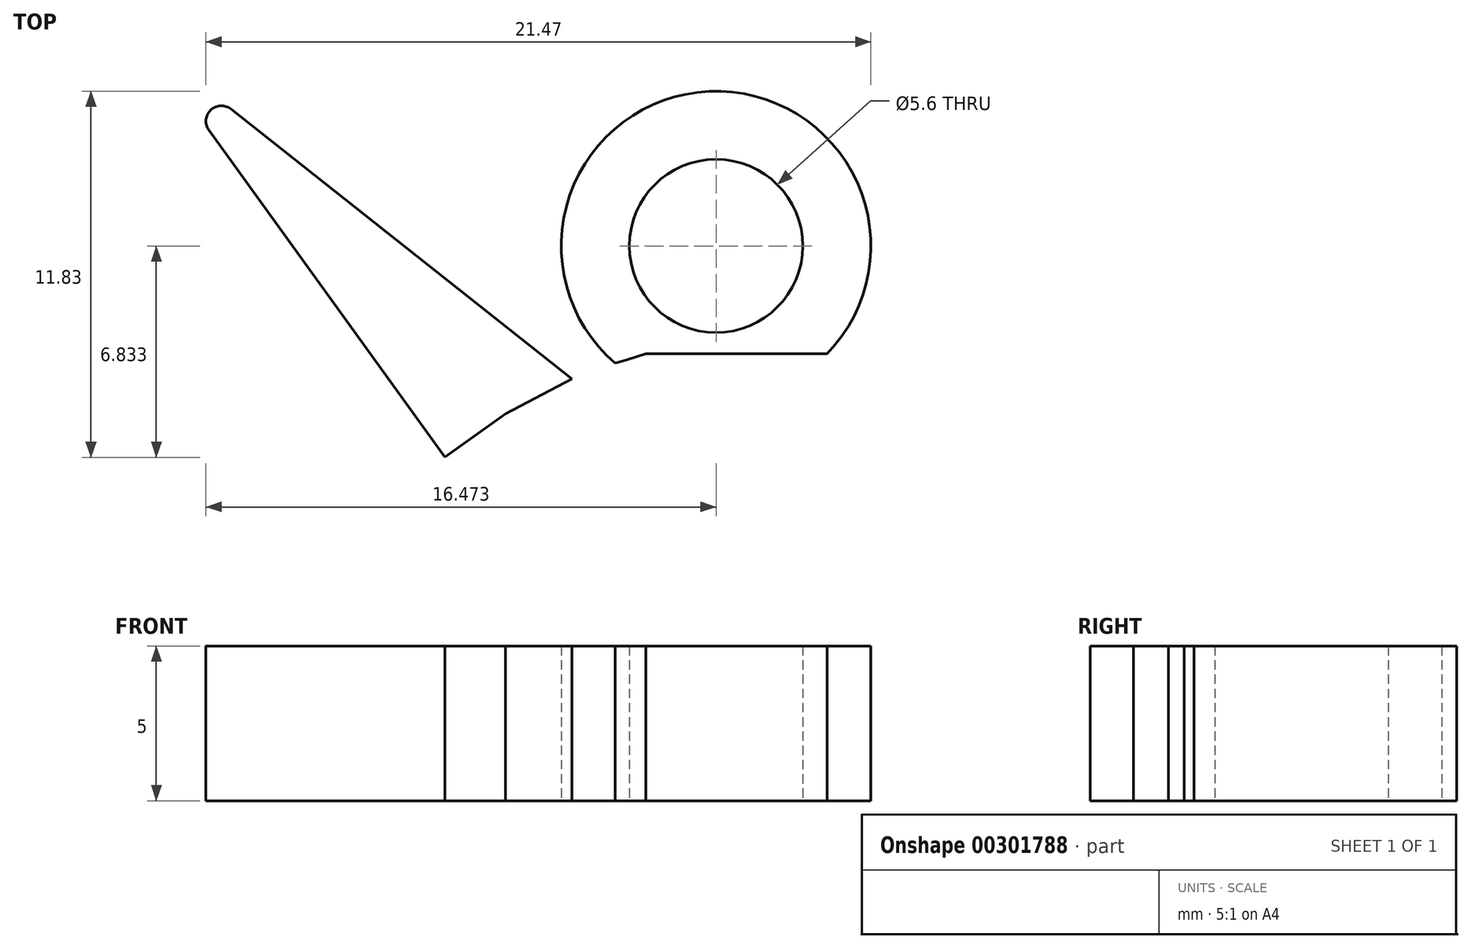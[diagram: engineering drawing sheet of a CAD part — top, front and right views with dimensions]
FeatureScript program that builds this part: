
annotation { "Feature Type Name" : "Feature", "Feature Type Description" : "" }
export const myFeature = defineFeature(function(context is Context, id is Id, definition is map)
    precondition{}
    {
        {
            var Q0;
            Q0=qCreatedBy(makeId("Top.planeOp"),FACE);
            var sketch = newSketch(context, id + "F0", { "sketchPlane" : qUnion([Q0])});
            skLineSegment(sketch, "E0", {"start": v(-9.72, 30) * mm, "end": v(0.2, 30) * mm});
            skLineSegment(sketch, "E1", {"start": v(0.2, 30) * mm, "end": v(10.14, 30) * mm});
            skLineSegment(sketch, "E2", {"start": v(10.14, 30) * mm, "end": v(20.07, 30) * mm});
            skLineSegment(sketch, "E3", {"start": v(20.07, 30) * mm, "end": v(30, 30) * mm});
            skLineSegment(sketch, "E4", {"start": v(30, 15) * mm, "end": v(30, 0) * mm});
            skLineSegment(sketch, "E5", {"start": v(30, 0) * mm, "end": v(30, -15) * mm});
            skLineSegment(sketch, "E6", {"start": v(30, -15) * mm, "end": v(30, -30) * mm});
            skLineSegment(sketch, "E7", {"start": v(30, -30) * mm, "end": v(19.17, -30) * mm});
            skLineSegment(sketch, "E8", {"start": v(19.17, -30) * mm, "end": v(8.34, -30) * mm});
            skLineSegment(sketch, "E9", {"start": v(8.34, -30) * mm, "end": v(-2.49, -30) * mm});
            skLineSegment(sketch, "E10", {"start": v(-2.49, -30) * mm, "end": v(-13.32, -30) * mm});
            skLineSegment(sketch, "E11", {"start": v(-13.32, -30) * mm, "end": v(-12.87, -29.51) * mm});
            skLineSegment(sketch, "E12", {"start": v(-12.87, -29.51) * mm, "end": v(-12.4, -29.04) * mm});
            skLineSegment(sketch, "E13", {"start": v(-12.4, -29.04) * mm, "end": v(-11.98, -28.54) * mm});
            skLineSegment(sketch, "E14", {"start": v(-11.98, -28.54) * mm, "end": v(-11.7, -28) * mm});
            skLineSegment(sketch, "E15", {"start": v(-11.7, -28) * mm, "end": v(-10.95, -26.2) * mm});
            skLineSegment(sketch, "E16", {"start": v(-10.95, -26.2) * mm, "end": v(-10.13, -24.44) * mm});
            skLineSegment(sketch, "E17", {"start": v(-10.13, -24.44) * mm, "end": v(-9.4, -22.64) * mm});
            skLineSegment(sketch, "E18", {"start": v(-9.4, -22.64) * mm, "end": v(-8.98, -20.73) * mm});
            skLineSegment(sketch, "E19", {"start": v(-8.98, -20.73) * mm, "end": v(-8.9, -20.42) * mm});
            skLineSegment(sketch, "E20", {"start": v(-8.9, -20.42) * mm, "end": v(-8.72, -20.17) * mm});
            skLineSegment(sketch, "E21", {"start": v(-8.72, -20.17) * mm, "end": v(-8.45, -20.01) * mm});
            skLineSegment(sketch, "E22", {"start": v(-8.45, -20.01) * mm, "end": v(-8.12, -19.96) * mm});
            skLineSegment(sketch, "E23", {"start": v(-8.12, -19.96) * mm, "end": v(-7.68, -19.98) * mm});
            skLineSegment(sketch, "E24", {"start": v(-7.68, -19.98) * mm, "end": v(-7.25, -20.02) * mm});
            skLineSegment(sketch, "E25", {"start": v(-7.25, -20.02) * mm, "end": v(-6.82, -20.06) * mm});
            skLineSegment(sketch, "E26", {"start": v(-6.82, -20.06) * mm, "end": v(-6.39, -20.1) * mm});
            skLineSegment(sketch, "E27", {"start": v(-6.39, -20.1) * mm, "end": v(-5.28, -20.19) * mm});
            skLineSegment(sketch, "E28", {"start": v(-5.28, -20.19) * mm, "end": v(-4.18, -20.28) * mm});
            skLineSegment(sketch, "E29", {"start": v(-4.18, -20.28) * mm, "end": v(-3.08, -20.35) * mm});
            skLineSegment(sketch, "E30", {"start": v(-3.08, -20.35) * mm, "end": v(-1.97, -20.37) * mm});
            skLineSegment(sketch, "E31", {"start": v(-1.97, -20.37) * mm, "end": v(-1.38, -20.31) * mm});
            skLineSegment(sketch, "E32", {"start": v(-1.38, -20.31) * mm, "end": v(-0.78, -20.18) * mm});
            skLineSegment(sketch, "E33", {"start": v(-0.78, -20.18) * mm, "end": v(-0.18, -20.02) * mm});
            skLineSegment(sketch, "E34", {"start": v(-0.18, -20.02) * mm, "end": v(0.42, -19.86) * mm});
            skLineSegment(sketch, "E35", {"start": v(0.42, -19.86) * mm, "end": v(0.94, -19.84) * mm});
            skLineSegment(sketch, "E36", {"start": v(0.94, -19.84) * mm, "end": v(1.34, -20) * mm});
            skLineSegment(sketch, "E37", {"start": v(1.34, -20) * mm, "end": v(1.6, -20.34) * mm});
            skLineSegment(sketch, "E38", {"start": v(1.6, -20.34) * mm, "end": v(1.7, -20.85) * mm});
            skLineSegment(sketch, "E39", {"start": v(1.7, -20.85) * mm, "end": v(1.69, -21.03) * mm});
            skLineSegment(sketch, "E40", {"start": v(1.69, -21.03) * mm, "end": v(1.67, -21.2) * mm});
            skLineSegment(sketch, "E41", {"start": v(1.67, -21.2) * mm, "end": v(1.65, -21.38) * mm});
            skLineSegment(sketch, "E42", {"start": v(1.65, -21.38) * mm, "end": v(1.61, -21.56) * mm});
            skLineSegment(sketch, "E43", {"start": v(1.61, -21.56) * mm, "end": v(1.44, -22.04) * mm});
            skLineSegment(sketch, "E44", {"start": v(1.44, -22.04) * mm, "end": v(1.19, -22.29) * mm});
            skLineSegment(sketch, "E45", {"start": v(1.19, -22.29) * mm, "end": v(0.84, -22.3) * mm});
            skLineSegment(sketch, "E46", {"start": v(0.84, -22.3) * mm, "end": v(0.37, -22.1) * mm});
            skLineSegment(sketch, "E47", {"start": v(0.37, -22.1) * mm, "end": v(-0.3, -21.8) * mm});
            skLineSegment(sketch, "E48", {"start": v(-0.3, -21.8) * mm, "end": v(-1, -21.59) * mm});
            skLineSegment(sketch, "E49", {"start": v(-1, -21.59) * mm, "end": v(-1.72, -21.49) * mm});
            skLineSegment(sketch, "E50", {"start": v(-1.72, -21.49) * mm, "end": v(-2.45, -21.48) * mm});
            skLineSegment(sketch, "E51", {"start": v(-2.45, -21.48) * mm, "end": v(-3.08, -21.63) * mm});
            skLineSegment(sketch, "E52", {"start": v(-3.08, -21.63) * mm, "end": v(-3.5, -22) * mm});
            skLineSegment(sketch, "E53", {"start": v(-3.5, -22) * mm, "end": v(-3.7, -22.5) * mm});
            skLineSegment(sketch, "E54", {"start": v(-3.7, -22.5) * mm, "end": v(-3.58, -23.06) * mm});
            skLineSegment(sketch, "E55", {"start": v(-3.58, -23.06) * mm, "end": v(-2.94, -24.22) * mm});
            skLineSegment(sketch, "E56", {"start": v(-2.94, -24.22) * mm, "end": v(-2.19, -25.3) * mm});
            skLineSegment(sketch, "E57", {"start": v(-2.19, -25.3) * mm, "end": v(-1.3, -26.25) * mm});
            skLineSegment(sketch, "E58", {"start": v(-1.3, -26.25) * mm, "end": v(-0.23, -27.05) * mm});
            skLineSegment(sketch, "E59", {"start": v(-0.23, -27.05) * mm, "end": v(0.72, -27.6) * mm});
            skLineSegment(sketch, "E60", {"start": v(0.72, -27.6) * mm, "end": v(1.68, -28.11) * mm});
            skLineSegment(sketch, "E61", {"start": v(1.68, -28.11) * mm, "end": v(2.65, -28.62) * mm});
            skLineSegment(sketch, "E62", {"start": v(2.65, -28.62) * mm, "end": v(3.6, -29.15) * mm});
            skLineSegment(sketch, "E63", {"start": v(3.6, -29.15) * mm, "end": v(4.42, -29.38) * mm});
            skLineSegment(sketch, "E64", {"start": v(4.42, -29.38) * mm, "end": v(5.22, -29.2) * mm});
            skLineSegment(sketch, "E65", {"start": v(5.22, -29.2) * mm, "end": v(5.84, -28.62) * mm});
            skLineSegment(sketch, "E66", {"start": v(5.84, -28.62) * mm, "end": v(6.1, -27.63) * mm});
            skLineSegment(sketch, "E67", {"start": v(6.1, -27.63) * mm, "end": v(6.16, -25.8) * mm});
            skLineSegment(sketch, "E68", {"start": v(6.16, -25.8) * mm, "end": v(6.27, -23.95) * mm});
            skLineSegment(sketch, "E69", {"start": v(6.27, -23.95) * mm, "end": v(6.39, -22.12) * mm});
            skLineSegment(sketch, "E70", {"start": v(6.39, -22.12) * mm, "end": v(6.52, -20.28) * mm});
            skLineSegment(sketch, "E71", {"start": v(6.52, -20.28) * mm, "end": v(6.59, -19.83) * mm});
            skLineSegment(sketch, "E72", {"start": v(6.59, -19.83) * mm, "end": v(6.75, -19.55) * mm});
            skLineSegment(sketch, "E73", {"start": v(6.75, -19.55) * mm, "end": v(7.02, -19.43) * mm});
            skLineSegment(sketch, "E74", {"start": v(7.02, -19.43) * mm, "end": v(7.45, -19.42) * mm});
            skLineSegment(sketch, "E75", {"start": v(7.45, -19.42) * mm, "end": v(8.86, -19.4) * mm});
            skLineSegment(sketch, "E76", {"start": v(8.86, -19.4) * mm, "end": v(10.22, -19.2) * mm});
            skLineSegment(sketch, "E77", {"start": v(10.22, -19.2) * mm, "end": v(11.54, -18.8) * mm});
            skLineSegment(sketch, "E78", {"start": v(11.54, -18.8) * mm, "end": v(12.83, -18.26) * mm});
            skLineSegment(sketch, "E79", {"start": v(12.83, -18.26) * mm, "end": v(14.91, -16.97) * mm});
            skLineSegment(sketch, "E80", {"start": v(14.91, -16.97) * mm, "end": v(16.69, -15.38) * mm});
            skLineSegment(sketch, "E81", {"start": v(16.69, -15.38) * mm, "end": v(18.24, -13.56) * mm});
            skLineSegment(sketch, "E82", {"start": v(18.24, -13.56) * mm, "end": v(19.64, -11.58) * mm});
            skLineSegment(sketch, "E83", {"start": v(19.64, -11.58) * mm, "end": v(19.78, -11.28) * mm});
            skLineSegment(sketch, "E84", {"start": v(19.78, -11.28) * mm, "end": v(19.85, -10.93) * mm});
            skLineSegment(sketch, "E85", {"start": v(19.85, -10.93) * mm, "end": v(19.89, -10.57) * mm});
            skLineSegment(sketch, "E86", {"start": v(19.89, -10.57) * mm, "end": v(19.94, -10.21) * mm});
            skLineSegment(sketch, "E87", {"start": v(19.94, -10.21) * mm, "end": v(19.98, -10.02) * mm});
            skLineSegment(sketch, "E88", {"start": v(19.98, -10.02) * mm, "end": v(20.01, -9.84) * mm});
            skLineSegment(sketch, "E89", {"start": v(20.01, -9.84) * mm, "end": v(20.06, -9.66) * mm});
            skLineSegment(sketch, "E90", {"start": v(20.06, -9.66) * mm, "end": v(20.14, -9.5) * mm});
            skLineSegment(sketch, "E91", {"start": v(20.14, -9.5) * mm, "end": v(20.58, -9.2) * mm});
            skLineSegment(sketch, "E92", {"start": v(20.58, -9.2) * mm, "end": v(21.19, -9.15) * mm});
            skLineSegment(sketch, "E93", {"start": v(21.19, -9.15) * mm, "end": v(21.8, -9.3) * mm});
            skLineSegment(sketch, "E94", {"start": v(21.8, -9.3) * mm, "end": v(22.28, -9.67) * mm});
            skLineSegment(sketch, "E95", {"start": v(22.28, -9.67) * mm, "end": v(22.59, -9.96) * mm});
            skLineSegment(sketch, "E96", {"start": v(22.59, -9.96) * mm, "end": v(22.88, -10.07) * mm});
            skLineSegment(sketch, "E97", {"start": v(22.88, -10.07) * mm, "end": v(23.14, -10) * mm});
            skLineSegment(sketch, "E98", {"start": v(23.14, -10) * mm, "end": v(23.34, -9.7) * mm});
            skLineSegment(sketch, "E99", {"start": v(23.34, -9.7) * mm, "end": v(23.59, -9.28) * mm});
            skLineSegment(sketch, "E100", {"start": v(23.59, -9.28) * mm, "end": v(23.91, -9.02) * mm});
            skLineSegment(sketch, "E101", {"start": v(23.91, -9.02) * mm, "end": v(24.3, -8.88) * mm});
            skLineSegment(sketch, "E102", {"start": v(24.3, -8.88) * mm, "end": v(24.74, -8.82) * mm});
            skLineSegment(sketch, "E103", {"start": v(24.74, -8.82) * mm, "end": v(25.11, -8.75) * mm});
            skLineSegment(sketch, "E104", {"start": v(25.11, -8.75) * mm, "end": v(25.4, -8.6) * mm});
            skLineSegment(sketch, "E105", {"start": v(25.4, -8.6) * mm, "end": v(25.57, -8.35) * mm});
            skLineSegment(sketch, "E106", {"start": v(25.57, -8.35) * mm, "end": v(25.6, -7.94) * mm});
            skLineSegment(sketch, "E107", {"start": v(25.6, -7.94) * mm, "end": v(25.62, -7.8) * mm});
            skLineSegment(sketch, "E108", {"start": v(25.62, -7.8) * mm, "end": v(25.67, -7.66) * mm});
            skLineSegment(sketch, "E109", {"start": v(25.67, -7.66) * mm, "end": v(25.75, -7.52) * mm});
            skLineSegment(sketch, "E110", {"start": v(25.75, -7.52) * mm, "end": v(25.82, -7.4) * mm});
            skLineSegment(sketch, "E111", {"start": v(25.82, -7.4) * mm, "end": v(26.1, -6.66) * mm});
            skLineSegment(sketch, "E112", {"start": v(26.1, -6.66) * mm, "end": v(26.15, -5.95) * mm});
            skLineSegment(sketch, "E113", {"start": v(26.15, -5.95) * mm, "end": v(25.97, -5.26) * mm});
            skLineSegment(sketch, "E114", {"start": v(25.97, -5.26) * mm, "end": v(25.57, -4.6) * mm});
            skLineSegment(sketch, "E115", {"start": v(25.57, -4.6) * mm, "end": v(25.38, -4.34) * mm});
            skLineSegment(sketch, "E116", {"start": v(25.38, -4.34) * mm, "end": v(25.19, -4.07) * mm});
            skLineSegment(sketch, "E117", {"start": v(25.19, -4.07) * mm, "end": v(24.98, -3.79) * mm});
            skLineSegment(sketch, "E118", {"start": v(24.98, -3.79) * mm, "end": v(24.77, -3.49) * mm});
            skLineSegment(sketch, "E119", {"start": v(24.77, -3.49) * mm, "end": v(25.33, -3.5) * mm});
            skLineSegment(sketch, "E120", {"start": v(25.33, -3.5) * mm, "end": v(25.85, -3.52) * mm});
            skLineSegment(sketch, "E121", {"start": v(25.85, -3.52) * mm, "end": v(26.33, -3.44) * mm});
            skLineSegment(sketch, "E122", {"start": v(26.33, -3.44) * mm, "end": v(26.74, -3.1) * mm});
            skLineSegment(sketch, "E123", {"start": v(26.74, -3.1) * mm, "end": v(26.49, -2.7) * mm});
            skLineSegment(sketch, "E124", {"start": v(26.49, -2.7) * mm, "end": v(26.14, -2.47) * mm});
            skLineSegment(sketch, "E125", {"start": v(26.14, -2.47) * mm, "end": v(25.72, -2.36) * mm});
            skLineSegment(sketch, "E126", {"start": v(25.72, -2.36) * mm, "end": v(25.28, -2.3) * mm});
            skLineSegment(sketch, "E127", {"start": v(25.28, -2.3) * mm, "end": v(24.84, -2.2) * mm});
            skLineSegment(sketch, "E128", {"start": v(24.84, -2.2) * mm, "end": v(24.64, -2.05) * mm});
            skLineSegment(sketch, "E129", {"start": v(24.64, -2.05) * mm, "end": v(24.62, -1.79) * mm});
            skLineSegment(sketch, "E130", {"start": v(24.62, -1.79) * mm, "end": v(24.77, -1.37) * mm});
            skLineSegment(sketch, "E131", {"start": v(24.77, -1.37) * mm, "end": v(24.8, -1.2) * mm});
            skLineSegment(sketch, "E132", {"start": v(24.8, -1.2) * mm, "end": v(24.8, -1) * mm});
            skLineSegment(sketch, "E133", {"start": v(24.8, -1) * mm, "end": v(24.77, -0.83) * mm});
            skLineSegment(sketch, "E134", {"start": v(24.77, -0.83) * mm, "end": v(24.7, -0.72) * mm});
            skLineSegment(sketch, "E135", {"start": v(24.7, -0.72) * mm, "end": v(24.29, -0.43) * mm});
            skLineSegment(sketch, "E136", {"start": v(24.29, -0.43) * mm, "end": v(23.88, -0.15) * mm});
            skLineSegment(sketch, "E137", {"start": v(23.88, -0.15) * mm, "end": v(23.45, 0.1) * mm});
            skLineSegment(sketch, "E138", {"start": v(23.45, 0.1) * mm, "end": v(23, 0.3) * mm});
            skLineSegment(sketch, "E139", {"start": v(23, 0.3) * mm, "end": v(22.68, 0.36) * mm});
            skLineSegment(sketch, "E140", {"start": v(22.68, 0.36) * mm, "end": v(22.33, 0.36) * mm});
            skLineSegment(sketch, "E141", {"start": v(22.33, 0.36) * mm, "end": v(21.98, 0.32) * mm});
            skLineSegment(sketch, "E142", {"start": v(21.98, 0.32) * mm, "end": v(21.63, 0.26) * mm});
            skLineSegment(sketch, "E143", {"start": v(21.63, 0.26) * mm, "end": v(21.38, 0.19) * mm});
            skLineSegment(sketch, "E144", {"start": v(21.38, 0.19) * mm, "end": v(21.13, 0.08) * mm});
            skLineSegment(sketch, "E145", {"start": v(21.13, 0.08) * mm, "end": v(20.88, -0.04) * mm});
            skLineSegment(sketch, "E146", {"start": v(20.88, -0.04) * mm, "end": v(20.63, -0.14) * mm});
            skLineSegment(sketch, "E147", {"start": v(20.63, -0.14) * mm, "end": v(20.5, -0.15) * mm});
            skLineSegment(sketch, "E148", {"start": v(20.5, -0.15) * mm, "end": v(20.37, -0.14) * mm});
            skLineSegment(sketch, "E149", {"start": v(20.37, -0.14) * mm, "end": v(20.23, -0.11) * mm});
            skLineSegment(sketch, "E150", {"start": v(20.23, -0.11) * mm, "end": v(20.1, -0.1) * mm});
            skLineSegment(sketch, "E151", {"start": v(20.1, -0.1) * mm, "end": v(20.13, 0.05) * mm});
            skLineSegment(sketch, "E152", {"start": v(20.13, 0.05) * mm, "end": v(20.16, 0.19) * mm});
            skLineSegment(sketch, "E153", {"start": v(20.16, 0.19) * mm, "end": v(20.2, 0.32) * mm});
            skLineSegment(sketch, "E154", {"start": v(20.2, 0.32) * mm, "end": v(20.26, 0.42) * mm});
            skLineSegment(sketch, "E155", {"start": v(20.26, 0.42) * mm, "end": v(20.7, 0.96) * mm});
            skLineSegment(sketch, "E156", {"start": v(20.7, 0.96) * mm, "end": v(21.07, 1.53) * mm});
            skLineSegment(sketch, "E157", {"start": v(21.07, 1.53) * mm, "end": v(21.36, 2.15) * mm});
            skLineSegment(sketch, "E158", {"start": v(21.36, 2.15) * mm, "end": v(21.58, 2.8) * mm});
            skLineSegment(sketch, "E159", {"start": v(21.58, 2.8) * mm, "end": v(21.8, 3.55) * mm});
            skLineSegment(sketch, "E160", {"start": v(21.8, 3.55) * mm, "end": v(22.03, 4.3) * mm});
            skLineSegment(sketch, "E161", {"start": v(22.03, 4.3) * mm, "end": v(22.26, 5.04) * mm});
            skLineSegment(sketch, "E162", {"start": v(22.26, 5.04) * mm, "end": v(22.5, 5.78) * mm});
            skLineSegment(sketch, "E163", {"start": v(22.5, 5.78) * mm, "end": v(22.83, 7.49) * mm});
            skLineSegment(sketch, "E164", {"start": v(22.83, 7.49) * mm, "end": v(22.65, 9.09) * mm});
            skLineSegment(sketch, "E165", {"start": v(22.65, 9.09) * mm, "end": v(21.97, 10.54) * mm});
            skLineSegment(sketch, "E166", {"start": v(21.97, 10.54) * mm, "end": v(20.8, 11.82) * mm});
            skLineSegment(sketch, "E167", {"start": v(20.8, 11.82) * mm, "end": v(19.35, 12.58) * mm});
            skLineSegment(sketch, "E168", {"start": v(19.35, 12.58) * mm, "end": v(17.91, 12.58) * mm});
            skLineSegment(sketch, "E169", {"start": v(17.91, 12.58) * mm, "end": v(16.66, 11.87) * mm});
            skLineSegment(sketch, "E170", {"start": v(16.66, 11.87) * mm, "end": v(15.78, 10.5) * mm});
            skLineSegment(sketch, "E171", {"start": v(15.78, 10.5) * mm, "end": v(15.44, 9.6) * mm});
            skLineSegment(sketch, "E172", {"start": v(15.44, 9.6) * mm, "end": v(15.08, 8.71) * mm});
            skLineSegment(sketch, "E173", {"start": v(15.08, 8.71) * mm, "end": v(14.72, 7.83) * mm});
            skLineSegment(sketch, "E174", {"start": v(14.72, 7.83) * mm, "end": v(14.36, 6.94) * mm});
            skLineSegment(sketch, "E175", {"start": v(14.36, 6.94) * mm, "end": v(14.2, 6.53) * mm});
            skLineSegment(sketch, "E176", {"start": v(14.2, 6.53) * mm, "end": v(14.03, 6.1) * mm});
            skLineSegment(sketch, "E177", {"start": v(14.03, 6.1) * mm, "end": v(13.86, 5.7) * mm});
            skLineSegment(sketch, "E178", {"start": v(13.86, 5.7) * mm, "end": v(13.67, 5.3) * mm});
            skLineSegment(sketch, "E179", {"start": v(13.67, 5.3) * mm, "end": v(13.36, 4.67) * mm});
            skLineSegment(sketch, "E180", {"start": v(13.36, 4.67) * mm, "end": v(13.04, 4.04) * mm});
            skLineSegment(sketch, "E181", {"start": v(13.04, 4.04) * mm, "end": v(12.7, 3.43) * mm});
            skLineSegment(sketch, "E182", {"start": v(12.7, 3.43) * mm, "end": v(12.36, 2.82) * mm});
            skLineSegment(sketch, "E183", {"start": v(12.36, 2.82) * mm, "end": v(12.07, 2.48) * mm});
            skLineSegment(sketch, "E184", {"start": v(12.07, 2.48) * mm, "end": v(11.72, 2.3) * mm});
            skLineSegment(sketch, "E185", {"start": v(11.72, 2.3) * mm, "end": v(11.3, 2.28) * mm});
            skLineSegment(sketch, "E186", {"start": v(11.3, 2.28) * mm, "end": v(10.85, 2.35) * mm});
            skLineSegment(sketch, "E187", {"start": v(10.85, 2.35) * mm, "end": v(10.25, 2.5) * mm});
            skLineSegment(sketch, "E188", {"start": v(10.25, 2.5) * mm, "end": v(9.64, 2.62) * mm});
            skLineSegment(sketch, "E189", {"start": v(9.64, 2.62) * mm, "end": v(9.03, 2.7) * mm});
            skLineSegment(sketch, "E190", {"start": v(9.03, 2.7) * mm, "end": v(8.43, 2.71) * mm});
            skLineSegment(sketch, "E191", {"start": v(8.43, 2.71) * mm, "end": v(6.82, 2.59) * mm});
            skLineSegment(sketch, "E192", {"start": v(6.82, 2.59) * mm, "end": v(5.23, 2.37) * mm});
            skLineSegment(sketch, "E193", {"start": v(5.23, 2.37) * mm, "end": v(3.68, 1.96) * mm});
            skLineSegment(sketch, "E194", {"start": v(3.68, 1.96) * mm, "end": v(2.2, 1.27) * mm});
            skLineSegment(sketch, "E195", {"start": v(2.2, 1.27) * mm, "end": v(1.62, 1.01) * mm});
            skLineSegment(sketch, "E196", {"start": v(1.62, 1.01) * mm, "end": v(1.22, 1.02) * mm});
            skLineSegment(sketch, "E197", {"start": v(1.22, 1.02) * mm, "end": v(0.93, 1.3) * mm});
            skLineSegment(sketch, "E198", {"start": v(0.93, 1.3) * mm, "end": v(0.73, 1.89) * mm});
            skLineSegment(sketch, "E199", {"start": v(0.73, 1.89) * mm, "end": v(0.37, 3.4) * mm});
            skLineSegment(sketch, "E200", {"start": v(0.37, 3.4) * mm, "end": v(0.01, 4.9) * mm});
            skLineSegment(sketch, "E201", {"start": v(0.01, 4.9) * mm, "end": v(-0.27, 6.42) * mm});
            skLineSegment(sketch, "E202", {"start": v(-0.27, 6.42) * mm, "end": v(-0.42, 7.93) * mm});
            skLineSegment(sketch, "E203", {"start": v(-0.42, 7.93) * mm, "end": v(-0.46, 10.67) * mm});
            skLineSegment(sketch, "E204", {"start": v(-0.46, 10.67) * mm, "end": v(-0.4, 13.4) * mm});
            skLineSegment(sketch, "E205", {"start": v(-0.4, 13.4) * mm, "end": v(-0.33, 16.15) * mm});
            skLineSegment(sketch, "E206", {"start": v(-0.33, 16.15) * mm, "end": v(-0.25, 18.89) * mm});
            skLineSegment(sketch, "E207", {"start": v(-0.25, 18.89) * mm, "end": v(-0.24, 19.43) * mm});
            skLineSegment(sketch, "E208", {"start": v(-0.24, 19.43) * mm, "end": v(-0.24, 19.97) * mm});
            skLineSegment(sketch, "E209", {"start": v(-0.24, 19.97) * mm, "end": v(-0.26, 20.5) * mm});
            skLineSegment(sketch, "E210", {"start": v(-0.26, 20.5) * mm, "end": v(-0.33, 21.04) * mm});
            skLineSegment(sketch, "E211", {"start": v(-0.33, 21.04) * mm, "end": v(-0.72, 22.63) * mm});
            skLineSegment(sketch, "E212", {"start": v(-0.72, 22.63) * mm, "end": v(-1.3, 24.14) * mm});
            skLineSegment(sketch, "E213", {"start": v(-1.3, 24.14) * mm, "end": v(-2.07, 25.57) * mm});
            skLineSegment(sketch, "E214", {"start": v(-2.07, 25.57) * mm, "end": v(-2.98, 26.94) * mm});
            skLineSegment(sketch, "E215", {"start": v(-2.98, 26.94) * mm, "end": v(-3.79, 27.87) * mm});
            skLineSegment(sketch, "E216", {"start": v(-3.79, 27.87) * mm, "end": v(-4.72, 28.62) * mm});
            skLineSegment(sketch, "E217", {"start": v(-4.72, 28.62) * mm, "end": v(-5.77, 29.18) * mm});
            skLineSegment(sketch, "E218", {"start": v(-5.77, 29.18) * mm, "end": v(-6.95, 29.53) * mm});
            skLineSegment(sketch, "E219", {"start": v(-6.95, 29.53) * mm, "end": v(-7.64, 29.66) * mm});
            skLineSegment(sketch, "E220", {"start": v(-7.64, 29.66) * mm, "end": v(-8.34, 29.77) * mm});
            skLineSegment(sketch, "E221", {"start": v(-8.34, 29.77) * mm, "end": v(-9.03, 29.89) * mm});
            skLineSegment(sketch, "E222", {"start": v(-9.03, 29.89) * mm, "end": v(-9.72, 30) * mm});
            skLineSegment(sketch, "E223", {"start": v(-9.72, 30) * mm, "end": v(-9.03, 29.89) * mm});
            skLineSegment(sketch, "E224", {"start": v(-9.03, 29.89) * mm, "end": v(-8.34, 29.77) * mm});
            skLineSegment(sketch, "E225", {"start": v(-8.34, 29.77) * mm, "end": v(-7.64, 29.66) * mm});
            skLineSegment(sketch, "E226", {"start": v(-7.64, 29.66) * mm, "end": v(-6.95, 29.53) * mm});
            skLineSegment(sketch, "E227", {"start": v(-6.95, 29.53) * mm, "end": v(-5.77, 29.18) * mm});
            skLineSegment(sketch, "E228", {"start": v(-5.77, 29.18) * mm, "end": v(-4.72, 28.62) * mm});
            skLineSegment(sketch, "E229", {"start": v(-4.72, 28.62) * mm, "end": v(-3.79, 27.87) * mm});
            skLineSegment(sketch, "E230", {"start": v(-3.79, 27.87) * mm, "end": v(-2.98, 26.94) * mm});
            skLineSegment(sketch, "E231", {"start": v(-2.98, 26.94) * mm, "end": v(-2.07, 25.57) * mm});
            skLineSegment(sketch, "E232", {"start": v(-2.07, 25.57) * mm, "end": v(-1.3, 24.14) * mm});
            skLineSegment(sketch, "E233", {"start": v(-1.3, 24.14) * mm, "end": v(-0.72, 22.63) * mm});
            skLineSegment(sketch, "E234", {"start": v(-0.72, 22.63) * mm, "end": v(-0.33, 21.04) * mm});
            skLineSegment(sketch, "E235", {"start": v(-0.33, 21.04) * mm, "end": v(-0.26, 20.5) * mm});
            skLineSegment(sketch, "E236", {"start": v(-0.26, 20.5) * mm, "end": v(-0.24, 19.97) * mm});
            skLineSegment(sketch, "E237", {"start": v(-0.24, 19.97) * mm, "end": v(-0.24, 19.43) * mm});
            skLineSegment(sketch, "E238", {"start": v(-0.24, 19.43) * mm, "end": v(-0.25, 18.89) * mm});
            skLineSegment(sketch, "E239", {"start": v(-0.25, 18.89) * mm, "end": v(-0.33, 16.15) * mm});
            skLineSegment(sketch, "E240", {"start": v(-0.33, 16.15) * mm, "end": v(-0.4, 13.4) * mm});
            skLineSegment(sketch, "E241", {"start": v(-0.4, 13.4) * mm, "end": v(-0.46, 10.67) * mm});
            skLineSegment(sketch, "E242", {"start": v(-0.46, 10.67) * mm, "end": v(-0.42, 7.93) * mm});
            skLineSegment(sketch, "E243", {"start": v(-0.42, 7.93) * mm, "end": v(-0.27, 6.42) * mm});
            skLineSegment(sketch, "E244", {"start": v(-0.27, 6.42) * mm, "end": v(0.01, 4.9) * mm});
            skLineSegment(sketch, "E245", {"start": v(0.01, 4.9) * mm, "end": v(0.37, 3.4) * mm});
            skLineSegment(sketch, "E246", {"start": v(0.37, 3.4) * mm, "end": v(0.73, 1.89) * mm});
            skLineSegment(sketch, "E247", {"start": v(0.73, 1.89) * mm, "end": v(0.93, 1.3) * mm});
            skLineSegment(sketch, "E248", {"start": v(0.93, 1.3) * mm, "end": v(1.22, 1.02) * mm});
            skLineSegment(sketch, "E249", {"start": v(1.22, 1.02) * mm, "end": v(1.62, 1.01) * mm});
            skLineSegment(sketch, "E250", {"start": v(1.62, 1.01) * mm, "end": v(2.2, 1.27) * mm});
            skLineSegment(sketch, "E251", {"start": v(2.2, 1.27) * mm, "end": v(3.68, 1.96) * mm});
            skLineSegment(sketch, "E252", {"start": v(3.68, 1.96) * mm, "end": v(5.23, 2.37) * mm});
            skLineSegment(sketch, "E253", {"start": v(5.23, 2.37) * mm, "end": v(6.82, 2.59) * mm});
            skLineSegment(sketch, "E254", {"start": v(6.82, 2.59) * mm, "end": v(8.43, 2.71) * mm});
            skLineSegment(sketch, "E255", {"start": v(8.43, 2.71) * mm, "end": v(9.03, 2.7) * mm});
            skLineSegment(sketch, "E256", {"start": v(9.03, 2.7) * mm, "end": v(9.64, 2.62) * mm});
            skLineSegment(sketch, "E257", {"start": v(9.64, 2.62) * mm, "end": v(10.25, 2.5) * mm});
            skLineSegment(sketch, "E258", {"start": v(10.25, 2.5) * mm, "end": v(10.85, 2.35) * mm});
            skLineSegment(sketch, "E259", {"start": v(10.85, 2.35) * mm, "end": v(11.3, 2.28) * mm});
            skLineSegment(sketch, "E260", {"start": v(11.3, 2.28) * mm, "end": v(11.72, 2.3) * mm});
            skLineSegment(sketch, "E261", {"start": v(11.72, 2.3) * mm, "end": v(12.07, 2.48) * mm});
            skLineSegment(sketch, "E262", {"start": v(12.07, 2.48) * mm, "end": v(12.36, 2.82) * mm});
            skLineSegment(sketch, "E263", {"start": v(12.36, 2.82) * mm, "end": v(12.7, 3.43) * mm});
            skLineSegment(sketch, "E264", {"start": v(12.7, 3.43) * mm, "end": v(13.04, 4.04) * mm});
            skLineSegment(sketch, "E265", {"start": v(13.04, 4.04) * mm, "end": v(13.36, 4.67) * mm});
            skLineSegment(sketch, "E266", {"start": v(13.36, 4.67) * mm, "end": v(13.67, 5.3) * mm});
            skLineSegment(sketch, "E267", {"start": v(13.67, 5.3) * mm, "end": v(13.86, 5.7) * mm});
            skLineSegment(sketch, "E268", {"start": v(13.86, 5.7) * mm, "end": v(14.03, 6.1) * mm});
            skLineSegment(sketch, "E269", {"start": v(14.03, 6.1) * mm, "end": v(14.2, 6.53) * mm});
            skLineSegment(sketch, "E270", {"start": v(14.2, 6.53) * mm, "end": v(14.36, 6.94) * mm});
            skLineSegment(sketch, "E271", {"start": v(14.36, 6.94) * mm, "end": v(14.72, 7.83) * mm});
            skLineSegment(sketch, "E272", {"start": v(14.72, 7.83) * mm, "end": v(15.08, 8.71) * mm});
            skLineSegment(sketch, "E273", {"start": v(15.08, 8.71) * mm, "end": v(15.44, 9.6) * mm});
            skLineSegment(sketch, "E274", {"start": v(15.44, 9.6) * mm, "end": v(15.78, 10.5) * mm});
            skLineSegment(sketch, "E275", {"start": v(15.78, 10.5) * mm, "end": v(16.66, 11.87) * mm});
            skLineSegment(sketch, "E276", {"start": v(16.66, 11.87) * mm, "end": v(17.91, 12.58) * mm});
            skLineSegment(sketch, "E277", {"start": v(17.91, 12.58) * mm, "end": v(19.35, 12.58) * mm});
            skLineSegment(sketch, "E278", {"start": v(19.35, 12.58) * mm, "end": v(20.8, 11.82) * mm});
            skLineSegment(sketch, "E279", {"start": v(20.8, 11.82) * mm, "end": v(21.97, 10.54) * mm});
            skLineSegment(sketch, "E280", {"start": v(21.97, 10.54) * mm, "end": v(22.65, 9.09) * mm});
            skLineSegment(sketch, "E281", {"start": v(22.65, 9.09) * mm, "end": v(22.83, 7.49) * mm});
            skLineSegment(sketch, "E282", {"start": v(22.83, 7.49) * mm, "end": v(22.5, 5.78) * mm});
            skLineSegment(sketch, "E283", {"start": v(22.5, 5.78) * mm, "end": v(22.26, 5.04) * mm});
            skLineSegment(sketch, "E284", {"start": v(22.26, 5.04) * mm, "end": v(22.03, 4.3) * mm});
            skLineSegment(sketch, "E285", {"start": v(22.03, 4.3) * mm, "end": v(21.8, 3.55) * mm});
            skLineSegment(sketch, "E286", {"start": v(21.8, 3.55) * mm, "end": v(21.58, 2.8) * mm});
            skLineSegment(sketch, "E287", {"start": v(21.58, 2.8) * mm, "end": v(21.36, 2.15) * mm});
            skLineSegment(sketch, "E288", {"start": v(21.36, 2.15) * mm, "end": v(21.07, 1.53) * mm});
            skLineSegment(sketch, "E289", {"start": v(21.07, 1.53) * mm, "end": v(20.7, 0.96) * mm});
            skLineSegment(sketch, "E290", {"start": v(20.7, 0.96) * mm, "end": v(20.26, 0.42) * mm});
            skLineSegment(sketch, "E291", {"start": v(20.26, 0.42) * mm, "end": v(20.2, 0.32) * mm});
            skLineSegment(sketch, "E292", {"start": v(20.2, 0.32) * mm, "end": v(20.16, 0.19) * mm});
            skLineSegment(sketch, "E293", {"start": v(20.16, 0.19) * mm, "end": v(20.13, 0.05) * mm});
            skLineSegment(sketch, "E294", {"start": v(20.13, 0.05) * mm, "end": v(20.1, -0.1) * mm});
            skLineSegment(sketch, "E295", {"start": v(20.1, -0.1) * mm, "end": v(20.23, -0.11) * mm});
            skLineSegment(sketch, "E296", {"start": v(20.23, -0.11) * mm, "end": v(20.37, -0.14) * mm});
            skLineSegment(sketch, "E297", {"start": v(20.37, -0.14) * mm, "end": v(20.5, -0.15) * mm});
            skLineSegment(sketch, "E298", {"start": v(20.5, -0.15) * mm, "end": v(20.63, -0.14) * mm});
            skLineSegment(sketch, "E299", {"start": v(20.63, -0.14) * mm, "end": v(20.88, -0.04) * mm});
            skLineSegment(sketch, "E300", {"start": v(20.88, -0.04) * mm, "end": v(21.13, 0.08) * mm});
            skLineSegment(sketch, "E301", {"start": v(21.13, 0.08) * mm, "end": v(21.38, 0.19) * mm});
            skLineSegment(sketch, "E302", {"start": v(21.38, 0.19) * mm, "end": v(21.63, 0.26) * mm});
            skLineSegment(sketch, "E303", {"start": v(21.63, 0.26) * mm, "end": v(21.98, 0.32) * mm});
            skLineSegment(sketch, "E304", {"start": v(21.98, 0.32) * mm, "end": v(22.33, 0.36) * mm});
            skLineSegment(sketch, "E305", {"start": v(22.33, 0.36) * mm, "end": v(22.68, 0.36) * mm});
            skLineSegment(sketch, "E306", {"start": v(22.68, 0.36) * mm, "end": v(23, 0.3) * mm});
            skLineSegment(sketch, "E307", {"start": v(23, 0.3) * mm, "end": v(23.45, 0.1) * mm});
            skLineSegment(sketch, "E308", {"start": v(23.45, 0.1) * mm, "end": v(23.88, -0.15) * mm});
            skLineSegment(sketch, "E309", {"start": v(23.88, -0.15) * mm, "end": v(24.29, -0.43) * mm});
            skLineSegment(sketch, "E310", {"start": v(24.29, -0.43) * mm, "end": v(24.7, -0.72) * mm});
            skLineSegment(sketch, "E311", {"start": v(24.7, -0.72) * mm, "end": v(24.77, -0.83) * mm});
            skLineSegment(sketch, "E312", {"start": v(24.77, -0.83) * mm, "end": v(24.8, -1) * mm});
            skLineSegment(sketch, "E313", {"start": v(24.8, -1) * mm, "end": v(24.8, -1.2) * mm});
            skLineSegment(sketch, "E314", {"start": v(24.8, -1.2) * mm, "end": v(24.77, -1.37) * mm});
            skLineSegment(sketch, "E315", {"start": v(24.77, -1.37) * mm, "end": v(24.62, -1.79) * mm});
            skLineSegment(sketch, "E316", {"start": v(24.62, -1.79) * mm, "end": v(24.64, -2.05) * mm});
            skLineSegment(sketch, "E317", {"start": v(24.64, -2.05) * mm, "end": v(24.84, -2.2) * mm});
            skLineSegment(sketch, "E318", {"start": v(24.84, -2.2) * mm, "end": v(25.28, -2.3) * mm});
            skLineSegment(sketch, "E319", {"start": v(25.28, -2.3) * mm, "end": v(25.72, -2.36) * mm});
            skLineSegment(sketch, "E320", {"start": v(25.72, -2.36) * mm, "end": v(26.14, -2.47) * mm});
            skLineSegment(sketch, "E321", {"start": v(26.14, -2.47) * mm, "end": v(26.49, -2.7) * mm});
            skLineSegment(sketch, "E322", {"start": v(26.49, -2.7) * mm, "end": v(26.74, -3.1) * mm});
            skLineSegment(sketch, "E323", {"start": v(26.74, -3.1) * mm, "end": v(26.33, -3.44) * mm});
            skLineSegment(sketch, "E324", {"start": v(26.33, -3.44) * mm, "end": v(25.85, -3.52) * mm});
            skLineSegment(sketch, "E325", {"start": v(25.85, -3.52) * mm, "end": v(25.33, -3.5) * mm});
            skLineSegment(sketch, "E326", {"start": v(25.33, -3.5) * mm, "end": v(24.77, -3.49) * mm});
            skLineSegment(sketch, "E327", {"start": v(24.77, -3.49) * mm, "end": v(24.98, -3.79) * mm});
            skLineSegment(sketch, "E328", {"start": v(24.98, -3.79) * mm, "end": v(25.19, -4.07) * mm});
            skLineSegment(sketch, "E329", {"start": v(25.19, -4.07) * mm, "end": v(25.38, -4.34) * mm});
            skLineSegment(sketch, "E330", {"start": v(25.38, -4.34) * mm, "end": v(25.57, -4.6) * mm});
            skLineSegment(sketch, "E331", {"start": v(25.57, -4.6) * mm, "end": v(25.97, -5.26) * mm});
            skLineSegment(sketch, "E332", {"start": v(25.97, -5.26) * mm, "end": v(26.15, -5.95) * mm});
            skLineSegment(sketch, "E333", {"start": v(26.15, -5.95) * mm, "end": v(26.1, -6.66) * mm});
            skLineSegment(sketch, "E334", {"start": v(26.1, -6.66) * mm, "end": v(25.82, -7.4) * mm});
            skLineSegment(sketch, "E335", {"start": v(25.82, -7.4) * mm, "end": v(25.75, -7.52) * mm});
            skLineSegment(sketch, "E336", {"start": v(25.75, -7.52) * mm, "end": v(25.67, -7.66) * mm});
            skLineSegment(sketch, "E337", {"start": v(25.67, -7.66) * mm, "end": v(25.62, -7.8) * mm});
            skLineSegment(sketch, "E338", {"start": v(25.62, -7.8) * mm, "end": v(25.6, -7.94) * mm});
            skLineSegment(sketch, "E339", {"start": v(25.6, -7.94) * mm, "end": v(25.57, -8.35) * mm});
            skLineSegment(sketch, "E340", {"start": v(25.57, -8.35) * mm, "end": v(25.4, -8.6) * mm});
            skLineSegment(sketch, "E341", {"start": v(25.4, -8.6) * mm, "end": v(25.11, -8.75) * mm});
            skLineSegment(sketch, "E342", {"start": v(25.11, -8.75) * mm, "end": v(24.74, -8.82) * mm});
            skLineSegment(sketch, "E343", {"start": v(24.74, -8.82) * mm, "end": v(24.3, -8.88) * mm});
            skLineSegment(sketch, "E344", {"start": v(24.3, -8.88) * mm, "end": v(23.91, -9.02) * mm});
            skLineSegment(sketch, "E345", {"start": v(23.91, -9.02) * mm, "end": v(23.59, -9.28) * mm});
            skLineSegment(sketch, "E346", {"start": v(23.59, -9.28) * mm, "end": v(23.34, -9.7) * mm});
            skLineSegment(sketch, "E347", {"start": v(23.34, -9.7) * mm, "end": v(23.14, -10) * mm});
            skLineSegment(sketch, "E348", {"start": v(23.14, -10) * mm, "end": v(22.88, -10.07) * mm});
            skLineSegment(sketch, "E349", {"start": v(22.88, -10.07) * mm, "end": v(22.59, -9.96) * mm});
            skLineSegment(sketch, "E350", {"start": v(22.59, -9.96) * mm, "end": v(22.28, -9.67) * mm});
            skLineSegment(sketch, "E351", {"start": v(22.28, -9.67) * mm, "end": v(21.8, -9.3) * mm});
            skLineSegment(sketch, "E352", {"start": v(21.8, -9.3) * mm, "end": v(21.19, -9.15) * mm});
            skLineSegment(sketch, "E353", {"start": v(21.19, -9.15) * mm, "end": v(20.58, -9.2) * mm});
            skLineSegment(sketch, "E354", {"start": v(20.58, -9.2) * mm, "end": v(20.14, -9.5) * mm});
            skLineSegment(sketch, "E355", {"start": v(20.14, -9.5) * mm, "end": v(20.06, -9.66) * mm});
            skLineSegment(sketch, "E356", {"start": v(20.06, -9.66) * mm, "end": v(20.01, -9.84) * mm});
            skLineSegment(sketch, "E357", {"start": v(20.01, -9.84) * mm, "end": v(19.98, -10.02) * mm});
            skLineSegment(sketch, "E358", {"start": v(19.98, -10.02) * mm, "end": v(19.94, -10.21) * mm});
            skLineSegment(sketch, "E359", {"start": v(19.94, -10.21) * mm, "end": v(19.89, -10.57) * mm});
            skLineSegment(sketch, "E360", {"start": v(19.89, -10.57) * mm, "end": v(19.85, -10.93) * mm});
            skLineSegment(sketch, "E361", {"start": v(19.85, -10.93) * mm, "end": v(19.78, -11.28) * mm});
            skLineSegment(sketch, "E362", {"start": v(19.78, -11.28) * mm, "end": v(19.64, -11.58) * mm});
            skLineSegment(sketch, "E363", {"start": v(19.64, -11.58) * mm, "end": v(18.24, -13.56) * mm});
            skLineSegment(sketch, "E364", {"start": v(18.24, -13.56) * mm, "end": v(16.69, -15.38) * mm});
            skLineSegment(sketch, "E365", {"start": v(16.69, -15.38) * mm, "end": v(14.91, -16.97) * mm});
            skLineSegment(sketch, "E366", {"start": v(14.91, -16.97) * mm, "end": v(12.83, -18.26) * mm});
            skLineSegment(sketch, "E367", {"start": v(12.83, -18.26) * mm, "end": v(11.54, -18.8) * mm});
            skLineSegment(sketch, "E368", {"start": v(11.54, -18.8) * mm, "end": v(10.22, -19.2) * mm});
            skLineSegment(sketch, "E369", {"start": v(10.22, -19.2) * mm, "end": v(8.86, -19.4) * mm});
            skLineSegment(sketch, "E370", {"start": v(8.86, -19.4) * mm, "end": v(7.45, -19.42) * mm});
            skLineSegment(sketch, "E371", {"start": v(7.45, -19.42) * mm, "end": v(7.02, -19.43) * mm});
            skLineSegment(sketch, "E372", {"start": v(7.02, -19.43) * mm, "end": v(6.75, -19.55) * mm});
            skLineSegment(sketch, "E373", {"start": v(6.75, -19.55) * mm, "end": v(6.59, -19.83) * mm});
            skLineSegment(sketch, "E374", {"start": v(6.59, -19.83) * mm, "end": v(6.52, -20.28) * mm});
            skLineSegment(sketch, "E375", {"start": v(6.52, -20.28) * mm, "end": v(6.39, -22.12) * mm});
            skLineSegment(sketch, "E376", {"start": v(6.39, -22.12) * mm, "end": v(6.27, -23.95) * mm});
            skLineSegment(sketch, "E377", {"start": v(6.27, -23.95) * mm, "end": v(6.16, -25.8) * mm});
            skLineSegment(sketch, "E378", {"start": v(6.16, -25.8) * mm, "end": v(6.1, -27.63) * mm});
            skLineSegment(sketch, "E379", {"start": v(6.1, -27.63) * mm, "end": v(5.84, -28.62) * mm});
            skLineSegment(sketch, "E380", {"start": v(5.84, -28.62) * mm, "end": v(5.22, -29.2) * mm});
            skLineSegment(sketch, "E381", {"start": v(5.22, -29.2) * mm, "end": v(4.42, -29.38) * mm});
            skLineSegment(sketch, "E382", {"start": v(4.42, -29.38) * mm, "end": v(3.6, -29.15) * mm});
            skLineSegment(sketch, "E383", {"start": v(3.6, -29.15) * mm, "end": v(2.65, -28.62) * mm});
            skLineSegment(sketch, "E384", {"start": v(2.65, -28.62) * mm, "end": v(1.68, -28.11) * mm});
            skLineSegment(sketch, "E385", {"start": v(1.68, -28.11) * mm, "end": v(0.72, -27.6) * mm});
            skLineSegment(sketch, "E386", {"start": v(0.72, -27.6) * mm, "end": v(-0.23, -27.05) * mm});
            skLineSegment(sketch, "E387", {"start": v(-0.23, -27.05) * mm, "end": v(-1.3, -26.25) * mm});
            skLineSegment(sketch, "E388", {"start": v(-1.3, -26.25) * mm, "end": v(-2.19, -25.3) * mm});
            skLineSegment(sketch, "E389", {"start": v(-2.19, -25.3) * mm, "end": v(-2.94, -24.22) * mm});
            skLineSegment(sketch, "E390", {"start": v(-2.94, -24.22) * mm, "end": v(-3.58, -23.06) * mm});
            skLineSegment(sketch, "E391", {"start": v(-3.58, -23.06) * mm, "end": v(-3.7, -22.5) * mm});
            skLineSegment(sketch, "E392", {"start": v(-3.7, -22.5) * mm, "end": v(-3.5, -22) * mm});
            skLineSegment(sketch, "E393", {"start": v(-3.5, -22) * mm, "end": v(-3.08, -21.63) * mm});
            skLineSegment(sketch, "E394", {"start": v(-3.08, -21.63) * mm, "end": v(-2.45, -21.48) * mm});
            skLineSegment(sketch, "E395", {"start": v(-2.45, -21.48) * mm, "end": v(-1.72, -21.49) * mm});
            skLineSegment(sketch, "E396", {"start": v(-1.72, -21.49) * mm, "end": v(-1, -21.59) * mm});
            skLineSegment(sketch, "E397", {"start": v(-1, -21.59) * mm, "end": v(-0.3, -21.8) * mm});
            skLineSegment(sketch, "E398", {"start": v(-0.3, -21.8) * mm, "end": v(0.37, -22.1) * mm});
            skLineSegment(sketch, "E399", {"start": v(0.37, -22.1) * mm, "end": v(0.84, -22.3) * mm});
            skLineSegment(sketch, "E400", {"start": v(0.84, -22.3) * mm, "end": v(1.19, -22.29) * mm});
            skLineSegment(sketch, "E401", {"start": v(1.19, -22.29) * mm, "end": v(1.44, -22.04) * mm});
            skLineSegment(sketch, "E402", {"start": v(1.44, -22.04) * mm, "end": v(1.61, -21.56) * mm});
            skLineSegment(sketch, "E403", {"start": v(1.61, -21.56) * mm, "end": v(1.65, -21.38) * mm});
            skLineSegment(sketch, "E404", {"start": v(1.65, -21.38) * mm, "end": v(1.67, -21.2) * mm});
            skLineSegment(sketch, "E405", {"start": v(1.67, -21.2) * mm, "end": v(1.69, -21.03) * mm});
            skLineSegment(sketch, "E406", {"start": v(1.69, -21.03) * mm, "end": v(1.7, -20.85) * mm});
            skLineSegment(sketch, "E407", {"start": v(1.7, -20.85) * mm, "end": v(1.6, -20.34) * mm});
            skLineSegment(sketch, "E408", {"start": v(1.6, -20.34) * mm, "end": v(1.34, -20) * mm});
            skLineSegment(sketch, "E409", {"start": v(1.34, -20) * mm, "end": v(0.94, -19.84) * mm});
            skLineSegment(sketch, "E410", {"start": v(0.94, -19.84) * mm, "end": v(0.42, -19.86) * mm});
            skLineSegment(sketch, "E411", {"start": v(0.42, -19.86) * mm, "end": v(-0.18, -20.02) * mm});
            skLineSegment(sketch, "E412", {"start": v(-0.18, -20.02) * mm, "end": v(-0.78, -20.18) * mm});
            skLineSegment(sketch, "E413", {"start": v(-0.78, -20.18) * mm, "end": v(-1.38, -20.31) * mm});
            skLineSegment(sketch, "E414", {"start": v(-1.38, -20.31) * mm, "end": v(-1.97, -20.37) * mm});
            skLineSegment(sketch, "E415", {"start": v(-1.97, -20.37) * mm, "end": v(-3.08, -20.35) * mm});
            skLineSegment(sketch, "E416", {"start": v(-3.08, -20.35) * mm, "end": v(-4.18, -20.28) * mm});
            skLineSegment(sketch, "E417", {"start": v(-4.18, -20.28) * mm, "end": v(-5.28, -20.19) * mm});
            skLineSegment(sketch, "E418", {"start": v(-5.28, -20.19) * mm, "end": v(-6.39, -20.1) * mm});
            skLineSegment(sketch, "E419", {"start": v(-6.39, -20.1) * mm, "end": v(-6.82, -20.06) * mm});
            skLineSegment(sketch, "E420", {"start": v(-6.82, -20.06) * mm, "end": v(-7.25, -20.02) * mm});
            skLineSegment(sketch, "E421", {"start": v(-7.25, -20.02) * mm, "end": v(-7.68, -19.98) * mm});
            skLineSegment(sketch, "E422", {"start": v(-7.68, -19.98) * mm, "end": v(-8.12, -19.96) * mm});
            skLineSegment(sketch, "E423", {"start": v(-8.12, -19.96) * mm, "end": v(-8.45, -20.01) * mm});
            skLineSegment(sketch, "E424", {"start": v(-8.45, -20.01) * mm, "end": v(-8.72, -20.17) * mm});
            skLineSegment(sketch, "E425", {"start": v(-8.72, -20.17) * mm, "end": v(-8.9, -20.42) * mm});
            skLineSegment(sketch, "E426", {"start": v(-8.9, -20.42) * mm, "end": v(-8.98, -20.73) * mm});
            skLineSegment(sketch, "E427", {"start": v(-8.98, -20.73) * mm, "end": v(-9.4, -22.64) * mm});
            skLineSegment(sketch, "E428", {"start": v(-9.4, -22.64) * mm, "end": v(-10.13, -24.44) * mm});
            skLineSegment(sketch, "E429", {"start": v(-10.13, -24.44) * mm, "end": v(-10.95, -26.2) * mm});
            skLineSegment(sketch, "E430", {"start": v(-10.95, -26.2) * mm, "end": v(-11.7, -28) * mm});
            skLineSegment(sketch, "E431", {"start": v(-11.7, -28) * mm, "end": v(-11.98, -28.54) * mm});
            skLineSegment(sketch, "E432", {"start": v(-11.98, -28.54) * mm, "end": v(-12.4, -29.04) * mm});
            skLineSegment(sketch, "E433", {"start": v(-12.4, -29.04) * mm, "end": v(-12.87, -29.51) * mm});
            skLineSegment(sketch, "E434", {"start": v(-12.87, -29.51) * mm, "end": v(-13.32, -30) * mm});
            skLineSegment(sketch, "E435", {"start": v(-13.32, -30) * mm, "end": v(-13.53, -30) * mm});
            skLineSegment(sketch, "E436", {"start": v(-13.53, -30) * mm, "end": v(-13.74, -30) * mm});
            skLineSegment(sketch, "E437", {"start": v(-13.74, -30) * mm, "end": v(-13.95, -30) * mm});
            skLineSegment(sketch, "E438", {"start": v(-13.95, -30) * mm, "end": v(-14.16, -30) * mm});
            skLineSegment(sketch, "E439", {"start": v(-14.16, -30) * mm, "end": v(-14.2, -29.98) * mm});
            skLineSegment(sketch, "E440", {"start": v(-14.2, -29.98) * mm, "end": v(-14.23, -29.95) * mm});
            skLineSegment(sketch, "E441", {"start": v(-14.23, -29.95) * mm, "end": v(-14.27, -29.93) * mm});
            skLineSegment(sketch, "E442", {"start": v(-14.27, -29.93) * mm, "end": v(-14.3, -29.9) * mm});
            skLineSegment(sketch, "E443", {"start": v(-14.3, -29.9) * mm, "end": v(-16.22, -28.9) * mm});
            skLineSegment(sketch, "E444", {"start": v(-16.22, -28.9) * mm, "end": v(-17.84, -27.6) * mm});
            skLineSegment(sketch, "E445", {"start": v(-17.84, -27.6) * mm, "end": v(-19.17, -26) * mm});
            skLineSegment(sketch, "E446", {"start": v(-19.17, -26) * mm, "end": v(-20.2, -24.08) * mm});
            skLineSegment(sketch, "E447", {"start": v(-20.2, -24.08) * mm, "end": v(-20.34, -23.32) * mm});
            skLineSegment(sketch, "E448", {"start": v(-20.34, -23.32) * mm, "end": v(-20.15, -22.74) * mm});
            skLineSegment(sketch, "E449", {"start": v(-20.15, -22.74) * mm, "end": v(-19.65, -22.37) * mm});
            skLineSegment(sketch, "E450", {"start": v(-19.65, -22.37) * mm, "end": v(-18.87, -22.28) * mm});
            skLineSegment(sketch, "E451", {"start": v(-18.87, -22.28) * mm, "end": v(-18.15, -22.38) * mm});
            skLineSegment(sketch, "E452", {"start": v(-18.15, -22.38) * mm, "end": v(-17.47, -22.6) * mm});
            skLineSegment(sketch, "E453", {"start": v(-17.47, -22.6) * mm, "end": v(-16.83, -22.9) * mm});
            skLineSegment(sketch, "E454", {"start": v(-16.83, -22.9) * mm, "end": v(-16.22, -23.29) * mm});
            skLineSegment(sketch, "E455", {"start": v(-16.22, -23.29) * mm, "end": v(-15.99, -23.47) * mm});
            skLineSegment(sketch, "E456", {"start": v(-15.99, -23.47) * mm, "end": v(-15.75, -23.66) * mm});
            skLineSegment(sketch, "E457", {"start": v(-15.75, -23.66) * mm, "end": v(-15.52, -23.85) * mm});
            skLineSegment(sketch, "E458", {"start": v(-15.52, -23.85) * mm, "end": v(-15.28, -24.03) * mm});
            skLineSegment(sketch, "E459", {"start": v(-15.28, -24.03) * mm, "end": v(-14.93, -24.19) * mm});
            skLineSegment(sketch, "E460", {"start": v(-14.93, -24.19) * mm, "end": v(-14.62, -24.16) * mm});
            skLineSegment(sketch, "E461", {"start": v(-14.62, -24.16) * mm, "end": v(-14.36, -23.97) * mm});
            skLineSegment(sketch, "E462", {"start": v(-14.36, -23.97) * mm, "end": v(-14.18, -23.62) * mm});
            skLineSegment(sketch, "E463", {"start": v(-14.18, -23.62) * mm, "end": v(-13.87, -22.7) * mm});
            skLineSegment(sketch, "E464", {"start": v(-13.87, -22.7) * mm, "end": v(-13.56, -21.78) * mm});
            skLineSegment(sketch, "E465", {"start": v(-13.56, -21.78) * mm, "end": v(-13.24, -20.87) * mm});
            skLineSegment(sketch, "E466", {"start": v(-13.24, -20.87) * mm, "end": v(-12.9, -19.96) * mm});
            skLineSegment(sketch, "E467", {"start": v(-12.9, -19.96) * mm, "end": v(-12.69, -19.33) * mm});
            skLineSegment(sketch, "E468", {"start": v(-12.69, -19.33) * mm, "end": v(-12.66, -18.96) * mm});
            skLineSegment(sketch, "E469", {"start": v(-12.66, -18.96) * mm, "end": v(-12.9, -18.68) * mm});
            skLineSegment(sketch, "E470", {"start": v(-12.9, -18.68) * mm, "end": v(-13.48, -18.35) * mm});
            skLineSegment(sketch, "E471", {"start": v(-13.48, -18.35) * mm, "end": v(-13.92, -18.12) * mm});
            skLineSegment(sketch, "E472", {"start": v(-13.92, -18.12) * mm, "end": v(-14.36, -17.9) * mm});
            skLineSegment(sketch, "E473", {"start": v(-14.36, -17.9) * mm, "end": v(-14.8, -17.66) * mm});
            skLineSegment(sketch, "E474", {"start": v(-14.8, -17.66) * mm, "end": v(-15.22, -17.42) * mm});
            skLineSegment(sketch, "E475", {"start": v(-15.22, -17.42) * mm, "end": v(-15.94, -16.99) * mm});
            skLineSegment(sketch, "E476", {"start": v(-15.94, -16.99) * mm, "end": v(-16.66, -16.56) * mm});
            skLineSegment(sketch, "E477", {"start": v(-16.66, -16.56) * mm, "end": v(-17.36, -16.1) * mm});
            skLineSegment(sketch, "E478", {"start": v(-17.36, -16.1) * mm, "end": v(-18.02, -15.6) * mm});
            skLineSegment(sketch, "E479", {"start": v(-18.02, -15.6) * mm, "end": v(-20.82, -12.7) * mm});
            skLineSegment(sketch, "E480", {"start": v(-20.82, -12.7) * mm, "end": v(-22.94, -9.4) * mm});
            skLineSegment(sketch, "E481", {"start": v(-22.94, -9.4) * mm, "end": v(-24.53, -5.81) * mm});
            skLineSegment(sketch, "E482", {"start": v(-24.53, -5.81) * mm, "end": v(-25.75, -2.02) * mm});
            skLineSegment(sketch, "E483", {"start": v(-25.75, -2.02) * mm, "end": v(-26.07, -1) * mm});
            skLineSegment(sketch, "E484", {"start": v(-26.07, -1) * mm, "end": v(-26.38, 0.02) * mm});
            skLineSegment(sketch, "E485", {"start": v(-26.38, 0.02) * mm, "end": v(-26.6, 1.07) * mm});
            skLineSegment(sketch, "E486", {"start": v(-26.6, 1.07) * mm, "end": v(-26.67, 2.16) * mm});
            skLineSegment(sketch, "E487", {"start": v(-26.67, 2.16) * mm, "end": v(-26.65, 3.26) * mm});
            skLineSegment(sketch, "E488", {"start": v(-26.65, 3.26) * mm, "end": v(-26.67, 4.37) * mm});
            skLineSegment(sketch, "E489", {"start": v(-26.67, 4.37) * mm, "end": v(-26.7, 5.47) * mm});
            skLineSegment(sketch, "E490", {"start": v(-26.7, 5.47) * mm, "end": v(-26.74, 6.57) * mm});
            skLineSegment(sketch, "E491", {"start": v(-26.74, 6.57) * mm, "end": v(-26.77, 7.27) * mm});
            skLineSegment(sketch, "E492", {"start": v(-26.77, 7.27) * mm, "end": v(-26.8, 7.97) * mm});
            skLineSegment(sketch, "E493", {"start": v(-26.8, 7.97) * mm, "end": v(-26.82, 8.67) * mm});
            skLineSegment(sketch, "E494", {"start": v(-26.82, 8.67) * mm, "end": v(-26.84, 9.37) * mm});
            skLineSegment(sketch, "E495", {"start": v(-26.84, 9.37) * mm, "end": v(-26.85, 9.43) * mm});
            skLineSegment(sketch, "E496", {"start": v(-26.85, 9.43) * mm, "end": v(-26.85, 9.5) * mm});
            skLineSegment(sketch, "E497", {"start": v(-26.85, 9.5) * mm, "end": v(-26.85, 9.55) * mm});
            skLineSegment(sketch, "E498", {"start": v(-26.85, 9.55) * mm, "end": v(-26.84, 9.6) * mm});
            skLineSegment(sketch, "E499", {"start": v(-26.84, 9.6) * mm, "end": v(-26.69, 10.7) * mm});
            skLineSegment(sketch, "E500", {"start": v(-26.69, 10.7) * mm, "end": v(-26.53, 11.8) * mm});
            skLineSegment(sketch, "E501", {"start": v(-26.53, 11.8) * mm, "end": v(-26.37, 12.9) * mm});
            skLineSegment(sketch, "E502", {"start": v(-26.37, 12.9) * mm, "end": v(-26.22, 14) * mm});
            skLineSegment(sketch, "E503", {"start": v(-26.22, 14) * mm, "end": v(-26.1, 14.83) * mm});
            skLineSegment(sketch, "E504", {"start": v(-26.1, 14.83) * mm, "end": v(-25.98, 15.67) * mm});
            skLineSegment(sketch, "E505", {"start": v(-25.98, 15.67) * mm, "end": v(-25.97, 16.53) * mm});
            skLineSegment(sketch, "E506", {"start": v(-25.97, 16.53) * mm, "end": v(-26.15, 17.4) * mm});
            skLineSegment(sketch, "E507", {"start": v(-26.15, 17.4) * mm, "end": v(-26.28, 18.43) * mm});
            skLineSegment(sketch, "E508", {"start": v(-26.28, 18.43) * mm, "end": v(-26.04, 19.45) * mm});
            skLineSegment(sketch, "E509", {"start": v(-26.04, 19.45) * mm, "end": v(-25.49, 20.35) * mm});
            skLineSegment(sketch, "E510", {"start": v(-25.49, 20.35) * mm, "end": v(-24.68, 21.04) * mm});
            skLineSegment(sketch, "E511", {"start": v(-24.68, 21.04) * mm, "end": v(-24.03, 21.49) * mm});
            skLineSegment(sketch, "E512", {"start": v(-24.03, 21.49) * mm, "end": v(-23.45, 22) * mm});
            skLineSegment(sketch, "E513", {"start": v(-23.45, 22) * mm, "end": v(-22.92, 22.56) * mm});
            skLineSegment(sketch, "E514", {"start": v(-22.92, 22.56) * mm, "end": v(-22.44, 23.16) * mm});
            skLineSegment(sketch, "E515", {"start": v(-22.44, 23.16) * mm, "end": v(-20.85, 25.02) * mm});
            skLineSegment(sketch, "E516", {"start": v(-20.85, 25.02) * mm, "end": v(-19.08, 26.65) * mm});
            skLineSegment(sketch, "E517", {"start": v(-19.08, 26.65) * mm, "end": v(-17.12, 28.05) * mm});
            skLineSegment(sketch, "E518", {"start": v(-17.12, 28.05) * mm, "end": v(-14.98, 29.18) * mm});
            skLineSegment(sketch, "E519", {"start": v(-14.96, 29.2) * mm, "end": v(-14.38, 29.42) * mm});
            skLineSegment(sketch, "E520", {"start": v(-14.38, 29.42) * mm, "end": v(-13.8, 29.62) * mm});
            skLineSegment(sketch, "E521", {"start": v(-13.8, 29.62) * mm, "end": v(-13.2, 29.8) * mm});
            skLineSegment(sketch, "E522", {"start": v(-13.2, 29.8) * mm, "end": v(-12.6, 30) * mm});
            skLineSegment(sketch, "E523", {"start": v(-12.6, 30) * mm, "end": v(-11.88, 30) * mm});
            skLineSegment(sketch, "E524", {"start": v(-11.88, 30) * mm, "end": v(-11.16, 30) * mm});
            skLineSegment(sketch, "E525", {"start": v(-11.16, 30) * mm, "end": v(-10.44, 30) * mm});
            skLineSegment(sketch, "E526", {"start": v(-10.44, 30) * mm, "end": v(-9.72, 30) * mm});
            skLineSegment(sketch, "E527", {"start": v(-20.27, 15.72) * mm, "end": v(-21.02, 15.72) * mm});
            skLineSegment(sketch, "E528", {"start": v(-21.02, 15.72) * mm, "end": v(-21.76, 15.72) * mm});
            skLineSegment(sketch, "E529", {"start": v(-21.76, 15.72) * mm, "end": v(-22.48, 15.72) * mm});
            skLineSegment(sketch, "E530", {"start": v(-22.48, 15.72) * mm, "end": v(-23.2, 15.73) * mm});
            skLineSegment(sketch, "E531", {"start": v(-23.2, 15.73) * mm, "end": v(-23.65, 15.68) * mm});
            skLineSegment(sketch, "E532", {"start": v(-23.65, 15.68) * mm, "end": v(-24, 15.53) * mm});
            skLineSegment(sketch, "E533", {"start": v(-24, 15.53) * mm, "end": v(-24.23, 15.24) * mm});
            skLineSegment(sketch, "E534", {"start": v(-24.23, 15.24) * mm, "end": v(-24.36, 14.8) * mm});
            skLineSegment(sketch, "E535", {"start": v(-24.36, 14.8) * mm, "end": v(-24.44, 14.33) * mm});
            skLineSegment(sketch, "E536", {"start": v(-24.44, 14.33) * mm, "end": v(-24.52, 13.86) * mm});
            skLineSegment(sketch, "E537", {"start": v(-24.52, 13.86) * mm, "end": v(-24.59, 13.39) * mm});
            skLineSegment(sketch, "E538", {"start": v(-24.59, 13.39) * mm, "end": v(-24.65, 12.91) * mm});
            skLineSegment(sketch, "E539", {"start": v(-24.65, 12.91) * mm, "end": v(-24.67, 12.36) * mm});
            skLineSegment(sketch, "E540", {"start": v(-24.67, 12.36) * mm, "end": v(-24.52, 12.03) * mm});
            skLineSegment(sketch, "E541", {"start": v(-24.52, 12.03) * mm, "end": v(-24.18, 11.9) * mm});
            skLineSegment(sketch, "E542", {"start": v(-24.18, 11.9) * mm, "end": v(-23.63, 11.93) * mm});
            skLineSegment(sketch, "E543", {"start": v(-23.63, 11.93) * mm, "end": v(-22.98, 12.03) * mm});
            skLineSegment(sketch, "E544", {"start": v(-22.98, 12.03) * mm, "end": v(-22.33, 12.12) * mm});
            skLineSegment(sketch, "E545", {"start": v(-22.33, 12.12) * mm, "end": v(-21.67, 12.18) * mm});
            skLineSegment(sketch, "E546", {"start": v(-21.67, 12.18) * mm, "end": v(-21.02, 12.2) * mm});
            skLineSegment(sketch, "E547", {"start": v(-21.02, 12.2) * mm, "end": v(-18.57, 12.2) * mm});
            skLineSegment(sketch, "E548", {"start": v(-18.57, 12.2) * mm, "end": v(-16.14, 12.34) * mm});
            skLineSegment(sketch, "E549", {"start": v(-16.14, 12.34) * mm, "end": v(-13.72, 12.6) * mm});
            skLineSegment(sketch, "E550", {"start": v(-13.72, 12.6) * mm, "end": v(-11.3, 12.93) * mm});
            skLineSegment(sketch, "E551", {"start": v(-11.3, 12.93) * mm, "end": v(-9.98, 13.14) * mm});
            skLineSegment(sketch, "E552", {"start": v(-9.98, 13.14) * mm, "end": v(-8.67, 13.35) * mm});
            skLineSegment(sketch, "E553", {"start": v(-8.67, 13.35) * mm, "end": v(-7.35, 13.55) * mm});
            skLineSegment(sketch, "E554", {"start": v(-7.35, 13.55) * mm, "end": v(-6.03, 13.74) * mm});
            skLineSegment(sketch, "E555", {"start": v(-6.03, 13.74) * mm, "end": v(-5.82, 13.73) * mm});
            skLineSegment(sketch, "E556", {"start": v(-5.82, 13.73) * mm, "end": v(-5.58, 13.64) * mm});
            skLineSegment(sketch, "E557", {"start": v(-5.58, 13.64) * mm, "end": v(-5.37, 13.5) * mm});
            skLineSegment(sketch, "E558", {"start": v(-5.37, 13.5) * mm, "end": v(-5.24, 13.34) * mm});
            skLineSegment(sketch, "E559", {"start": v(-5.24, 13.34) * mm, "end": v(-5.21, 13.17) * mm});
            skLineSegment(sketch, "E560", {"start": v(-5.21, 13.17) * mm, "end": v(-5.26, 12.95) * mm});
            skLineSegment(sketch, "E561", {"start": v(-5.26, 12.95) * mm, "end": v(-5.37, 12.72) * mm});
            skLineSegment(sketch, "E562", {"start": v(-5.37, 12.72) * mm, "end": v(-5.5, 12.53) * mm});
            skLineSegment(sketch, "E563", {"start": v(-5.5, 12.53) * mm, "end": v(-5.63, 12.41) * mm});
            skLineSegment(sketch, "E564", {"start": v(-5.63, 12.41) * mm, "end": v(-5.8, 12.33) * mm});
            skLineSegment(sketch, "E565", {"start": v(-5.8, 12.33) * mm, "end": v(-6, 12.27) * mm});
            skLineSegment(sketch, "E566", {"start": v(-6, 12.27) * mm, "end": v(-6.2, 12.24) * mm});
            skLineSegment(sketch, "E567", {"start": v(-6.2, 12.24) * mm, "end": v(-7.76, 11.98) * mm});
            skLineSegment(sketch, "E568", {"start": v(-7.76, 11.98) * mm, "end": v(-9.33, 11.73) * mm});
            skLineSegment(sketch, "E569", {"start": v(-9.33, 11.73) * mm, "end": v(-10.9, 11.5) * mm});
            skLineSegment(sketch, "E570", {"start": v(-10.9, 11.5) * mm, "end": v(-12.47, 11.3) * mm});
            skLineSegment(sketch, "E571", {"start": v(-12.47, 11.3) * mm, "end": v(-13.78, 11.16) * mm});
            skLineSegment(sketch, "E572", {"start": v(-13.78, 11.16) * mm, "end": v(-15.1, 11.06) * mm});
            skLineSegment(sketch, "E573", {"start": v(-15.1, 11.06) * mm, "end": v(-16.4, 11) * mm});
            skLineSegment(sketch, "E574", {"start": v(-16.4, 11) * mm, "end": v(-17.72, 10.93) * mm});
            skLineSegment(sketch, "E575", {"start": v(-17.72, 10.93) * mm, "end": v(-19.34, 10.86) * mm});
            skLineSegment(sketch, "E576", {"start": v(-19.34, 10.86) * mm, "end": v(-20.96, 10.81) * mm});
            skLineSegment(sketch, "E577", {"start": v(-20.96, 10.81) * mm, "end": v(-22.58, 10.77) * mm});
            skLineSegment(sketch, "E578", {"start": v(-22.58, 10.77) * mm, "end": v(-24.2, 10.73) * mm});
            skLineSegment(sketch, "E579", {"start": v(-24.2, 10.73) * mm, "end": v(-24.72, 10.68) * mm});
            skLineSegment(sketch, "E580", {"start": v(-24.72, 10.68) * mm, "end": v(-25.02, 10.53) * mm});
            skLineSegment(sketch, "E581", {"start": v(-25.02, 10.53) * mm, "end": v(-25.17, 10.22) * mm});
            skLineSegment(sketch, "E582", {"start": v(-25.17, 10.22) * mm, "end": v(-25.2, 9.7) * mm});
            skLineSegment(sketch, "E583", {"start": v(-25.2, 9.7) * mm, "end": v(-25.16, 8.3) * mm});
            skLineSegment(sketch, "E584", {"start": v(-25.16, 8.3) * mm, "end": v(-25.1, 6.9) * mm});
            skLineSegment(sketch, "E585", {"start": v(-25.1, 6.9) * mm, "end": v(-25.08, 5.5) * mm});
            skLineSegment(sketch, "E586", {"start": v(-25.08, 5.5) * mm, "end": v(-25.12, 4.1) * mm});
            skLineSegment(sketch, "E587", {"start": v(-25.12, 4.1) * mm, "end": v(-25.14, 3) * mm});
            skLineSegment(sketch, "E588", {"start": v(-25.14, 3) * mm, "end": v(-25.1, 1.91) * mm});
            skLineSegment(sketch, "E589", {"start": v(-25.1, 1.91) * mm, "end": v(-24.96, 0.84) * mm});
            skLineSegment(sketch, "E590", {"start": v(-24.96, 0.84) * mm, "end": v(-24.76, -0.23) * mm});
            skLineSegment(sketch, "E591", {"start": v(-24.76, -0.23) * mm, "end": v(-24.05, -2.84) * mm});
            skLineSegment(sketch, "E592", {"start": v(-24.05, -2.84) * mm, "end": v(-23.1, -5.36) * mm});
            skLineSegment(sketch, "E593", {"start": v(-23.1, -5.36) * mm, "end": v(-21.98, -7.8) * mm});
            skLineSegment(sketch, "E594", {"start": v(-21.98, -7.8) * mm, "end": v(-20.72, -10.19) * mm});
            skLineSegment(sketch, "E595", {"start": v(-20.72, -10.19) * mm, "end": v(-19.44, -12.1) * mm});
            skLineSegment(sketch, "E596", {"start": v(-19.44, -12.1) * mm, "end": v(-17.91, -13.74) * mm});
            skLineSegment(sketch, "E597", {"start": v(-17.91, -13.74) * mm, "end": v(-16.15, -15.11) * mm});
            skLineSegment(sketch, "E598", {"start": v(-16.15, -15.11) * mm, "end": v(-14.16, -16.22) * mm});
            skLineSegment(sketch, "E599", {"start": v(-14.16, -16.22) * mm, "end": v(-11.91, -17.12) * mm});
            skLineSegment(sketch, "E600", {"start": v(-11.91, -17.12) * mm, "end": v(-9.6, -17.8) * mm});
            skLineSegment(sketch, "E601", {"start": v(-9.6, -17.8) * mm, "end": v(-7.22, -18.32) * mm});
            skLineSegment(sketch, "E602", {"start": v(-7.22, -18.32) * mm, "end": v(-4.82, -18.72) * mm});
            skLineSegment(sketch, "E603", {"start": v(-4.82, -18.72) * mm, "end": v(-4.3, -18.8) * mm});
            skLineSegment(sketch, "E604", {"start": v(-4.3, -18.8) * mm, "end": v(-3.78, -18.87) * mm});
            skLineSegment(sketch, "E605", {"start": v(-3.78, -18.87) * mm, "end": v(-3.26, -18.91) * mm});
            skLineSegment(sketch, "E606", {"start": v(-3.26, -18.91) * mm, "end": v(-2.75, -18.9) * mm});
            skLineSegment(sketch, "E607", {"start": v(-2.75, -18.9) * mm, "end": v(-1.64, -18.74) * mm});
            skLineSegment(sketch, "E608", {"start": v(-1.64, -18.74) * mm, "end": v(-0.53, -18.55) * mm});
            skLineSegment(sketch, "E609", {"start": v(-0.53, -18.55) * mm, "end": v(0.57, -18.35) * mm});
            skLineSegment(sketch, "E610", {"start": v(0.57, -18.35) * mm, "end": v(1.68, -18.15) * mm});
            skLineSegment(sketch, "E611", {"start": v(1.68, -18.15) * mm, "end": v(2.3, -18.13) * mm});
            skLineSegment(sketch, "E612", {"start": v(2.3, -18.13) * mm, "end": v(2.73, -18.32) * mm});
            skLineSegment(sketch, "E613", {"start": v(2.73, -18.32) * mm, "end": v(3, -18.72) * mm});
            skLineSegment(sketch, "E614", {"start": v(3, -18.72) * mm, "end": v(3.1, -19.33) * mm});
            skLineSegment(sketch, "E615", {"start": v(3.1, -19.33) * mm, "end": v(3.11, -20.34) * mm});
            skLineSegment(sketch, "E616", {"start": v(3.11, -20.34) * mm, "end": v(3.12, -21.34) * mm});
            skLineSegment(sketch, "E617", {"start": v(3.12, -21.34) * mm, "end": v(3.12, -22.35) * mm});
            skLineSegment(sketch, "E618", {"start": v(3.12, -22.35) * mm, "end": v(3.13, -23.35) * mm});
            skLineSegment(sketch, "E619", {"start": v(3.13, -23.35) * mm, "end": v(3.02, -24.01) * mm});
            skLineSegment(sketch, "E620", {"start": v(3.02, -24.01) * mm, "end": v(2.72, -24.4) * mm});
            skLineSegment(sketch, "E621", {"start": v(2.72, -24.4) * mm, "end": v(2.24, -24.48) * mm});
            skLineSegment(sketch, "E622", {"start": v(2.24, -24.48) * mm, "end": v(1.62, -24.26) * mm});
            skLineSegment(sketch, "E623", {"start": v(1.62, -24.26) * mm, "end": v(1.03, -23.93) * mm});
            skLineSegment(sketch, "E624", {"start": v(1.03, -23.93) * mm, "end": v(0.45, -23.58) * mm});
            skLineSegment(sketch, "E625", {"start": v(0.45, -23.58) * mm, "end": v(-0.12, -23.24) * mm});
            skLineSegment(sketch, "E626", {"start": v(-0.12, -23.24) * mm, "end": v(-0.7, -22.9) * mm});
            skLineSegment(sketch, "E627", {"start": v(-0.7, -22.9) * mm, "end": v(-0.87, -22.84) * mm});
            skLineSegment(sketch, "E628", {"start": v(-0.87, -22.84) * mm, "end": v(-1.05, -22.8) * mm});
            skLineSegment(sketch, "E629", {"start": v(-1.05, -22.8) * mm, "end": v(-1.22, -22.8) * mm});
            skLineSegment(sketch, "E630", {"start": v(-1.22, -22.8) * mm, "end": v(-1.36, -22.84) * mm});
            skLineSegment(sketch, "E631", {"start": v(-1.36, -22.84) * mm, "end": v(-1.45, -22.95) * mm});
            skLineSegment(sketch, "E632", {"start": v(-1.45, -22.95) * mm, "end": v(-1.52, -23.12) * mm});
            skLineSegment(sketch, "E633", {"start": v(-1.52, -23.12) * mm, "end": v(-1.55, -23.3) * mm});
            skLineSegment(sketch, "E634", {"start": v(-1.55, -23.3) * mm, "end": v(-1.53, -23.46) * mm});
            skLineSegment(sketch, "E635", {"start": v(-1.53, -23.46) * mm, "end": v(-1.45, -23.7) * mm});
            skLineSegment(sketch, "E636", {"start": v(-1.45, -23.7) * mm, "end": v(-1.34, -23.93) * mm});
            skLineSegment(sketch, "E637", {"start": v(-1.34, -23.93) * mm, "end": v(-1.2, -24.14) * mm});
            skLineSegment(sketch, "E638", {"start": v(-1.2, -24.14) * mm, "end": v(-1.03, -24.31) * mm});
            skLineSegment(sketch, "E639", {"start": v(-1.03, -24.31) * mm, "end": v(0, -25.12) * mm});
            skLineSegment(sketch, "E640", {"start": v(0, -25.12) * mm, "end": v(1.05, -25.92) * mm});
            skLineSegment(sketch, "E641", {"start": v(1.05, -25.92) * mm, "end": v(2.1, -26.71) * mm});
            skLineSegment(sketch, "E642", {"start": v(2.1, -26.71) * mm, "end": v(3.17, -27.49) * mm});
            skLineSegment(sketch, "E643", {"start": v(3.17, -27.49) * mm, "end": v(3.63, -27.69) * mm});
            skLineSegment(sketch, "E644", {"start": v(3.63, -27.69) * mm, "end": v(4.04, -27.64) * mm});
            skLineSegment(sketch, "E645", {"start": v(4.04, -27.64) * mm, "end": v(4.37, -27.37) * mm});
            skLineSegment(sketch, "E646", {"start": v(4.37, -27.37) * mm, "end": v(4.58, -26.9) * mm});
            skLineSegment(sketch, "E647", {"start": v(4.58, -26.9) * mm, "end": v(4.62, -26.73) * mm});
            skLineSegment(sketch, "E648", {"start": v(4.62, -26.73) * mm, "end": v(4.64, -26.55) * mm});
            skLineSegment(sketch, "E649", {"start": v(4.64, -26.55) * mm, "end": v(4.66, -26.37) * mm});
            skLineSegment(sketch, "E650", {"start": v(4.66, -26.37) * mm, "end": v(4.67, -26.2) * mm});
            skLineSegment(sketch, "E651", {"start": v(4.67, -26.2) * mm, "end": v(4.7, -25.18) * mm});
            skLineSegment(sketch, "E652", {"start": v(4.7, -25.18) * mm, "end": v(4.71, -24.16) * mm});
            skLineSegment(sketch, "E653", {"start": v(4.71, -24.16) * mm, "end": v(4.73, -23.14) * mm});
            skLineSegment(sketch, "E654", {"start": v(4.73, -23.14) * mm, "end": v(4.74, -22.12) * mm});
            skLineSegment(sketch, "E655", {"start": v(4.74, -22.12) * mm, "end": v(4.74, -21.25) * mm});
            skLineSegment(sketch, "E656", {"start": v(4.74, -21.25) * mm, "end": v(4.75, -20.38) * mm});
            skLineSegment(sketch, "E657", {"start": v(4.75, -20.38) * mm, "end": v(4.75, -19.51) * mm});
            skLineSegment(sketch, "E658", {"start": v(4.75, -19.51) * mm, "end": v(4.73, -18.65) * mm});
            skLineSegment(sketch, "E659", {"start": v(4.73, -18.65) * mm, "end": v(4.8, -18.18) * mm});
            skLineSegment(sketch, "E660", {"start": v(4.8, -18.18) * mm, "end": v(5, -17.81) * mm});
            skLineSegment(sketch, "E661", {"start": v(5, -17.81) * mm, "end": v(5.34, -17.58) * mm});
            skLineSegment(sketch, "E662", {"start": v(5.34, -17.58) * mm, "end": v(5.8, -17.5) * mm});
            skLineSegment(sketch, "E663", {"start": v(5.8, -17.5) * mm, "end": v(5.97, -17.51) * mm});
            skLineSegment(sketch, "E664", {"start": v(5.97, -17.51) * mm, "end": v(6.13, -17.53) * mm});
            skLineSegment(sketch, "E665", {"start": v(6.13, -17.53) * mm, "end": v(6.3, -17.56) * mm});
            skLineSegment(sketch, "E666", {"start": v(6.3, -17.56) * mm, "end": v(6.45, -17.59) * mm});
            skLineSegment(sketch, "E667", {"start": v(6.45, -17.59) * mm, "end": v(8, -17.78) * mm});
            skLineSegment(sketch, "E668", {"start": v(8, -17.78) * mm, "end": v(9.53, -17.74) * mm});
            skLineSegment(sketch, "E669", {"start": v(9.53, -17.74) * mm, "end": v(11, -17.41) * mm});
            skLineSegment(sketch, "E670", {"start": v(11, -17.41) * mm, "end": v(12.43, -16.76) * mm});
            skLineSegment(sketch, "E671", {"start": v(12.43, -16.76) * mm, "end": v(13.95, -15.75) * mm});
            skLineSegment(sketch, "E672", {"start": v(13.95, -15.75) * mm, "end": v(15.34, -14.6) * mm});
            skLineSegment(sketch, "E673", {"start": v(15.34, -14.6) * mm, "end": v(16.59, -13.3) * mm});
            skLineSegment(sketch, "E674", {"start": v(16.59, -13.3) * mm, "end": v(17.68, -11.84) * mm});
            skLineSegment(sketch, "E675", {"start": v(17.68, -11.84) * mm, "end": v(18.63, -9.4) * mm});
            skLineSegment(sketch, "E676", {"start": v(18.63, -9.4) * mm, "end": v(18.47, -7.03) * mm});
            skLineSegment(sketch, "E677", {"start": v(18.47, -7.03) * mm, "end": v(17.26, -5.01) * mm});
            skLineSegment(sketch, "E678", {"start": v(17.26, -5.01) * mm, "end": v(15.08, -3.62) * mm});
            skLineSegment(sketch, "E679", {"start": v(15.08, -3.62) * mm, "end": v(13.82, -3.23) * mm});
            skLineSegment(sketch, "E680", {"start": v(13.82, -3.23) * mm, "end": v(12.52, -2.95) * mm});
            skLineSegment(sketch, "E681", {"start": v(12.52, -2.95) * mm, "end": v(11.2, -2.72) * mm});
            skLineSegment(sketch, "E682", {"start": v(11.2, -2.72) * mm, "end": v(9.9, -2.48) * mm});
            skLineSegment(sketch, "E683", {"start": v(9.9, -2.48) * mm, "end": v(9.63, -2.45) * mm});
            skLineSegment(sketch, "E684", {"start": v(9.63, -2.45) * mm, "end": v(9.36, -2.46) * mm});
            skLineSegment(sketch, "E685", {"start": v(9.36, -2.46) * mm, "end": v(9.09, -2.49) * mm});
            skLineSegment(sketch, "E686", {"start": v(9.09, -2.49) * mm, "end": v(8.82, -2.54) * mm});
            skLineSegment(sketch, "E687", {"start": v(8.82, -2.54) * mm, "end": v(7.61, -2.82) * mm});
            skLineSegment(sketch, "E688", {"start": v(7.61, -2.82) * mm, "end": v(6.44, -3.18) * mm});
            skLineSegment(sketch, "E689", {"start": v(6.44, -3.18) * mm, "end": v(5.34, -3.73) * mm});
            skLineSegment(sketch, "E690", {"start": v(5.34, -3.73) * mm, "end": v(4.38, -4.56) * mm});
            skLineSegment(sketch, "E691", {"start": v(4.38, -4.56) * mm, "end": v(4.33, -4.6) * mm});
            skLineSegment(sketch, "E692", {"start": v(4.33, -4.6) * mm, "end": v(4.29, -4.64) * mm});
            skLineSegment(sketch, "E693", {"start": v(4.29, -4.64) * mm, "end": v(4.23, -4.67) * mm});
            skLineSegment(sketch, "E694", {"start": v(4.23, -4.67) * mm, "end": v(4.18, -4.69) * mm});
            skLineSegment(sketch, "E695", {"start": v(4.18, -4.69) * mm, "end": v(4, -4.72) * mm});
            skLineSegment(sketch, "E696", {"start": v(4, -4.72) * mm, "end": v(3.81, -4.75) * mm});
            skLineSegment(sketch, "E697", {"start": v(3.81, -4.75) * mm, "end": v(3.65, -4.75) * mm});
            skLineSegment(sketch, "E698", {"start": v(3.65, -4.75) * mm, "end": v(3.54, -4.7) * mm});
            skLineSegment(sketch, "E699", {"start": v(3.54, -4.7) * mm, "end": v(3.47, -4.58) * mm});
            skLineSegment(sketch, "E700", {"start": v(3.47, -4.58) * mm, "end": v(3.44, -4.4) * mm});
            skLineSegment(sketch, "E701", {"start": v(3.44, -4.4) * mm, "end": v(3.44, -4.22) * mm});
            skLineSegment(sketch, "E702", {"start": v(3.44, -4.22) * mm, "end": v(3.47, -4.05) * mm});
            skLineSegment(sketch, "E703", {"start": v(3.47, -4.05) * mm, "end": v(3.51, -3.93) * mm});
            skLineSegment(sketch, "E704", {"start": v(3.51, -3.93) * mm, "end": v(3.6, -3.83) * mm});
            skLineSegment(sketch, "E705", {"start": v(3.6, -3.83) * mm, "end": v(3.7, -3.73) * mm});
            skLineSegment(sketch, "E706", {"start": v(3.7, -3.73) * mm, "end": v(3.8, -3.64) * mm});
            skLineSegment(sketch, "E707", {"start": v(3.8, -3.64) * mm, "end": v(4.07, -3.43) * mm});
            skLineSegment(sketch, "E708", {"start": v(4.07, -3.43) * mm, "end": v(4.35, -3.22) * mm});
            skLineSegment(sketch, "E709", {"start": v(4.35, -3.22) * mm, "end": v(4.63, -3.02) * mm});
            skLineSegment(sketch, "E710", {"start": v(4.63, -3.02) * mm, "end": v(4.9, -2.83) * mm});
            skLineSegment(sketch, "E711", {"start": v(4.9, -2.83) * mm, "end": v(5.38, -2.47) * mm});
            skLineSegment(sketch, "E712", {"start": v(5.38, -2.47) * mm, "end": v(5.54, -2.19) * mm});
            skLineSegment(sketch, "E713", {"start": v(5.54, -2.19) * mm, "end": v(5.42, -1.88) * mm});
            skLineSegment(sketch, "E714", {"start": v(5.42, -1.88) * mm, "end": v(5, -1.44) * mm});
            skLineSegment(sketch, "E715", {"start": v(5, -1.44) * mm, "end": v(4.92, -1.36) * mm});
            skLineSegment(sketch, "E716", {"start": v(4.92, -1.36) * mm, "end": v(4.83, -1.27) * mm});
            skLineSegment(sketch, "E717", {"start": v(4.83, -1.27) * mm, "end": v(4.74, -1.19) * mm});
            skLineSegment(sketch, "E718", {"start": v(4.74, -1.19) * mm, "end": v(4.68, -1.1) * mm});
            skLineSegment(sketch, "E719", {"start": v(4.68, -1.1) * mm, "end": v(4.63, -0.99) * mm});
            skLineSegment(sketch, "E720", {"start": v(4.63, -0.99) * mm, "end": v(4.6, -0.87) * mm});
            skLineSegment(sketch, "E721", {"start": v(4.6, -0.87) * mm, "end": v(4.58, -0.75) * mm});
            skLineSegment(sketch, "E722", {"start": v(4.58, -0.75) * mm, "end": v(4.6, -0.66) * mm});
            skLineSegment(sketch, "E723", {"start": v(4.6, -0.66) * mm, "end": v(4.67, -0.58) * mm});
            skLineSegment(sketch, "E724", {"start": v(4.67, -0.58) * mm, "end": v(4.77, -0.52) * mm});
            skLineSegment(sketch, "E725", {"start": v(4.77, -0.52) * mm, "end": v(4.89, -0.48) * mm});
            skLineSegment(sketch, "E726", {"start": v(4.89, -0.48) * mm, "end": v(5, -0.48) * mm});
            skLineSegment(sketch, "E727", {"start": v(5, -0.48) * mm, "end": v(5.28, -0.55) * mm});
            skLineSegment(sketch, "E728", {"start": v(5.28, -0.55) * mm, "end": v(5.57, -0.62) * mm});
            skLineSegment(sketch, "E729", {"start": v(5.57, -0.62) * mm, "end": v(5.85, -0.72) * mm});
            skLineSegment(sketch, "E730", {"start": v(5.85, -0.72) * mm, "end": v(6.12, -0.84) * mm});
            skLineSegment(sketch, "E731", {"start": v(6.12, -0.84) * mm, "end": v(7.1, -1.17) * mm});
            skLineSegment(sketch, "E732", {"start": v(7.1, -1.17) * mm, "end": v(8.05, -1.23) * mm});
            skLineSegment(sketch, "E733", {"start": v(8.05, -1.23) * mm, "end": v(9, -1.06) * mm});
            skLineSegment(sketch, "E734", {"start": v(9, -1.06) * mm, "end": v(9.93, -0.7) * mm});
            skLineSegment(sketch, "E735", {"start": v(9.93, -0.7) * mm, "end": v(10.26, -0.45) * mm});
            skLineSegment(sketch, "E736", {"start": v(10.26, -0.45) * mm, "end": v(10.53, -0.1) * mm});
            skLineSegment(sketch, "E737", {"start": v(10.53, -0.1) * mm, "end": v(10.67, 0.3) * mm});
            skLineSegment(sketch, "E738", {"start": v(10.67, 0.3) * mm, "end": v(10.67, 0.63) * mm});
            skLineSegment(sketch, "E739", {"start": v(10.67, 0.63) * mm, "end": v(10.48, 0.98) * mm});
            skLineSegment(sketch, "E740", {"start": v(10.48, 0.98) * mm, "end": v(10.19, 1.19) * mm});
            skLineSegment(sketch, "E741", {"start": v(10.19, 1.19) * mm, "end": v(9.84, 1.28) * mm});
            skLineSegment(sketch, "E742", {"start": v(9.84, 1.28) * mm, "end": v(9.46, 1.31) * mm});
            skLineSegment(sketch, "E743", {"start": v(9.46, 1.31) * mm, "end": v(8.8, 1.32) * mm});
            skLineSegment(sketch, "E744", {"start": v(8.8, 1.32) * mm, "end": v(8.14, 1.33) * mm});
            skLineSegment(sketch, "E745", {"start": v(8.14, 1.33) * mm, "end": v(7.48, 1.32) * mm});
            skLineSegment(sketch, "E746", {"start": v(7.48, 1.32) * mm, "end": v(6.82, 1.3) * mm});
            skLineSegment(sketch, "E747", {"start": v(6.82, 1.3) * mm, "end": v(5.42, 1.15) * mm});
            skLineSegment(sketch, "E748", {"start": v(5.42, 1.15) * mm, "end": v(4.1, 0.8) * mm});
            skLineSegment(sketch, "E749", {"start": v(4.1, 0.8) * mm, "end": v(2.84, 0.22) * mm});
            skLineSegment(sketch, "E750", {"start": v(2.84, 0.22) * mm, "end": v(1.66, -0.55) * mm});
            skLineSegment(sketch, "E751", {"start": v(1.66, -0.55) * mm, "end": v(1.3, -0.91) * mm});
            skLineSegment(sketch, "E752", {"start": v(1.3, -0.91) * mm, "end": v(1.06, -1.32) * mm});
            skLineSegment(sketch, "E753", {"start": v(1.06, -1.32) * mm, "end": v(0.96, -1.78) * mm});
            skLineSegment(sketch, "E754", {"start": v(0.96, -1.78) * mm, "end": v(1, -2.3) * mm});
            skLineSegment(sketch, "E755", {"start": v(1, -2.3) * mm, "end": v(1.01, -2.36) * mm});
            skLineSegment(sketch, "E756", {"start": v(1.01, -2.36) * mm, "end": v(1.04, -2.44) * mm});
            skLineSegment(sketch, "E757", {"start": v(1.04, -2.44) * mm, "end": v(1.06, -2.51) * mm});
            skLineSegment(sketch, "E758", {"start": v(1.06, -2.51) * mm, "end": v(1.06, -2.58) * mm});
            skLineSegment(sketch, "E759", {"start": v(1.06, -2.58) * mm, "end": v(1.03, -2.71) * mm});
            skLineSegment(sketch, "E760", {"start": v(1.03, -2.71) * mm, "end": v(1, -2.84) * mm});
            skLineSegment(sketch, "E761", {"start": v(1, -2.84) * mm, "end": v(0.95, -2.96) * mm});
            skLineSegment(sketch, "E762", {"start": v(0.95, -2.96) * mm, "end": v(0.88, -3.04) * mm});
            skLineSegment(sketch, "E763", {"start": v(0.88, -3.04) * mm, "end": v(0.77, -3.07) * mm});
            skLineSegment(sketch, "E764", {"start": v(0.77, -3.07) * mm, "end": v(0.64, -3.07) * mm});
            skLineSegment(sketch, "E765", {"start": v(0.64, -3.07) * mm, "end": v(0.5, -3.04) * mm});
            skLineSegment(sketch, "E766", {"start": v(0.5, -3.04) * mm, "end": v(0.4, -2.98) * mm});
            skLineSegment(sketch, "E767", {"start": v(0.4, -2.98) * mm, "end": v(0.24, -2.8) * mm});
            skLineSegment(sketch, "E768", {"start": v(0.24, -2.8) * mm, "end": v(0.08, -2.6) * mm});
            skLineSegment(sketch, "E769", {"start": v(0.08, -2.6) * mm, "end": v(-0.06, -2.39) * mm});
            skLineSegment(sketch, "E770", {"start": v(-0.06, -2.39) * mm, "end": v(-0.14, -2.17) * mm});
            skLineSegment(sketch, "E771", {"start": v(-0.14, -2.17) * mm, "end": v(-0.45, -0.76) * mm});
            skLineSegment(sketch, "E772", {"start": v(-0.45, -0.76) * mm, "end": v(-0.75, 0.64) * mm});
            skLineSegment(sketch, "E773", {"start": v(-0.75, 0.64) * mm, "end": v(-1.04, 2.05) * mm});
            skLineSegment(sketch, "E774", {"start": v(-1.04, 2.05) * mm, "end": v(-1.31, 3.46) * mm});
            skLineSegment(sketch, "E775", {"start": v(-1.31, 3.46) * mm, "end": v(-1.54, 4.51) * mm});
            skLineSegment(sketch, "E776", {"start": v(-1.54, 4.51) * mm, "end": v(-1.76, 5.58) * mm});
            skLineSegment(sketch, "E777", {"start": v(-1.76, 5.58) * mm, "end": v(-1.94, 6.64) * mm});
            skLineSegment(sketch, "E778", {"start": v(-1.94, 6.64) * mm, "end": v(-2.02, 7.7) * mm});
            skLineSegment(sketch, "E779", {"start": v(-2.02, 7.7) * mm, "end": v(-2.05, 9.67) * mm});
            skLineSegment(sketch, "E780", {"start": v(-2.05, 9.67) * mm, "end": v(-2.08, 11.63) * mm});
            skLineSegment(sketch, "E781", {"start": v(-2.08, 11.63) * mm, "end": v(-2.05, 13.6) * mm});
            skLineSegment(sketch, "E782", {"start": v(-2.05, 13.6) * mm, "end": v(-1.92, 15.57) * mm});
            skLineSegment(sketch, "E783", {"start": v(-1.92, 15.57) * mm, "end": v(-1.85, 16.57) * mm});
            skLineSegment(sketch, "E784", {"start": v(-1.85, 16.57) * mm, "end": v(-1.82, 17.57) * mm});
            skLineSegment(sketch, "E785", {"start": v(-1.82, 17.57) * mm, "end": v(-1.8, 18.57) * mm});
            skLineSegment(sketch, "E786", {"start": v(-1.8, 18.57) * mm, "end": v(-1.8, 19.58) * mm});
            skLineSegment(sketch, "E787", {"start": v(-1.8, 19.58) * mm, "end": v(-1.78, 20.07) * mm});
            skLineSegment(sketch, "E788", {"start": v(-1.78, 20.07) * mm, "end": v(-1.76, 20.56) * mm});
            skLineSegment(sketch, "E789", {"start": v(-1.76, 20.56) * mm, "end": v(-1.77, 21.05) * mm});
            skLineSegment(sketch, "E790", {"start": v(-1.77, 21.05) * mm, "end": v(-1.82, 21.53) * mm});
            skLineSegment(sketch, "E791", {"start": v(-1.82, 21.53) * mm, "end": v(-2.19, 22.97) * mm});
            skLineSegment(sketch, "E792", {"start": v(-2.19, 22.97) * mm, "end": v(-2.78, 24.3) * mm});
            skLineSegment(sketch, "E793", {"start": v(-2.78, 24.3) * mm, "end": v(-3.58, 25.5) * mm});
            skLineSegment(sketch, "E794", {"start": v(-3.58, 25.5) * mm, "end": v(-4.58, 26.6) * mm});
            skLineSegment(sketch, "E795", {"start": v(-4.58, 26.6) * mm, "end": v(-5.46, 27.32) * mm});
            skLineSegment(sketch, "E796", {"start": v(-5.46, 27.32) * mm, "end": v(-6.43, 27.86) * mm});
            skLineSegment(sketch, "E797", {"start": v(-6.43, 27.86) * mm, "end": v(-7.49, 28.21) * mm});
            skLineSegment(sketch, "E798", {"start": v(-7.49, 28.21) * mm, "end": v(-8.64, 28.4) * mm});
            skLineSegment(sketch, "E799", {"start": v(-8.64, 28.4) * mm, "end": v(-10.75, 28.5) * mm});
            skLineSegment(sketch, "E800", {"start": v(-10.75, 28.5) * mm, "end": v(-12.8, 28.34) * mm});
            skLineSegment(sketch, "E801", {"start": v(-12.8, 28.34) * mm, "end": v(-14.77, 27.8) * mm});
            skLineSegment(sketch, "E802", {"start": v(-14.77, 27.8) * mm, "end": v(-16.66, 26.77) * mm});
            skLineSegment(sketch, "E803", {"start": v(-16.66, 26.77) * mm, "end": v(-17.7, 25.99) * mm});
            skLineSegment(sketch, "E804", {"start": v(-17.7, 25.99) * mm, "end": v(-18.67, 25.16) * mm});
            skLineSegment(sketch, "E805", {"start": v(-18.67, 25.16) * mm, "end": v(-19.58, 24.26) * mm});
            skLineSegment(sketch, "E806", {"start": v(-19.58, 24.26) * mm, "end": v(-20.4, 23.27) * mm});
            skLineSegment(sketch, "E807", {"start": v(-20.4, 23.27) * mm, "end": v(-20.62, 22.9) * mm});
            skLineSegment(sketch, "E808", {"start": v(-20.62, 22.9) * mm, "end": v(-20.66, 22.6) * mm});
            skLineSegment(sketch, "E809", {"start": v(-20.66, 22.6) * mm, "end": v(-20.52, 22.35) * mm});
            skLineSegment(sketch, "E810", {"start": v(-20.52, 22.35) * mm, "end": v(-20.2, 22.18) * mm});
            skLineSegment(sketch, "E811", {"start": v(-20.2, 22.18) * mm, "end": v(-19.47, 21.84) * mm});
            skLineSegment(sketch, "E812", {"start": v(-19.47, 21.84) * mm, "end": v(-18.87, 21.37) * mm});
            skLineSegment(sketch, "E813", {"start": v(-18.87, 21.37) * mm, "end": v(-18.38, 20.78) * mm});
            skLineSegment(sketch, "E814", {"start": v(-18.38, 20.78) * mm, "end": v(-17.98, 20.1) * mm});
            skLineSegment(sketch, "E815", {"start": v(-17.98, 20.1) * mm, "end": v(-17.82, 19.8) * mm});
            skLineSegment(sketch, "E816", {"start": v(-17.82, 19.8) * mm, "end": v(-17.67, 19.47) * mm});
            skLineSegment(sketch, "E817", {"start": v(-17.67, 19.47) * mm, "end": v(-17.52, 19.14) * mm});
            skLineSegment(sketch, "E818", {"start": v(-17.52, 19.14) * mm, "end": v(-17.37, 18.8) * mm});
            skLineSegment(sketch, "E819", {"start": v(-17.37, 18.8) * mm, "end": v(-17.14, 18.91) * mm});
            skLineSegment(sketch, "E820", {"start": v(-17.14, 18.91) * mm, "end": v(-16.93, 19.02) * mm});
            skLineSegment(sketch, "E821", {"start": v(-16.93, 19.02) * mm, "end": v(-16.71, 19.1) * mm});
            skLineSegment(sketch, "E822", {"start": v(-16.71, 19.1) * mm, "end": v(-16.5, 19.16) * mm});
            skLineSegment(sketch, "E823", {"start": v(-16.5, 19.16) * mm, "end": v(-16.3, 19.17) * mm});
            skLineSegment(sketch, "E824", {"start": v(-16.3, 19.17) * mm, "end": v(-16.09, 19.15) * mm});
            skLineSegment(sketch, "E825", {"start": v(-16.09, 19.15) * mm, "end": v(-15.88, 19.12) * mm});
            skLineSegment(sketch, "E826", {"start": v(-15.88, 19.12) * mm, "end": v(-15.66, 19.09) * mm});
            skLineSegment(sketch, "E827", {"start": v(-15.66, 19.09) * mm, "end": v(-15.75, 18.9) * mm});
            skLineSegment(sketch, "E828", {"start": v(-15.75, 18.9) * mm, "end": v(-15.83, 18.71) * mm});
            skLineSegment(sketch, "E829", {"start": v(-15.83, 18.71) * mm, "end": v(-15.92, 18.53) * mm});
            skLineSegment(sketch, "E830", {"start": v(-15.92, 18.53) * mm, "end": v(-16, 18.34) * mm});
            skLineSegment(sketch, "E831", {"start": v(-16, 18.34) * mm, "end": v(-16.02, 18.32) * mm});
            skLineSegment(sketch, "E832", {"start": v(-16.02, 18.32) * mm, "end": v(-16.05, 18.3) * mm});
            skLineSegment(sketch, "E833", {"start": v(-16.05, 18.3) * mm, "end": v(-16.07, 18.28) * mm});
            skLineSegment(sketch, "E834", {"start": v(-16.07, 18.28) * mm, "end": v(-16.1, 18.26) * mm});
            skLineSegment(sketch, "E835", {"start": v(-16.1, 18.26) * mm, "end": v(-16.72, 17.72) * mm});
            skLineSegment(sketch, "E836", {"start": v(-16.72, 17.72) * mm, "end": v(-17.34, 17.18) * mm});
            skLineSegment(sketch, "E837", {"start": v(-17.34, 17.18) * mm, "end": v(-17.96, 16.63) * mm});
            skLineSegment(sketch, "E838", {"start": v(-17.96, 16.63) * mm, "end": v(-18.56, 16.07) * mm});
            skLineSegment(sketch, "E839", {"start": v(-18.56, 16.07) * mm, "end": v(-18.9, 15.57) * mm});
            skLineSegment(sketch, "E840", {"start": v(-18.9, 15.57) * mm, "end": v(-18.97, 15.03) * mm});
            skLineSegment(sketch, "E841", {"start": v(-18.97, 15.03) * mm, "end": v(-18.8, 14.57) * mm});
            skLineSegment(sketch, "E842", {"start": v(-18.8, 14.57) * mm, "end": v(-18.4, 14.3) * mm});
            skLineSegment(sketch, "E843", {"start": v(-18.4, 14.3) * mm, "end": v(-17.89, 14.19) * mm});
            skLineSegment(sketch, "E844", {"start": v(-17.89, 14.19) * mm, "end": v(-17.37, 14.17) * mm});
            skLineSegment(sketch, "E845", {"start": v(-17.37, 14.17) * mm, "end": v(-16.85, 14.25) * mm});
            skLineSegment(sketch, "E846", {"start": v(-16.85, 14.25) * mm, "end": v(-16.32, 14.41) * mm});
            skLineSegment(sketch, "E847", {"start": v(-16.32, 14.41) * mm, "end": v(-16.4, 14.58) * mm});
            skLineSegment(sketch, "E848", {"start": v(-16.4, 14.58) * mm, "end": v(-16.47, 14.73) * mm});
            skLineSegment(sketch, "E849", {"start": v(-16.47, 14.73) * mm, "end": v(-16.55, 14.88) * mm});
            skLineSegment(sketch, "E850", {"start": v(-16.55, 14.88) * mm, "end": v(-16.62, 15.02) * mm});
            skLineSegment(sketch, "E851", {"start": v(-16.62, 15.02) * mm, "end": v(-16.74, 15.38) * mm});
            skLineSegment(sketch, "E852", {"start": v(-16.74, 15.38) * mm, "end": v(-16.7, 15.64) * mm});
            skLineSegment(sketch, "E853", {"start": v(-16.7, 15.64) * mm, "end": v(-16.5, 15.8) * mm});
            skLineSegment(sketch, "E854", {"start": v(-16.5, 15.8) * mm, "end": v(-16.13, 15.88) * mm});
            skLineSegment(sketch, "E855", {"start": v(-16.13, 15.88) * mm, "end": v(-15.57, 15.78) * mm});
            skLineSegment(sketch, "E856", {"start": v(-15.57, 15.78) * mm, "end": v(-15.03, 15.46) * mm});
            skLineSegment(sketch, "E857", {"start": v(-15.03, 15.46) * mm, "end": v(-14.6, 15) * mm});
            skLineSegment(sketch, "E858", {"start": v(-14.6, 15) * mm, "end": v(-14.41, 14.48) * mm});
            skLineSegment(sketch, "E859", {"start": v(-14.41, 14.48) * mm, "end": v(-14.41, 14.4) * mm});
            skLineSegment(sketch, "E860", {"start": v(-14.41, 14.4) * mm, "end": v(-14.43, 14.3) * mm});
            skLineSegment(sketch, "E861", {"start": v(-14.43, 14.3) * mm, "end": v(-14.46, 14.22) * mm});
            skLineSegment(sketch, "E862", {"start": v(-14.46, 14.22) * mm, "end": v(-14.5, 14.15) * mm});
            skLineSegment(sketch, "E863", {"start": v(-14.5, 14.15) * mm, "end": v(-15.07, 13.62) * mm});
            skLineSegment(sketch, "E864", {"start": v(-15.07, 13.62) * mm, "end": v(-15.68, 13.16) * mm});
            skLineSegment(sketch, "E865", {"start": v(-15.68, 13.16) * mm, "end": v(-16.36, 12.86) * mm});
            skLineSegment(sketch, "E866", {"start": v(-16.36, 12.86) * mm, "end": v(-17.18, 12.8) * mm});
            skLineSegment(sketch, "E867", {"start": v(-17.18, 12.8) * mm, "end": v(-17.58, 12.85) * mm});
            skLineSegment(sketch, "E868", {"start": v(-17.58, 12.85) * mm, "end": v(-17.98, 12.9) * mm});
            skLineSegment(sketch, "E869", {"start": v(-17.98, 12.9) * mm, "end": v(-18.38, 12.93) * mm});
            skLineSegment(sketch, "E870", {"start": v(-18.38, 12.93) * mm, "end": v(-18.78, 13) * mm});
            skLineSegment(sketch, "E871", {"start": v(-18.78, 13) * mm, "end": v(-19.49, 13.25) * mm});
            skLineSegment(sketch, "E872", {"start": v(-19.49, 13.25) * mm, "end": v(-19.98, 13.67) * mm});
            skLineSegment(sketch, "E873", {"start": v(-19.98, 13.67) * mm, "end": v(-20.26, 14.26) * mm});
            skLineSegment(sketch, "E874", {"start": v(-20.26, 14.26) * mm, "end": v(-20.33, 15.01) * mm});
            skLineSegment(sketch, "E875", {"start": v(-20.33, 15.01) * mm, "end": v(-20.32, 15.2) * mm});
            skLineSegment(sketch, "E876", {"start": v(-20.32, 15.2) * mm, "end": v(-20.3, 15.37) * mm});
            skLineSegment(sketch, "E877", {"start": v(-20.3, 15.37) * mm, "end": v(-20.29, 15.54) * mm});
            skLineSegment(sketch, "E878", {"start": v(-20.29, 15.54) * mm, "end": v(-20.27, 15.72) * mm});
            skLineSegment(sketch, "E879", {"start": v(22.23, -3.5) * mm, "end": v(22.26, -3.1) * mm});
            skLineSegment(sketch, "E880", {"start": v(22.26, -3.1) * mm, "end": v(22.3, -2.78) * mm});
            skLineSegment(sketch, "E881", {"start": v(22.3, -2.78) * mm, "end": v(22.32, -2.5) * mm});
            skLineSegment(sketch, "E882", {"start": v(22.32, -2.5) * mm, "end": v(22.35, -2.23) * mm});
            skLineSegment(sketch, "E883", {"start": v(22.35, -2.23) * mm, "end": v(22.35, -1.57) * mm});
            skLineSegment(sketch, "E884", {"start": v(22.35, -1.57) * mm, "end": v(22.14, -1.17) * mm});
            skLineSegment(sketch, "E885", {"start": v(22.14, -1.17) * mm, "end": v(21.71, -1.02) * mm});
            skLineSegment(sketch, "E886", {"start": v(21.71, -1.02) * mm, "end": v(21.05, -1.12) * mm});
            skLineSegment(sketch, "E887", {"start": v(21.05, -1.12) * mm, "end": v(20.84, -1.2) * mm});
            skLineSegment(sketch, "E888", {"start": v(20.84, -1.2) * mm, "end": v(20.64, -1.31) * mm});
            skLineSegment(sketch, "E889", {"start": v(20.64, -1.31) * mm, "end": v(20.44, -1.42) * mm});
            skLineSegment(sketch, "E890", {"start": v(20.44, -1.42) * mm, "end": v(20.24, -1.5) * mm});
            skLineSegment(sketch, "E891", {"start": v(20.24, -1.5) * mm, "end": v(19.81, -1.63) * mm});
            skLineSegment(sketch, "E892", {"start": v(19.81, -1.63) * mm, "end": v(19.39, -1.75) * mm});
            skLineSegment(sketch, "E893", {"start": v(19.39, -1.75) * mm, "end": v(18.96, -1.84) * mm});
            skLineSegment(sketch, "E894", {"start": v(18.96, -1.84) * mm, "end": v(18.53, -1.89) * mm});
            skLineSegment(sketch, "E895", {"start": v(18.53, -1.89) * mm, "end": v(18.13, -1.87) * mm});
            skLineSegment(sketch, "E896", {"start": v(18.13, -1.87) * mm, "end": v(17.74, -1.76) * mm});
            skLineSegment(sketch, "E897", {"start": v(17.74, -1.76) * mm, "end": v(17.41, -1.54) * mm});
            skLineSegment(sketch, "E898", {"start": v(17.41, -1.54) * mm, "end": v(17.18, -1.18) * mm});
            skLineSegment(sketch, "E899", {"start": v(17.18, -1.18) * mm, "end": v(17.14, -0.76) * mm});
            skLineSegment(sketch, "E900", {"start": v(17.14, -0.76) * mm, "end": v(17.3, -0.43) * mm});
            skLineSegment(sketch, "E901", {"start": v(17.3, -0.43) * mm, "end": v(17.56, -0.15) * mm});
            skLineSegment(sketch, "E902", {"start": v(17.56, -0.15) * mm, "end": v(17.86, 0.1) * mm});
            skLineSegment(sketch, "E903", {"start": v(17.86, 0.1) * mm, "end": v(18.07, 0.31) * mm});
            skLineSegment(sketch, "E904", {"start": v(18.07, 0.31) * mm, "end": v(18.29, 0.52) * mm});
            skLineSegment(sketch, "E905", {"start": v(18.29, 0.52) * mm, "end": v(18.5, 0.73) * mm});
            skLineSegment(sketch, "E906", {"start": v(18.5, 0.73) * mm, "end": v(18.73, 0.92) * mm});
            skLineSegment(sketch, "E907", {"start": v(18.73, 0.92) * mm, "end": v(19.51, 1.71) * mm});
            skLineSegment(sketch, "E908", {"start": v(19.51, 1.71) * mm, "end": v(20.12, 2.6) * mm});
            skLineSegment(sketch, "E909", {"start": v(20.12, 2.6) * mm, "end": v(20.57, 3.58) * mm});
            skLineSegment(sketch, "E910", {"start": v(20.57, 3.58) * mm, "end": v(20.88, 4.64) * mm});
            skLineSegment(sketch, "E911", {"start": v(20.88, 4.64) * mm, "end": v(21, 5.24) * mm});
            skLineSegment(sketch, "E912", {"start": v(21, 5.24) * mm, "end": v(21.13, 5.84) * mm});
            skLineSegment(sketch, "E913", {"start": v(21.13, 5.84) * mm, "end": v(21.26, 6.44) * mm});
            skLineSegment(sketch, "E914", {"start": v(21.26, 6.44) * mm, "end": v(21.4, 7.04) * mm});
            skLineSegment(sketch, "E915", {"start": v(21.4, 7.04) * mm, "end": v(21.48, 8.16) * mm});
            skLineSegment(sketch, "E916", {"start": v(21.48, 8.16) * mm, "end": v(21.24, 9.2) * mm});
            skLineSegment(sketch, "E917", {"start": v(21.24, 9.2) * mm, "end": v(20.7, 10.13) * mm});
            skLineSegment(sketch, "E918", {"start": v(20.7, 10.13) * mm, "end": v(19.86, 10.88) * mm});
            skLineSegment(sketch, "E919", {"start": v(19.86, 10.88) * mm, "end": v(19.06, 11.25) * mm});
            skLineSegment(sketch, "E920", {"start": v(19.06, 11.25) * mm, "end": v(18.37, 11.23) * mm});
            skLineSegment(sketch, "E921", {"start": v(18.37, 11.23) * mm, "end": v(17.81, 10.83) * mm});
            skLineSegment(sketch, "E922", {"start": v(17.81, 10.83) * mm, "end": v(17.4, 10.04) * mm});
            skLineSegment(sketch, "E923", {"start": v(17.4, 10.04) * mm, "end": v(17.15, 9.33) * mm});
            skLineSegment(sketch, "E924", {"start": v(17.15, 9.33) * mm, "end": v(16.91, 8.62) * mm});
            skLineSegment(sketch, "E925", {"start": v(16.91, 8.62) * mm, "end": v(16.66, 7.92) * mm});
            skLineSegment(sketch, "E926", {"start": v(16.66, 7.92) * mm, "end": v(16.38, 7.23) * mm});
            skLineSegment(sketch, "E927", {"start": v(16.38, 7.23) * mm, "end": v(15.48, 5.28) * mm});
            skLineSegment(sketch, "E928", {"start": v(15.48, 5.28) * mm, "end": v(14.51, 3.38) * mm});
            skLineSegment(sketch, "E929", {"start": v(14.51, 3.38) * mm, "end": v(13.4, 1.56) * mm});
            skLineSegment(sketch, "E930", {"start": v(13.4, 1.56) * mm, "end": v(12.1, -0.16) * mm});
            skLineSegment(sketch, "E931", {"start": v(12.1, -0.16) * mm, "end": v(11.82, -0.64) * mm});
            skLineSegment(sketch, "E932", {"start": v(11.82, -0.64) * mm, "end": v(11.8, -1.02) * mm});
            skLineSegment(sketch, "E933", {"start": v(11.8, -1.02) * mm, "end": v(12.06, -1.33) * mm});
            skLineSegment(sketch, "E934", {"start": v(12.06, -1.33) * mm, "end": v(12.58, -1.55) * mm});
            skLineSegment(sketch, "E935", {"start": v(12.58, -1.55) * mm, "end": v(13.06, -1.68) * mm});
            skLineSegment(sketch, "E936", {"start": v(13.06, -1.68) * mm, "end": v(13.54, -1.8) * mm});
            skLineSegment(sketch, "E937", {"start": v(13.54, -1.8) * mm, "end": v(14.02, -1.92) * mm});
            skLineSegment(sketch, "E938", {"start": v(14.02, -1.92) * mm, "end": v(14.5, -2.06) * mm});
            skLineSegment(sketch, "E939", {"start": v(14.5, -2.06) * mm, "end": v(16.06, -2.69) * mm});
            skLineSegment(sketch, "E940", {"start": v(16.06, -2.69) * mm, "end": v(17.41, -3.58) * mm});
            skLineSegment(sketch, "E941", {"start": v(17.41, -3.58) * mm, "end": v(18.52, -4.76) * mm});
            skLineSegment(sketch, "E942", {"start": v(18.52, -4.76) * mm, "end": v(19.38, -6.24) * mm});
            skLineSegment(sketch, "E943", {"start": v(19.38, -6.24) * mm, "end": v(19.54, -6.5) * mm});
            skLineSegment(sketch, "E944", {"start": v(19.54, -6.5) * mm, "end": v(19.78, -6.75) * mm});
            skLineSegment(sketch, "E945", {"start": v(19.78, -6.75) * mm, "end": v(20.06, -6.96) * mm});
            skLineSegment(sketch, "E946", {"start": v(20.06, -6.96) * mm, "end": v(20.35, -7.13) * mm});
            skLineSegment(sketch, "E947", {"start": v(20.35, -7.13) * mm, "end": v(21.04, -7.37) * mm});
            skLineSegment(sketch, "E948", {"start": v(21.04, -7.37) * mm, "end": v(21.75, -7.49) * mm});
            skLineSegment(sketch, "E949", {"start": v(21.75, -7.49) * mm, "end": v(22.48, -7.5) * mm});
            skLineSegment(sketch, "E950", {"start": v(22.48, -7.5) * mm, "end": v(23.22, -7.4) * mm});
            skLineSegment(sketch, "E951", {"start": v(23.22, -7.4) * mm, "end": v(23.2, -6.94) * mm});
            skLineSegment(sketch, "E952", {"start": v(23.2, -6.94) * mm, "end": v(23.27, -6.7) * mm});
            skLineSegment(sketch, "E953", {"start": v(23.27, -6.7) * mm, "end": v(23.5, -6.61) * mm});
            skLineSegment(sketch, "E954", {"start": v(23.5, -6.61) * mm, "end": v(23.93, -6.59) * mm});
            skLineSegment(sketch, "E955", {"start": v(23.93, -6.59) * mm, "end": v(24.2, -6.54) * mm});
            skLineSegment(sketch, "E956", {"start": v(24.2, -6.54) * mm, "end": v(24.4, -6.4) * mm});
            skLineSegment(sketch, "E957", {"start": v(24.4, -6.4) * mm, "end": v(24.5, -6.2) * mm});
            skLineSegment(sketch, "E958", {"start": v(24.5, -6.2) * mm, "end": v(24.52, -5.93) * mm});
            skLineSegment(sketch, "E959", {"start": v(24.52, -5.93) * mm, "end": v(24.45, -5.57) * mm});
            skLineSegment(sketch, "E960", {"start": v(24.45, -5.57) * mm, "end": v(24.27, -5.3) * mm});
            skLineSegment(sketch, "E961", {"start": v(24.27, -5.3) * mm, "end": v(24.01, -5.1) * mm});
            skLineSegment(sketch, "E962", {"start": v(24.01, -5.1) * mm, "end": v(23.69, -4.96) * mm});
            skLineSegment(sketch, "E963", {"start": v(23.69, -4.96) * mm, "end": v(23.42, -4.91) * mm});
            skLineSegment(sketch, "E964", {"start": v(23.42, -4.91) * mm, "end": v(23.15, -4.88) * mm});
            skLineSegment(sketch, "E965", {"start": v(23.15, -4.88) * mm, "end": v(22.88, -4.85) * mm});
            skLineSegment(sketch, "E966", {"start": v(22.88, -4.85) * mm, "end": v(22.63, -4.79) * mm});
            skLineSegment(sketch, "E967", {"start": v(22.63, -4.79) * mm, "end": v(21.94, -4.55) * mm});
            skLineSegment(sketch, "E968", {"start": v(21.94, -4.55) * mm, "end": v(21.26, -4.3) * mm});
            skLineSegment(sketch, "E969", {"start": v(21.26, -4.3) * mm, "end": v(20.59, -4.02) * mm});
            skLineSegment(sketch, "E970", {"start": v(20.59, -4.02) * mm, "end": v(19.92, -3.73) * mm});
            skLineSegment(sketch, "E971", {"start": v(19.92, -3.73) * mm, "end": v(19.8, -3.62) * mm});
            skLineSegment(sketch, "E972", {"start": v(19.8, -3.62) * mm, "end": v(19.71, -3.42) * mm});
            skLineSegment(sketch, "E973", {"start": v(19.71, -3.42) * mm, "end": v(19.66, -3.21) * mm});
            skLineSegment(sketch, "E974", {"start": v(19.66, -3.21) * mm, "end": v(19.68, -3.05) * mm});
            skLineSegment(sketch, "E975", {"start": v(19.68, -3.05) * mm, "end": v(19.8, -2.9) * mm});
            skLineSegment(sketch, "E976", {"start": v(19.8, -2.9) * mm, "end": v(19.97, -2.77) * mm});
            skLineSegment(sketch, "E977", {"start": v(19.97, -2.77) * mm, "end": v(20.17, -2.68) * mm});
            skLineSegment(sketch, "E978", {"start": v(20.17, -2.68) * mm, "end": v(20.37, -2.63) * mm});
            skLineSegment(sketch, "E979", {"start": v(20.37, -2.63) * mm, "end": v(20.53, -2.66) * mm});
            skLineSegment(sketch, "E980", {"start": v(20.53, -2.66) * mm, "end": v(20.7, -2.73) * mm});
            skLineSegment(sketch, "E981", {"start": v(20.7, -2.73) * mm, "end": v(20.89, -2.83) * mm});
            skLineSegment(sketch, "E982", {"start": v(20.89, -2.83) * mm, "end": v(21.06, -2.93) * mm});
            skLineSegment(sketch, "E983", {"start": v(21.06, -2.93) * mm, "end": v(21.32, -3.05) * mm});
            skLineSegment(sketch, "E984", {"start": v(21.32, -3.05) * mm, "end": v(21.6, -3.18) * mm});
            skLineSegment(sketch, "E985", {"start": v(21.6, -3.18) * mm, "end": v(21.9, -3.33) * mm});
            skLineSegment(sketch, "E986", {"start": v(21.9, -3.33) * mm, "end": v(22.23, -3.5) * mm});
            skLineSegment(sketch, "E987", {"start": v(-14.26, -28.41) * mm, "end": v(-13.99, -28.23) * mm});
            skLineSegment(sketch, "E988", {"start": v(-13.99, -28.23) * mm, "end": v(-13.7, -28.05) * mm});
            skLineSegment(sketch, "E989", {"start": v(-13.7, -28.05) * mm, "end": v(-13.43, -27.85) * mm});
            skLineSegment(sketch, "E990", {"start": v(-13.43, -27.85) * mm, "end": v(-13.18, -27.61) * mm});
            skLineSegment(sketch, "E991", {"start": v(-13.18, -27.61) * mm, "end": v(-13, -27.37) * mm});
            skLineSegment(sketch, "E992", {"start": v(-13, -27.37) * mm, "end": v(-12.84, -27.1) * mm});
            skLineSegment(sketch, "E993", {"start": v(-12.84, -27.1) * mm, "end": v(-12.71, -26.8) * mm});
            skLineSegment(sketch, "E994", {"start": v(-12.71, -26.8) * mm, "end": v(-12.6, -26.5) * mm});
            skLineSegment(sketch, "E995", {"start": v(-12.6, -26.5) * mm, "end": v(-12.05, -24.92) * mm});
            skLineSegment(sketch, "E996", {"start": v(-12.05, -24.92) * mm, "end": v(-11.5, -23.34) * mm});
            skLineSegment(sketch, "E997", {"start": v(-11.5, -23.34) * mm, "end": v(-10.96, -21.76) * mm});
            skLineSegment(sketch, "E998", {"start": v(-10.96, -21.76) * mm, "end": v(-10.41, -20.17) * mm});
            skLineSegment(sketch, "E999", {"start": v(-10.41, -20.17) * mm, "end": v(-10.34, -19.93) * mm});
            skLineSegment(sketch, "E1000", {"start": v(-10.34, -19.93) * mm, "end": v(-10.33, -19.7) * mm});
            skLineSegment(sketch, "E1001", {"start": v(-10.33, -19.7) * mm, "end": v(-10.41, -19.5) * mm});
            skLineSegment(sketch, "E1002", {"start": v(-10.41, -19.5) * mm, "end": v(-10.62, -19.35) * mm});
            skLineSegment(sketch, "E1003", {"start": v(-10.62, -19.35) * mm, "end": v(-10.9, -19.3) * mm});
            skLineSegment(sketch, "E1004", {"start": v(-10.9, -19.3) * mm, "end": v(-11.12, -19.38) * mm});
            skLineSegment(sketch, "E1005", {"start": v(-11.12, -19.38) * mm, "end": v(-11.27, -19.57) * mm});
            skLineSegment(sketch, "E1006", {"start": v(-11.27, -19.57) * mm, "end": v(-11.38, -19.8) * mm});
            skLineSegment(sketch, "E1007", {"start": v(-11.38, -19.8) * mm, "end": v(-11.63, -20.42) * mm});
            skLineSegment(sketch, "E1008", {"start": v(-11.63, -20.42) * mm, "end": v(-11.88, -21.02) * mm});
            skLineSegment(sketch, "E1009", {"start": v(-11.88, -21.02) * mm, "end": v(-12.12, -21.64) * mm});
            skLineSegment(sketch, "E1010", {"start": v(-12.12, -21.64) * mm, "end": v(-12.35, -22.25) * mm});
            skLineSegment(sketch, "E1011", {"start": v(-12.35, -22.25) * mm, "end": v(-12.6, -23) * mm});
            skLineSegment(sketch, "E1012", {"start": v(-12.6, -23) * mm, "end": v(-12.84, -23.76) * mm});
            skLineSegment(sketch, "E1013", {"start": v(-12.84, -23.76) * mm, "end": v(-13.07, -24.52) * mm});
            skLineSegment(sketch, "E1014", {"start": v(-13.07, -24.52) * mm, "end": v(-13.3, -25.28) * mm});
            skLineSegment(sketch, "E1015", {"start": v(-13.3, -25.28) * mm, "end": v(-13.63, -25.96) * mm});
            skLineSegment(sketch, "E1016", {"start": v(-13.63, -25.96) * mm, "end": v(-14.1, -26.28) * mm});
            skLineSegment(sketch, "E1017", {"start": v(-14.1, -26.28) * mm, "end": v(-14.67, -26.25) * mm});
            skLineSegment(sketch, "E1018", {"start": v(-14.67, -26.25) * mm, "end": v(-15.3, -25.85) * mm});
            skLineSegment(sketch, "E1019", {"start": v(-15.3, -25.85) * mm, "end": v(-15.37, -25.79) * mm});
            skLineSegment(sketch, "E1020", {"start": v(-15.37, -25.79) * mm, "end": v(-15.44, -25.73) * mm});
            skLineSegment(sketch, "E1021", {"start": v(-15.44, -25.73) * mm, "end": v(-15.5, -25.67) * mm});
            skLineSegment(sketch, "E1022", {"start": v(-15.5, -25.67) * mm, "end": v(-15.57, -25.6) * mm});
            skLineSegment(sketch, "E1023", {"start": v(-15.57, -25.6) * mm, "end": v(-16.06, -25.17) * mm});
            skLineSegment(sketch, "E1024", {"start": v(-16.06, -25.17) * mm, "end": v(-16.55, -24.73) * mm});
            skLineSegment(sketch, "E1025", {"start": v(-16.55, -24.73) * mm, "end": v(-17.05, -24.3) * mm});
            skLineSegment(sketch, "E1026", {"start": v(-17.05, -24.3) * mm, "end": v(-17.55, -23.87) * mm});
            skLineSegment(sketch, "E1027", {"start": v(-17.55, -23.87) * mm, "end": v(-17.69, -23.78) * mm});
            skLineSegment(sketch, "E1028", {"start": v(-17.69, -23.78) * mm, "end": v(-17.85, -23.72) * mm});
            skLineSegment(sketch, "E1029", {"start": v(-17.85, -23.72) * mm, "end": v(-18, -23.7) * mm});
            skLineSegment(sketch, "E1030", {"start": v(-18, -23.7) * mm, "end": v(-18.12, -23.72) * mm});
            skLineSegment(sketch, "E1031", {"start": v(-18.12, -23.72) * mm, "end": v(-18.24, -23.83) * mm});
            skLineSegment(sketch, "E1032", {"start": v(-18.24, -23.83) * mm, "end": v(-18.34, -23.98) * mm});
            skLineSegment(sketch, "E1033", {"start": v(-18.34, -23.98) * mm, "end": v(-18.4, -24.15) * mm});
            skLineSegment(sketch, "E1034", {"start": v(-18.4, -24.15) * mm, "end": v(-18.41, -24.3) * mm});
            skLineSegment(sketch, "E1035", {"start": v(-18.41, -24.3) * mm, "end": v(-18.38, -24.53) * mm});
            skLineSegment(sketch, "E1036", {"start": v(-18.38, -24.53) * mm, "end": v(-18.32, -24.74) * mm});
            skLineSegment(sketch, "E1037", {"start": v(-18.32, -24.74) * mm, "end": v(-18.22, -24.95) * mm});
            skLineSegment(sketch, "E1038", {"start": v(-18.22, -24.95) * mm, "end": v(-18.1, -25.11) * mm});
            skLineSegment(sketch, "E1039", {"start": v(-18.1, -25.11) * mm, "end": v(-17.3, -25.88) * mm});
            skLineSegment(sketch, "E1040", {"start": v(-17.3, -25.88) * mm, "end": v(-16.49, -26.64) * mm});
            skLineSegment(sketch, "E1041", {"start": v(-16.49, -26.64) * mm, "end": v(-15.68, -27.39) * mm});
            skLineSegment(sketch, "E1042", {"start": v(-15.68, -27.39) * mm, "end": v(-14.86, -28.13) * mm});
            skLineSegment(sketch, "E1043", {"start": v(-14.86, -28.13) * mm, "end": v(-14.76, -28.2) * mm});
            skLineSegment(sketch, "E1044", {"start": v(-14.76, -28.2) * mm, "end": v(-14.62, -28.27) * mm});
            skLineSegment(sketch, "E1045", {"start": v(-14.62, -28.27) * mm, "end": v(-14.46, -28.33) * mm});
            skLineSegment(sketch, "E1046", {"start": v(-14.46, -28.33) * mm, "end": v(-14.26, -28.41) * mm});
            skLineSegment(sketch, "E1047", {"start": v(-23.08, 17.07) * mm, "end": v(-22.1, 16.7) * mm});
            skLineSegment(sketch, "E1048", {"start": v(-22.1, 16.7) * mm, "end": v(-21.18, 16.73) * mm});
            skLineSegment(sketch, "E1049", {"start": v(-21.18, 16.73) * mm, "end": v(-20.26, 17.12) * mm});
            skLineSegment(sketch, "E1050", {"start": v(-20.26, 17.12) * mm, "end": v(-19.27, 17.78) * mm});
            skLineSegment(sketch, "E1051", {"start": v(-19.27, 17.78) * mm, "end": v(-18.76, 18.42) * mm});
            skLineSegment(sketch, "E1052", {"start": v(-18.76, 18.42) * mm, "end": v(-18.68, 19.15) * mm});
            skLineSegment(sketch, "E1053", {"start": v(-18.68, 19.15) * mm, "end": v(-19, 19.84) * mm});
            skLineSegment(sketch, "E1054", {"start": v(-19, 19.84) * mm, "end": v(-19.67, 20.35) * mm});
            skLineSegment(sketch, "E1055", {"start": v(-19.67, 20.35) * mm, "end": v(-19.96, 20.45) * mm});
            skLineSegment(sketch, "E1056", {"start": v(-19.96, 20.45) * mm, "end": v(-20.18, 20.42) * mm});
            skLineSegment(sketch, "E1057", {"start": v(-20.18, 20.42) * mm, "end": v(-20.32, 20.26) * mm});
            skLineSegment(sketch, "E1058", {"start": v(-20.32, 20.26) * mm, "end": v(-20.4, 19.97) * mm});
            skLineSegment(sketch, "E1059", {"start": v(-20.4, 19.97) * mm, "end": v(-20.62, 19.08) * mm});
            skLineSegment(sketch, "E1060", {"start": v(-20.62, 19.08) * mm, "end": v(-21.04, 18.35) * mm});
            skLineSegment(sketch, "E1061", {"start": v(-21.04, 18.35) * mm, "end": v(-21.66, 17.77) * mm});
            skLineSegment(sketch, "E1062", {"start": v(-21.66, 17.77) * mm, "end": v(-22.48, 17.36) * mm});
            skLineSegment(sketch, "E1063", {"start": v(-22.48, 17.36) * mm, "end": v(-22.62, 17.3) * mm});
            skLineSegment(sketch, "E1064", {"start": v(-22.62, 17.3) * mm, "end": v(-22.77, 17.23) * mm});
            skLineSegment(sketch, "E1065", {"start": v(-22.77, 17.23) * mm, "end": v(-22.92, 17.15) * mm});
            skLineSegment(sketch, "E1066", {"start": v(-22.92, 17.15) * mm, "end": v(-23.08, 17.07) * mm});
            skLineSegment(sketch, "E1067", {"start": v(-12.6, 30) * mm, "end": v(-13.2, 29.8) * mm});
            skLineSegment(sketch, "E1068", {"start": v(-13.2, 29.8) * mm, "end": v(-13.8, 29.62) * mm});
            skLineSegment(sketch, "E1069", {"start": v(-13.8, 29.62) * mm, "end": v(-14.38, 29.42) * mm});
            skLineSegment(sketch, "E1070", {"start": v(-14.38, 29.42) * mm, "end": v(-14.96, 29.2) * mm});
            skLineSegment(sketch, "E1071", {"start": v(-14.96, 29.2) * mm, "end": v(-17.12, 28.05) * mm});
            skLineSegment(sketch, "E1072", {"start": v(-17.13, 28.06) * mm, "end": v(-19.09, 26.66) * mm});
            skLineSegment(sketch, "E1073", {"start": v(-19.08, 26.65) * mm, "end": v(-20.85, 25.02) * mm});
            skLineSegment(sketch, "E1074", {"start": v(-20.85, 25.02) * mm, "end": v(-22.44, 23.16) * mm});
            skLineSegment(sketch, "E1075", {"start": v(-22.44, 23.16) * mm, "end": v(-22.92, 22.56) * mm});
            skLineSegment(sketch, "E1076", {"start": v(-22.92, 22.56) * mm, "end": v(-23.45, 22) * mm});
            skLineSegment(sketch, "E1077", {"start": v(-23.45, 22) * mm, "end": v(-24.03, 21.49) * mm});
            skLineSegment(sketch, "E1078", {"start": v(-24.03, 21.49) * mm, "end": v(-24.68, 21.04) * mm});
            skLineSegment(sketch, "E1079", {"start": v(-24.68, 21.04) * mm, "end": v(-25.49, 20.35) * mm});
            skLineSegment(sketch, "E1080", {"start": v(-25.49, 20.35) * mm, "end": v(-26.04, 19.45) * mm});
            skLineSegment(sketch, "E1081", {"start": v(-26.04, 19.45) * mm, "end": v(-26.28, 18.43) * mm});
            skLineSegment(sketch, "E1082", {"start": v(-26.28, 18.43) * mm, "end": v(-26.15, 17.4) * mm});
            skLineSegment(sketch, "E1083", {"start": v(-26.15, 17.4) * mm, "end": v(-25.97, 16.53) * mm});
            skLineSegment(sketch, "E1084", {"start": v(-25.97, 16.53) * mm, "end": v(-25.98, 15.67) * mm});
            skLineSegment(sketch, "E1085", {"start": v(-25.98, 15.67) * mm, "end": v(-26.1, 14.83) * mm});
            skLineSegment(sketch, "E1086", {"start": v(-26.1, 14.83) * mm, "end": v(-26.22, 14) * mm});
            skLineSegment(sketch, "E1087", {"start": v(-26.22, 14) * mm, "end": v(-26.37, 12.9) * mm});
            skLineSegment(sketch, "E1088", {"start": v(-26.37, 12.9) * mm, "end": v(-26.53, 11.8) * mm});
            skLineSegment(sketch, "E1089", {"start": v(-26.53, 11.8) * mm, "end": v(-26.69, 10.7) * mm});
            skLineSegment(sketch, "E1090", {"start": v(-26.69, 10.7) * mm, "end": v(-26.84, 9.6) * mm});
            skLineSegment(sketch, "E1091", {"start": v(-26.84, 9.6) * mm, "end": v(-26.85, 9.55) * mm});
            skLineSegment(sketch, "E1092", {"start": v(-26.85, 9.55) * mm, "end": v(-26.85, 9.5) * mm});
            skLineSegment(sketch, "E1093", {"start": v(-26.85, 9.5) * mm, "end": v(-26.85, 9.43) * mm});
            skLineSegment(sketch, "E1094", {"start": v(-26.85, 9.43) * mm, "end": v(-26.84, 9.37) * mm});
            skLineSegment(sketch, "E1095", {"start": v(-26.84, 9.37) * mm, "end": v(-26.82, 8.67) * mm});
            skLineSegment(sketch, "E1096", {"start": v(-26.82, 8.67) * mm, "end": v(-26.8, 7.97) * mm});
            skLineSegment(sketch, "E1097", {"start": v(-26.8, 7.97) * mm, "end": v(-26.77, 7.27) * mm});
            skLineSegment(sketch, "E1098", {"start": v(-26.77, 7.27) * mm, "end": v(-26.74, 6.57) * mm});
            skLineSegment(sketch, "E1099", {"start": v(-26.74, 6.57) * mm, "end": v(-26.7, 5.47) * mm});
            skLineSegment(sketch, "E1100", {"start": v(-26.7, 5.47) * mm, "end": v(-26.67, 4.37) * mm});
            skLineSegment(sketch, "E1101", {"start": v(-26.67, 4.37) * mm, "end": v(-26.65, 3.26) * mm});
            skLineSegment(sketch, "E1102", {"start": v(-26.65, 3.26) * mm, "end": v(-26.67, 2.16) * mm});
            skLineSegment(sketch, "E1103", {"start": v(-26.67, 2.16) * mm, "end": v(-26.6, 1.07) * mm});
            skLineSegment(sketch, "E1104", {"start": v(-26.6, 1.07) * mm, "end": v(-26.38, 0.02) * mm});
            skLineSegment(sketch, "E1105", {"start": v(-26.38, 0.02) * mm, "end": v(-26.07, -1) * mm});
            skLineSegment(sketch, "E1106", {"start": v(-26.07, -1) * mm, "end": v(-25.75, -2.02) * mm});
            skLineSegment(sketch, "E1107", {"start": v(-25.75, -2.02) * mm, "end": v(-24.53, -5.81) * mm});
            skLineSegment(sketch, "E1108", {"start": v(-24.53, -5.81) * mm, "end": v(-22.94, -9.4) * mm});
            skLineSegment(sketch, "E1109", {"start": v(-22.94, -9.4) * mm, "end": v(-20.82, -12.7) * mm});
            skLineSegment(sketch, "E1110", {"start": v(-20.82, -12.7) * mm, "end": v(-18.02, -15.6) * mm});
            skLineSegment(sketch, "E1111", {"start": v(-18.02, -15.6) * mm, "end": v(-17.36, -16.1) * mm});
            skLineSegment(sketch, "E1112", {"start": v(-17.36, -16.1) * mm, "end": v(-16.66, -16.56) * mm});
            skLineSegment(sketch, "E1113", {"start": v(-16.66, -16.56) * mm, "end": v(-15.94, -16.99) * mm});
            skLineSegment(sketch, "E1114", {"start": v(-15.94, -16.99) * mm, "end": v(-15.22, -17.42) * mm});
            skLineSegment(sketch, "E1115", {"start": v(-15.22, -17.42) * mm, "end": v(-14.8, -17.66) * mm});
            skLineSegment(sketch, "E1116", {"start": v(-14.8, -17.66) * mm, "end": v(-14.36, -17.9) * mm});
            skLineSegment(sketch, "E1117", {"start": v(-14.36, -17.9) * mm, "end": v(-13.92, -18.12) * mm});
            skLineSegment(sketch, "E1118", {"start": v(-13.92, -18.12) * mm, "end": v(-13.48, -18.35) * mm});
            skLineSegment(sketch, "E1119", {"start": v(-13.48, -18.35) * mm, "end": v(-12.9, -18.68) * mm});
            skLineSegment(sketch, "E1120", {"start": v(-12.9, -18.68) * mm, "end": v(-12.66, -18.96) * mm});
            skLineSegment(sketch, "E1121", {"start": v(-12.66, -18.96) * mm, "end": v(-12.69, -19.33) * mm});
            skLineSegment(sketch, "E1122", {"start": v(-12.69, -19.33) * mm, "end": v(-12.9, -19.96) * mm});
            skLineSegment(sketch, "E1123", {"start": v(-12.9, -19.96) * mm, "end": v(-13.24, -20.87) * mm});
            skLineSegment(sketch, "E1124", {"start": v(-13.24, -20.87) * mm, "end": v(-13.56, -21.78) * mm});
            skLineSegment(sketch, "E1125", {"start": v(-13.56, -21.78) * mm, "end": v(-13.87, -22.7) * mm});
            skLineSegment(sketch, "E1126", {"start": v(-13.87, -22.7) * mm, "end": v(-14.18, -23.62) * mm});
            skLineSegment(sketch, "E1127", {"start": v(-14.18, -23.62) * mm, "end": v(-14.36, -23.97) * mm});
            skLineSegment(sketch, "E1128", {"start": v(-14.36, -23.97) * mm, "end": v(-14.62, -24.16) * mm});
            skLineSegment(sketch, "E1129", {"start": v(-14.62, -24.16) * mm, "end": v(-14.93, -24.19) * mm});
            skLineSegment(sketch, "E1130", {"start": v(-14.93, -24.19) * mm, "end": v(-15.28, -24.03) * mm});
            skLineSegment(sketch, "E1131", {"start": v(-15.28, -24.03) * mm, "end": v(-15.52, -23.85) * mm});
            skLineSegment(sketch, "E1132", {"start": v(-15.52, -23.85) * mm, "end": v(-15.75, -23.66) * mm});
            skLineSegment(sketch, "E1133", {"start": v(-15.75, -23.66) * mm, "end": v(-15.99, -23.47) * mm});
            skLineSegment(sketch, "E1134", {"start": v(-15.99, -23.47) * mm, "end": v(-16.22, -23.29) * mm});
            skLineSegment(sketch, "E1135", {"start": v(-16.22, -23.29) * mm, "end": v(-16.83, -22.9) * mm});
            skLineSegment(sketch, "E1136", {"start": v(-16.83, -22.9) * mm, "end": v(-17.47, -22.6) * mm});
            skLineSegment(sketch, "E1137", {"start": v(-17.47, -22.6) * mm, "end": v(-18.15, -22.38) * mm});
            skLineSegment(sketch, "E1138", {"start": v(-18.15, -22.38) * mm, "end": v(-18.87, -22.28) * mm});
            skLineSegment(sketch, "E1139", {"start": v(-18.87, -22.28) * mm, "end": v(-19.65, -22.37) * mm});
            skLineSegment(sketch, "E1140", {"start": v(-19.65, -22.37) * mm, "end": v(-20.15, -22.74) * mm});
            skLineSegment(sketch, "E1141", {"start": v(-20.15, -22.74) * mm, "end": v(-20.34, -23.32) * mm});
            skLineSegment(sketch, "E1142", {"start": v(-20.34, -23.32) * mm, "end": v(-20.2, -24.08) * mm});
            skLineSegment(sketch, "E1143", {"start": v(-20.2, -24.08) * mm, "end": v(-19.17, -26) * mm});
            skLineSegment(sketch, "E1144", {"start": v(-19.17, -26) * mm, "end": v(-17.84, -27.6) * mm});
            skLineSegment(sketch, "E1145", {"start": v(-17.84, -27.6) * mm, "end": v(-16.22, -28.9) * mm});
            skLineSegment(sketch, "E1146", {"start": v(-16.22, -28.9) * mm, "end": v(-14.3, -29.9) * mm});
            skLineSegment(sketch, "E1147", {"start": v(-14.3, -29.9) * mm, "end": v(-14.27, -29.93) * mm});
            skLineSegment(sketch, "E1148", {"start": v(-14.27, -29.93) * mm, "end": v(-14.23, -29.95) * mm});
            skLineSegment(sketch, "E1149", {"start": v(-14.23, -29.95) * mm, "end": v(-14.2, -29.98) * mm});
            skLineSegment(sketch, "E1150", {"start": v(-14.2, -29.98) * mm, "end": v(-14.16, -30) * mm});
            skLineSegment(sketch, "E1151", {"start": v(-14.16, -30) * mm, "end": v(-18.12, -30) * mm});
            skLineSegment(sketch, "E1152", {"start": v(-18.12, -30) * mm, "end": v(-22.08, -30) * mm});
            skLineSegment(sketch, "E1153", {"start": v(-22.08, -30) * mm, "end": v(-26.04, -30) * mm});
            skLineSegment(sketch, "E1154", {"start": v(-26.04, -30) * mm, "end": v(-30, -30) * mm});
            skLineSegment(sketch, "E1155", {"start": v(-30, -30) * mm, "end": v(-30, -15) * mm});
            skLineSegment(sketch, "E1156", {"start": v(-30, 0) * mm, "end": v(-30, 15) * mm});
            skLineSegment(sketch, "E1157", {"start": v(-20.27, 15.72) * mm, "end": v(-20.29, 15.54) * mm});
            skLineSegment(sketch, "E1158", {"start": v(-20.29, 15.54) * mm, "end": v(-20.3, 15.37) * mm});
            skLineSegment(sketch, "E1159", {"start": v(-20.3, 15.37) * mm, "end": v(-20.32, 15.2) * mm});
            skLineSegment(sketch, "E1160", {"start": v(-20.32, 15.2) * mm, "end": v(-20.33, 15.01) * mm});
            skLineSegment(sketch, "E1161", {"start": v(-20.33, 15.01) * mm, "end": v(-20.26, 14.26) * mm});
            skLineSegment(sketch, "E1162", {"start": v(-20.26, 14.26) * mm, "end": v(-19.98, 13.67) * mm});
            skLineSegment(sketch, "E1163", {"start": v(-19.98, 13.67) * mm, "end": v(-19.49, 13.25) * mm});
            skLineSegment(sketch, "E1164", {"start": v(-19.49, 13.25) * mm, "end": v(-18.78, 13) * mm});
            skLineSegment(sketch, "E1165", {"start": v(-18.78, 13) * mm, "end": v(-18.38, 12.93) * mm});
            skLineSegment(sketch, "E1166", {"start": v(-18.38, 12.93) * mm, "end": v(-17.98, 12.9) * mm});
            skLineSegment(sketch, "E1167", {"start": v(-17.98, 12.9) * mm, "end": v(-17.58, 12.85) * mm});
            skLineSegment(sketch, "E1168", {"start": v(-17.58, 12.85) * mm, "end": v(-17.18, 12.8) * mm});
            skLineSegment(sketch, "E1169", {"start": v(-17.18, 12.8) * mm, "end": v(-16.36, 12.86) * mm});
            skLineSegment(sketch, "E1170", {"start": v(-16.36, 12.86) * mm, "end": v(-15.68, 13.16) * mm});
            skLineSegment(sketch, "E1171", {"start": v(-15.68, 13.16) * mm, "end": v(-15.07, 13.62) * mm});
            skLineSegment(sketch, "E1172", {"start": v(-15.07, 13.62) * mm, "end": v(-14.5, 14.15) * mm});
            skLineSegment(sketch, "E1173", {"start": v(-14.5, 14.15) * mm, "end": v(-14.46, 14.22) * mm});
            skLineSegment(sketch, "E1174", {"start": v(-14.46, 14.22) * mm, "end": v(-14.43, 14.3) * mm});
            skLineSegment(sketch, "E1175", {"start": v(-14.43, 14.3) * mm, "end": v(-14.41, 14.4) * mm});
            skLineSegment(sketch, "E1176", {"start": v(-14.41, 14.4) * mm, "end": v(-14.41, 14.48) * mm});
            skLineSegment(sketch, "E1177", {"start": v(-14.41, 14.48) * mm, "end": v(-14.6, 15) * mm});
            skLineSegment(sketch, "E1178", {"start": v(-14.6, 15) * mm, "end": v(-15.03, 15.46) * mm});
            skLineSegment(sketch, "E1179", {"start": v(-15.03, 15.46) * mm, "end": v(-15.57, 15.78) * mm});
            skLineSegment(sketch, "E1180", {"start": v(-15.57, 15.78) * mm, "end": v(-16.13, 15.88) * mm});
            skLineSegment(sketch, "E1181", {"start": v(-16.13, 15.88) * mm, "end": v(-16.5, 15.8) * mm});
            skLineSegment(sketch, "E1182", {"start": v(-16.5, 15.8) * mm, "end": v(-16.7, 15.64) * mm});
            skLineSegment(sketch, "E1183", {"start": v(-16.7, 15.64) * mm, "end": v(-16.74, 15.38) * mm});
            skLineSegment(sketch, "E1184", {"start": v(-16.74, 15.38) * mm, "end": v(-16.62, 15.02) * mm});
            skLineSegment(sketch, "E1185", {"start": v(-16.62, 15.02) * mm, "end": v(-16.55, 14.88) * mm});
            skLineSegment(sketch, "E1186", {"start": v(-16.55, 14.88) * mm, "end": v(-16.47, 14.73) * mm});
            skLineSegment(sketch, "E1187", {"start": v(-16.47, 14.73) * mm, "end": v(-16.4, 14.58) * mm});
            skLineSegment(sketch, "E1188", {"start": v(-16.4, 14.58) * mm, "end": v(-16.32, 14.41) * mm});
            skLineSegment(sketch, "E1189", {"start": v(-16.32, 14.41) * mm, "end": v(-16.85, 14.25) * mm});
            skLineSegment(sketch, "E1190", {"start": v(-16.85, 14.25) * mm, "end": v(-17.37, 14.17) * mm});
            skLineSegment(sketch, "E1191", {"start": v(-17.37, 14.17) * mm, "end": v(-17.89, 14.19) * mm});
            skLineSegment(sketch, "E1192", {"start": v(-17.89, 14.19) * mm, "end": v(-18.4, 14.3) * mm});
            skLineSegment(sketch, "E1193", {"start": v(-18.4, 14.3) * mm, "end": v(-18.8, 14.57) * mm});
            skLineSegment(sketch, "E1194", {"start": v(-18.8, 14.57) * mm, "end": v(-18.97, 15.03) * mm});
            skLineSegment(sketch, "E1195", {"start": v(-18.97, 15.03) * mm, "end": v(-18.9, 15.57) * mm});
            skLineSegment(sketch, "E1196", {"start": v(-18.9, 15.57) * mm, "end": v(-18.56, 16.07) * mm});
            skLineSegment(sketch, "E1197", {"start": v(-18.56, 16.07) * mm, "end": v(-17.96, 16.63) * mm});
            skLineSegment(sketch, "E1198", {"start": v(-17.96, 16.63) * mm, "end": v(-17.34, 17.18) * mm});
            skLineSegment(sketch, "E1199", {"start": v(-17.34, 17.18) * mm, "end": v(-16.72, 17.72) * mm});
            skLineSegment(sketch, "E1200", {"start": v(-16.72, 17.72) * mm, "end": v(-16.1, 18.26) * mm});
            skLineSegment(sketch, "E1201", {"start": v(-16.1, 18.26) * mm, "end": v(-16.07, 18.28) * mm});
            skLineSegment(sketch, "E1202", {"start": v(-16.07, 18.28) * mm, "end": v(-16.05, 18.3) * mm});
            skLineSegment(sketch, "E1203", {"start": v(-16.05, 18.3) * mm, "end": v(-16.02, 18.32) * mm});
            skLineSegment(sketch, "E1204", {"start": v(-16.02, 18.32) * mm, "end": v(-16, 18.34) * mm});
            skLineSegment(sketch, "E1205", {"start": v(-16, 18.34) * mm, "end": v(-15.92, 18.53) * mm});
            skLineSegment(sketch, "E1206", {"start": v(-15.92, 18.53) * mm, "end": v(-15.83, 18.71) * mm});
            skLineSegment(sketch, "E1207", {"start": v(-15.83, 18.71) * mm, "end": v(-15.75, 18.9) * mm});
            skLineSegment(sketch, "E1208", {"start": v(-15.75, 18.9) * mm, "end": v(-15.66, 19.09) * mm});
            skLineSegment(sketch, "E1209", {"start": v(-15.66, 19.09) * mm, "end": v(-15.88, 19.12) * mm});
            skLineSegment(sketch, "E1210", {"start": v(-15.88, 19.12) * mm, "end": v(-16.09, 19.15) * mm});
            skLineSegment(sketch, "E1211", {"start": v(-16.09, 19.15) * mm, "end": v(-16.3, 19.17) * mm});
            skLineSegment(sketch, "E1212", {"start": v(-16.3, 19.17) * mm, "end": v(-16.5, 19.16) * mm});
            skLineSegment(sketch, "E1213", {"start": v(-16.5, 19.16) * mm, "end": v(-16.71, 19.1) * mm});
            skLineSegment(sketch, "E1214", {"start": v(-16.71, 19.1) * mm, "end": v(-16.93, 19.02) * mm});
            skLineSegment(sketch, "E1215", {"start": v(-16.93, 19.02) * mm, "end": v(-17.14, 18.91) * mm});
            skLineSegment(sketch, "E1216", {"start": v(-17.14, 18.91) * mm, "end": v(-17.37, 18.8) * mm});
            skLineSegment(sketch, "E1217", {"start": v(-17.37, 18.8) * mm, "end": v(-17.52, 19.14) * mm});
            skLineSegment(sketch, "E1218", {"start": v(-17.52, 19.14) * mm, "end": v(-17.67, 19.47) * mm});
            skLineSegment(sketch, "E1219", {"start": v(-17.67, 19.47) * mm, "end": v(-17.82, 19.8) * mm});
            skLineSegment(sketch, "E1220", {"start": v(-17.82, 19.8) * mm, "end": v(-17.98, 20.1) * mm});
            skLineSegment(sketch, "E1221", {"start": v(-17.98, 20.1) * mm, "end": v(-18.38, 20.78) * mm});
            skLineSegment(sketch, "E1222", {"start": v(-18.38, 20.78) * mm, "end": v(-18.87, 21.37) * mm});
            skLineSegment(sketch, "E1223", {"start": v(-18.87, 21.37) * mm, "end": v(-19.47, 21.84) * mm});
            skLineSegment(sketch, "E1224", {"start": v(-19.47, 21.84) * mm, "end": v(-20.2, 22.18) * mm});
            skLineSegment(sketch, "E1225", {"start": v(-20.2, 22.18) * mm, "end": v(-20.52, 22.35) * mm});
            skLineSegment(sketch, "E1226", {"start": v(-20.52, 22.35) * mm, "end": v(-20.66, 22.6) * mm});
            skLineSegment(sketch, "E1227", {"start": v(-20.66, 22.6) * mm, "end": v(-20.62, 22.9) * mm});
            skLineSegment(sketch, "E1228", {"start": v(-20.62, 22.9) * mm, "end": v(-20.4, 23.27) * mm});
            skLineSegment(sketch, "E1229", {"start": v(-20.4, 23.27) * mm, "end": v(-19.58, 24.26) * mm});
            skLineSegment(sketch, "E1230", {"start": v(-19.58, 24.26) * mm, "end": v(-18.67, 25.16) * mm});
            skLineSegment(sketch, "E1231", {"start": v(-18.67, 25.16) * mm, "end": v(-17.7, 25.99) * mm});
            skLineSegment(sketch, "E1232", {"start": v(-17.7, 25.99) * mm, "end": v(-16.66, 26.77) * mm});
            skLineSegment(sketch, "E1233", {"start": v(-16.66, 26.77) * mm, "end": v(-14.77, 27.8) * mm});
            skLineSegment(sketch, "E1234", {"start": v(-14.77, 27.8) * mm, "end": v(-12.8, 28.34) * mm});
            skLineSegment(sketch, "E1235", {"start": v(-12.8, 28.34) * mm, "end": v(-10.75, 28.5) * mm});
            skLineSegment(sketch, "E1236", {"start": v(-10.75, 28.5) * mm, "end": v(-8.64, 28.4) * mm});
            skLineSegment(sketch, "E1237", {"start": v(-8.64, 28.4) * mm, "end": v(-7.49, 28.21) * mm});
            skLineSegment(sketch, "E1238", {"start": v(-7.49, 28.21) * mm, "end": v(-6.43, 27.86) * mm});
            skLineSegment(sketch, "E1239", {"start": v(-6.43, 27.86) * mm, "end": v(-5.46, 27.32) * mm});
            skLineSegment(sketch, "E1240", {"start": v(-5.46, 27.32) * mm, "end": v(-4.58, 26.6) * mm});
            skLineSegment(sketch, "E1241", {"start": v(-4.58, 26.6) * mm, "end": v(-3.58, 25.5) * mm});
            skLineSegment(sketch, "E1242", {"start": v(-3.58, 25.5) * mm, "end": v(-2.78, 24.3) * mm});
            skLineSegment(sketch, "E1243", {"start": v(-2.78, 24.3) * mm, "end": v(-2.19, 22.97) * mm});
            skLineSegment(sketch, "E1244", {"start": v(-2.19, 22.97) * mm, "end": v(-1.82, 21.53) * mm});
            skLineSegment(sketch, "E1245", {"start": v(-1.82, 21.53) * mm, "end": v(-1.77, 21.05) * mm});
            skLineSegment(sketch, "E1246", {"start": v(-1.77, 21.05) * mm, "end": v(-1.76, 20.56) * mm});
            skLineSegment(sketch, "E1247", {"start": v(-1.76, 20.56) * mm, "end": v(-1.78, 20.07) * mm});
            skLineSegment(sketch, "E1248", {"start": v(-1.78, 20.07) * mm, "end": v(-1.8, 19.58) * mm});
            skLineSegment(sketch, "E1249", {"start": v(-1.8, 19.58) * mm, "end": v(-1.8, 18.57) * mm});
            skLineSegment(sketch, "E1250", {"start": v(-1.8, 18.57) * mm, "end": v(-1.82, 17.57) * mm});
            skLineSegment(sketch, "E1251", {"start": v(-1.82, 17.57) * mm, "end": v(-1.85, 16.57) * mm});
            skLineSegment(sketch, "E1252", {"start": v(-1.85, 16.57) * mm, "end": v(-1.92, 15.57) * mm});
            skLineSegment(sketch, "E1253", {"start": v(-1.92, 15.57) * mm, "end": v(-2.05, 13.6) * mm});
            skLineSegment(sketch, "E1254", {"start": v(-2.05, 13.6) * mm, "end": v(-2.08, 11.63) * mm});
            skLineSegment(sketch, "E1255", {"start": v(-2.08, 11.63) * mm, "end": v(-2.05, 9.67) * mm});
            skLineSegment(sketch, "E1256", {"start": v(-2.05, 9.67) * mm, "end": v(-2.02, 7.7) * mm});
            skLineSegment(sketch, "E1257", {"start": v(-2.02, 7.7) * mm, "end": v(-1.94, 6.64) * mm});
            skLineSegment(sketch, "E1258", {"start": v(-1.94, 6.64) * mm, "end": v(-1.76, 5.58) * mm});
            skLineSegment(sketch, "E1259", {"start": v(-1.76, 5.58) * mm, "end": v(-1.54, 4.51) * mm});
            skLineSegment(sketch, "E1260", {"start": v(-1.54, 4.51) * mm, "end": v(-1.31, 3.46) * mm});
            skLineSegment(sketch, "E1261", {"start": v(-1.31, 3.46) * mm, "end": v(-1.04, 2.05) * mm});
            skLineSegment(sketch, "E1262", {"start": v(-1.04, 2.05) * mm, "end": v(-0.75, 0.64) * mm});
            skLineSegment(sketch, "E1263", {"start": v(-0.75, 0.64) * mm, "end": v(-0.45, -0.76) * mm});
            skLineSegment(sketch, "E1264", {"start": v(-0.45, -0.76) * mm, "end": v(-0.14, -2.17) * mm});
            skLineSegment(sketch, "E1265", {"start": v(-0.14, -2.17) * mm, "end": v(-0.06, -2.39) * mm});
            skLineSegment(sketch, "E1266", {"start": v(-0.06, -2.39) * mm, "end": v(0.08, -2.6) * mm});
            skLineSegment(sketch, "E1267", {"start": v(0.08, -2.6) * mm, "end": v(0.24, -2.8) * mm});
            skLineSegment(sketch, "E1268", {"start": v(0.24, -2.8) * mm, "end": v(0.4, -2.98) * mm});
            skLineSegment(sketch, "E1269", {"start": v(0.4, -2.98) * mm, "end": v(0.5, -3.04) * mm});
            skLineSegment(sketch, "E1270", {"start": v(0.5, -3.04) * mm, "end": v(0.64, -3.07) * mm});
            skLineSegment(sketch, "E1271", {"start": v(0.64, -3.07) * mm, "end": v(0.77, -3.07) * mm});
            skLineSegment(sketch, "E1272", {"start": v(0.77, -3.07) * mm, "end": v(0.88, -3.04) * mm});
            skLineSegment(sketch, "E1273", {"start": v(0.88, -3.04) * mm, "end": v(0.95, -2.96) * mm});
            skLineSegment(sketch, "E1274", {"start": v(0.95, -2.96) * mm, "end": v(1, -2.84) * mm});
            skLineSegment(sketch, "E1275", {"start": v(1, -2.84) * mm, "end": v(1.03, -2.71) * mm});
            skLineSegment(sketch, "E1276", {"start": v(1.03, -2.71) * mm, "end": v(1.06, -2.58) * mm});
            skLineSegment(sketch, "E1277", {"start": v(1.06, -2.58) * mm, "end": v(1.06, -2.51) * mm});
            skLineSegment(sketch, "E1278", {"start": v(1.06, -2.51) * mm, "end": v(1.04, -2.44) * mm});
            skLineSegment(sketch, "E1279", {"start": v(1.04, -2.44) * mm, "end": v(1.01, -2.36) * mm});
            skLineSegment(sketch, "E1280", {"start": v(1.01, -2.36) * mm, "end": v(1, -2.3) * mm});
            skLineSegment(sketch, "E1281", {"start": v(1, -2.3) * mm, "end": v(0.96, -1.78) * mm});
            skLineSegment(sketch, "E1282", {"start": v(0.96, -1.78) * mm, "end": v(1.06, -1.32) * mm});
            skLineSegment(sketch, "E1283", {"start": v(1.06, -1.32) * mm, "end": v(1.3, -0.91) * mm});
            skLineSegment(sketch, "E1284", {"start": v(1.3, -0.91) * mm, "end": v(1.66, -0.55) * mm});
            skLineSegment(sketch, "E1285", {"start": v(1.66, -0.55) * mm, "end": v(2.84, 0.22) * mm});
            skLineSegment(sketch, "E1286", {"start": v(2.84, 0.22) * mm, "end": v(4.1, 0.8) * mm});
            skLineSegment(sketch, "E1287", {"start": v(4.1, 0.8) * mm, "end": v(5.42, 1.15) * mm});
            skLineSegment(sketch, "E1288", {"start": v(5.42, 1.15) * mm, "end": v(6.82, 1.3) * mm});
            skLineSegment(sketch, "E1289", {"start": v(6.82, 1.3) * mm, "end": v(7.48, 1.32) * mm});
            skLineSegment(sketch, "E1290", {"start": v(7.48, 1.32) * mm, "end": v(8.14, 1.33) * mm});
            skLineSegment(sketch, "E1291", {"start": v(8.14, 1.33) * mm, "end": v(8.8, 1.32) * mm});
            skLineSegment(sketch, "E1292", {"start": v(8.8, 1.32) * mm, "end": v(9.46, 1.31) * mm});
            skLineSegment(sketch, "E1293", {"start": v(9.46, 1.31) * mm, "end": v(9.84, 1.28) * mm});
            skLineSegment(sketch, "E1294", {"start": v(9.84, 1.28) * mm, "end": v(10.19, 1.19) * mm});
            skLineSegment(sketch, "E1295", {"start": v(10.19, 1.19) * mm, "end": v(10.48, 0.98) * mm});
            skLineSegment(sketch, "E1296", {"start": v(10.48, 0.98) * mm, "end": v(10.67, 0.63) * mm});
            skLineSegment(sketch, "E1297", {"start": v(10.67, 0.63) * mm, "end": v(10.67, 0.3) * mm});
            skLineSegment(sketch, "E1298", {"start": v(10.67, 0.3) * mm, "end": v(10.53, -0.1) * mm});
            skLineSegment(sketch, "E1299", {"start": v(10.53, -0.1) * mm, "end": v(10.26, -0.45) * mm});
            skLineSegment(sketch, "E1300", {"start": v(10.26, -0.45) * mm, "end": v(9.93, -0.7) * mm});
            skLineSegment(sketch, "E1301", {"start": v(9.93, -0.7) * mm, "end": v(9, -1.06) * mm});
            skLineSegment(sketch, "E1302", {"start": v(9, -1.06) * mm, "end": v(8.05, -1.23) * mm});
            skLineSegment(sketch, "E1303", {"start": v(8.05, -1.23) * mm, "end": v(7.1, -1.17) * mm});
            skLineSegment(sketch, "E1304", {"start": v(7.1, -1.17) * mm, "end": v(6.12, -0.84) * mm});
            skLineSegment(sketch, "E1305", {"start": v(6.12, -0.84) * mm, "end": v(5.85, -0.72) * mm});
            skLineSegment(sketch, "E1306", {"start": v(5.85, -0.72) * mm, "end": v(5.57, -0.62) * mm});
            skLineSegment(sketch, "E1307", {"start": v(5.57, -0.62) * mm, "end": v(5.28, -0.55) * mm});
            skLineSegment(sketch, "E1308", {"start": v(5.28, -0.55) * mm, "end": v(5, -0.48) * mm});
            skLineSegment(sketch, "E1309", {"start": v(5, -0.48) * mm, "end": v(4.89, -0.48) * mm});
            skLineSegment(sketch, "E1310", {"start": v(4.89, -0.48) * mm, "end": v(4.77, -0.52) * mm});
            skLineSegment(sketch, "E1311", {"start": v(4.77, -0.52) * mm, "end": v(4.67, -0.58) * mm});
            skLineSegment(sketch, "E1312", {"start": v(4.67, -0.58) * mm, "end": v(4.6, -0.66) * mm});
            skLineSegment(sketch, "E1313", {"start": v(4.6, -0.66) * mm, "end": v(4.58, -0.75) * mm});
            skLineSegment(sketch, "E1314", {"start": v(4.58, -0.75) * mm, "end": v(4.6, -0.87) * mm});
            skLineSegment(sketch, "E1315", {"start": v(4.6, -0.87) * mm, "end": v(4.63, -0.99) * mm});
            skLineSegment(sketch, "E1316", {"start": v(4.63, -0.99) * mm, "end": v(4.68, -1.1) * mm});
            skLineSegment(sketch, "E1317", {"start": v(4.68, -1.1) * mm, "end": v(4.74, -1.19) * mm});
            skLineSegment(sketch, "E1318", {"start": v(4.74, -1.19) * mm, "end": v(4.83, -1.27) * mm});
            skLineSegment(sketch, "E1319", {"start": v(4.83, -1.27) * mm, "end": v(4.92, -1.36) * mm});
            skLineSegment(sketch, "E1320", {"start": v(4.92, -1.36) * mm, "end": v(5, -1.44) * mm});
            skLineSegment(sketch, "E1321", {"start": v(5, -1.44) * mm, "end": v(5.42, -1.88) * mm});
            skLineSegment(sketch, "E1322", {"start": v(5.42, -1.88) * mm, "end": v(5.54, -2.19) * mm});
            skLineSegment(sketch, "E1323", {"start": v(5.54, -2.19) * mm, "end": v(5.38, -2.47) * mm});
            skLineSegment(sketch, "E1324", {"start": v(5.38, -2.47) * mm, "end": v(4.9, -2.83) * mm});
            skLineSegment(sketch, "E1325", {"start": v(4.9, -2.83) * mm, "end": v(4.63, -3.02) * mm});
            skLineSegment(sketch, "E1326", {"start": v(4.63, -3.02) * mm, "end": v(4.35, -3.22) * mm});
            skLineSegment(sketch, "E1327", {"start": v(4.35, -3.22) * mm, "end": v(4.07, -3.43) * mm});
            skLineSegment(sketch, "E1328", {"start": v(4.07, -3.43) * mm, "end": v(3.8, -3.64) * mm});
            skLineSegment(sketch, "E1329", {"start": v(3.8, -3.64) * mm, "end": v(3.7, -3.73) * mm});
            skLineSegment(sketch, "E1330", {"start": v(3.7, -3.73) * mm, "end": v(3.6, -3.83) * mm});
            skLineSegment(sketch, "E1331", {"start": v(3.6, -3.83) * mm, "end": v(3.51, -3.93) * mm});
            skLineSegment(sketch, "E1332", {"start": v(3.51, -3.93) * mm, "end": v(3.47, -4.05) * mm});
            skLineSegment(sketch, "E1333", {"start": v(3.47, -4.05) * mm, "end": v(3.44, -4.22) * mm});
            skLineSegment(sketch, "E1334", {"start": v(3.44, -4.22) * mm, "end": v(3.44, -4.4) * mm});
            skLineSegment(sketch, "E1335", {"start": v(3.44, -4.4) * mm, "end": v(3.47, -4.58) * mm});
            skLineSegment(sketch, "E1336", {"start": v(3.47, -4.58) * mm, "end": v(3.54, -4.7) * mm});
            skLineSegment(sketch, "E1337", {"start": v(3.54, -4.7) * mm, "end": v(3.65, -4.75) * mm});
            skLineSegment(sketch, "E1338", {"start": v(3.65, -4.75) * mm, "end": v(3.81, -4.75) * mm});
            skLineSegment(sketch, "E1339", {"start": v(3.81, -4.75) * mm, "end": v(4, -4.72) * mm});
            skLineSegment(sketch, "E1340", {"start": v(4, -4.72) * mm, "end": v(4.18, -4.69) * mm});
            skLineSegment(sketch, "E1341", {"start": v(4.18, -4.69) * mm, "end": v(4.23, -4.67) * mm});
            skLineSegment(sketch, "E1342", {"start": v(4.23, -4.67) * mm, "end": v(4.29, -4.64) * mm});
            skLineSegment(sketch, "E1343", {"start": v(4.29, -4.64) * mm, "end": v(4.33, -4.6) * mm});
            skLineSegment(sketch, "E1344", {"start": v(4.33, -4.6) * mm, "end": v(4.38, -4.56) * mm});
            skLineSegment(sketch, "E1345", {"start": v(4.38, -4.56) * mm, "end": v(5.34, -3.73) * mm});
            skLineSegment(sketch, "E1346", {"start": v(5.34, -3.73) * mm, "end": v(6.44, -3.18) * mm});
            skLineSegment(sketch, "E1347", {"start": v(6.44, -3.18) * mm, "end": v(7.61, -2.82) * mm});
            skLineSegment(sketch, "E1348", {"start": v(7.61, -2.82) * mm, "end": v(8.82, -2.54) * mm});
            skLineSegment(sketch, "E1349", {"start": v(8.82, -2.54) * mm, "end": v(9.09, -2.49) * mm});
            skLineSegment(sketch, "E1350", {"start": v(9.09, -2.49) * mm, "end": v(9.36, -2.46) * mm});
            skLineSegment(sketch, "E1351", {"start": v(9.36, -2.46) * mm, "end": v(9.63, -2.45) * mm});
            skLineSegment(sketch, "E1352", {"start": v(9.63, -2.45) * mm, "end": v(9.9, -2.48) * mm});
            skLineSegment(sketch, "E1353", {"start": v(9.9, -2.48) * mm, "end": v(11.2, -2.72) * mm});
            skLineSegment(sketch, "E1354", {"start": v(11.2, -2.72) * mm, "end": v(12.52, -2.95) * mm});
            skLineSegment(sketch, "E1355", {"start": v(12.52, -2.95) * mm, "end": v(13.82, -3.23) * mm});
            skLineSegment(sketch, "E1356", {"start": v(13.82, -3.23) * mm, "end": v(15.08, -3.62) * mm});
            skLineSegment(sketch, "E1357", {"start": v(15.08, -3.62) * mm, "end": v(17.26, -5.01) * mm});
            skLineSegment(sketch, "E1358", {"start": v(17.26, -5.01) * mm, "end": v(18.47, -7.03) * mm});
            skLineSegment(sketch, "E1359", {"start": v(18.47, -7.03) * mm, "end": v(18.63, -9.4) * mm});
            skLineSegment(sketch, "E1360", {"start": v(18.63, -9.4) * mm, "end": v(17.68, -11.84) * mm});
            skLineSegment(sketch, "E1361", {"start": v(17.68, -11.84) * mm, "end": v(16.59, -13.3) * mm});
            skLineSegment(sketch, "E1362", {"start": v(16.59, -13.3) * mm, "end": v(15.34, -14.6) * mm});
            skLineSegment(sketch, "E1363", {"start": v(15.34, -14.6) * mm, "end": v(13.95, -15.75) * mm});
            skLineSegment(sketch, "E1364", {"start": v(13.95, -15.75) * mm, "end": v(12.43, -16.76) * mm});
            skLineSegment(sketch, "E1365", {"start": v(12.43, -16.76) * mm, "end": v(11, -17.41) * mm});
            skLineSegment(sketch, "E1366", {"start": v(11, -17.41) * mm, "end": v(9.53, -17.74) * mm});
            skLineSegment(sketch, "E1367", {"start": v(9.53, -17.74) * mm, "end": v(8, -17.78) * mm});
            skLineSegment(sketch, "E1368", {"start": v(8, -17.78) * mm, "end": v(6.45, -17.59) * mm});
            skLineSegment(sketch, "E1369", {"start": v(6.45, -17.59) * mm, "end": v(6.3, -17.56) * mm});
            skLineSegment(sketch, "E1370", {"start": v(6.3, -17.56) * mm, "end": v(6.13, -17.53) * mm});
            skLineSegment(sketch, "E1371", {"start": v(6.13, -17.53) * mm, "end": v(5.97, -17.51) * mm});
            skLineSegment(sketch, "E1372", {"start": v(5.97, -17.51) * mm, "end": v(5.8, -17.5) * mm});
            skLineSegment(sketch, "E1373", {"start": v(5.8, -17.5) * mm, "end": v(5.34, -17.58) * mm});
            skLineSegment(sketch, "E1374", {"start": v(5.34, -17.58) * mm, "end": v(5, -17.81) * mm});
            skLineSegment(sketch, "E1375", {"start": v(5, -17.81) * mm, "end": v(4.8, -18.18) * mm});
            skLineSegment(sketch, "E1376", {"start": v(4.8, -18.18) * mm, "end": v(4.73, -18.65) * mm});
            skLineSegment(sketch, "E1377", {"start": v(4.73, -18.65) * mm, "end": v(4.75, -19.51) * mm});
            skLineSegment(sketch, "E1378", {"start": v(4.75, -19.51) * mm, "end": v(4.75, -20.38) * mm});
            skLineSegment(sketch, "E1379", {"start": v(4.75, -20.38) * mm, "end": v(4.74, -21.25) * mm});
            skLineSegment(sketch, "E1380", {"start": v(4.74, -21.25) * mm, "end": v(4.74, -22.12) * mm});
            skLineSegment(sketch, "E1381", {"start": v(4.74, -22.12) * mm, "end": v(4.73, -23.14) * mm});
            skLineSegment(sketch, "E1382", {"start": v(4.73, -23.14) * mm, "end": v(4.71, -24.16) * mm});
            skLineSegment(sketch, "E1383", {"start": v(4.71, -24.16) * mm, "end": v(4.7, -25.18) * mm});
            skLineSegment(sketch, "E1384", {"start": v(4.7, -25.18) * mm, "end": v(4.67, -26.2) * mm});
            skLineSegment(sketch, "E1385", {"start": v(4.67, -26.2) * mm, "end": v(4.66, -26.37) * mm});
            skLineSegment(sketch, "E1386", {"start": v(4.66, -26.37) * mm, "end": v(4.64, -26.55) * mm});
            skLineSegment(sketch, "E1387", {"start": v(4.64, -26.55) * mm, "end": v(4.62, -26.73) * mm});
            skLineSegment(sketch, "E1388", {"start": v(4.62, -26.73) * mm, "end": v(4.58, -26.9) * mm});
            skLineSegment(sketch, "E1389", {"start": v(4.58, -26.9) * mm, "end": v(4.37, -27.37) * mm});
            skLineSegment(sketch, "E1390", {"start": v(4.37, -27.37) * mm, "end": v(4.04, -27.64) * mm});
            skLineSegment(sketch, "E1391", {"start": v(4.04, -27.64) * mm, "end": v(3.63, -27.69) * mm});
            skLineSegment(sketch, "E1392", {"start": v(3.63, -27.69) * mm, "end": v(3.17, -27.49) * mm});
            skLineSegment(sketch, "E1393", {"start": v(3.17, -27.49) * mm, "end": v(2.1, -26.71) * mm});
            skLineSegment(sketch, "E1394", {"start": v(2.1, -26.71) * mm, "end": v(1.05, -25.92) * mm});
            skLineSegment(sketch, "E1395", {"start": v(1.05, -25.92) * mm, "end": v(0, -25.12) * mm});
            skLineSegment(sketch, "E1396", {"start": v(0, -25.12) * mm, "end": v(-1.03, -24.31) * mm});
            skLineSegment(sketch, "E1397", {"start": v(-1.03, -24.31) * mm, "end": v(-1.2, -24.14) * mm});
            skLineSegment(sketch, "E1398", {"start": v(-1.2, -24.14) * mm, "end": v(-1.34, -23.93) * mm});
            skLineSegment(sketch, "E1399", {"start": v(-1.34, -23.93) * mm, "end": v(-1.45, -23.7) * mm});
            skLineSegment(sketch, "E1400", {"start": v(-1.45, -23.7) * mm, "end": v(-1.53, -23.46) * mm});
            skLineSegment(sketch, "E1401", {"start": v(-1.53, -23.46) * mm, "end": v(-1.55, -23.3) * mm});
            skLineSegment(sketch, "E1402", {"start": v(-1.55, -23.3) * mm, "end": v(-1.52, -23.12) * mm});
            skLineSegment(sketch, "E1403", {"start": v(-1.52, -23.12) * mm, "end": v(-1.45, -22.95) * mm});
            skLineSegment(sketch, "E1404", {"start": v(-1.45, -22.95) * mm, "end": v(-1.36, -22.84) * mm});
            skLineSegment(sketch, "E1405", {"start": v(-1.36, -22.84) * mm, "end": v(-1.22, -22.8) * mm});
            skLineSegment(sketch, "E1406", {"start": v(-1.22, -22.8) * mm, "end": v(-1.05, -22.8) * mm});
            skLineSegment(sketch, "E1407", {"start": v(-1.05, -22.8) * mm, "end": v(-0.87, -22.84) * mm});
            skLineSegment(sketch, "E1408", {"start": v(-0.87, -22.84) * mm, "end": v(-0.7, -22.9) * mm});
            skLineSegment(sketch, "E1409", {"start": v(-0.7, -22.9) * mm, "end": v(-0.12, -23.24) * mm});
            skLineSegment(sketch, "E1410", {"start": v(-0.12, -23.24) * mm, "end": v(0.45, -23.58) * mm});
            skLineSegment(sketch, "E1411", {"start": v(0.45, -23.58) * mm, "end": v(1.03, -23.93) * mm});
            skLineSegment(sketch, "E1412", {"start": v(1.03, -23.93) * mm, "end": v(1.62, -24.26) * mm});
            skLineSegment(sketch, "E1413", {"start": v(1.62, -24.26) * mm, "end": v(2.24, -24.48) * mm});
            skLineSegment(sketch, "E1414", {"start": v(2.24, -24.48) * mm, "end": v(2.72, -24.4) * mm});
            skLineSegment(sketch, "E1415", {"start": v(2.72, -24.4) * mm, "end": v(3.02, -24.01) * mm});
            skLineSegment(sketch, "E1416", {"start": v(3.02, -24.01) * mm, "end": v(3.13, -23.35) * mm});
            skLineSegment(sketch, "E1417", {"start": v(3.13, -23.35) * mm, "end": v(3.12, -22.35) * mm});
            skLineSegment(sketch, "E1418", {"start": v(3.12, -22.35) * mm, "end": v(3.12, -21.34) * mm});
            skLineSegment(sketch, "E1419", {"start": v(3.12, -21.34) * mm, "end": v(3.11, -20.34) * mm});
            skLineSegment(sketch, "E1420", {"start": v(3.11, -20.34) * mm, "end": v(3.1, -19.33) * mm});
            skLineSegment(sketch, "E1421", {"start": v(3.1, -19.33) * mm, "end": v(3, -18.72) * mm});
            skLineSegment(sketch, "E1422", {"start": v(3, -18.72) * mm, "end": v(2.73, -18.32) * mm});
            skLineSegment(sketch, "E1423", {"start": v(2.73, -18.32) * mm, "end": v(2.3, -18.13) * mm});
            skLineSegment(sketch, "E1424", {"start": v(2.3, -18.13) * mm, "end": v(1.68, -18.15) * mm});
            skLineSegment(sketch, "E1425", {"start": v(1.68, -18.15) * mm, "end": v(0.57, -18.35) * mm});
            skLineSegment(sketch, "E1426", {"start": v(0.57, -18.35) * mm, "end": v(-0.53, -18.55) * mm});
            skLineSegment(sketch, "E1427", {"start": v(-0.53, -18.55) * mm, "end": v(-1.64, -18.74) * mm});
            skLineSegment(sketch, "E1428", {"start": v(-1.64, -18.74) * mm, "end": v(-2.75, -18.9) * mm});
            skLineSegment(sketch, "E1429", {"start": v(-2.75, -18.9) * mm, "end": v(-3.26, -18.91) * mm});
            skLineSegment(sketch, "E1430", {"start": v(-3.26, -18.91) * mm, "end": v(-3.78, -18.87) * mm});
            skLineSegment(sketch, "E1431", {"start": v(-3.78, -18.87) * mm, "end": v(-4.3, -18.8) * mm});
            skLineSegment(sketch, "E1432", {"start": v(-4.3, -18.8) * mm, "end": v(-4.82, -18.72) * mm});
            skLineSegment(sketch, "E1433", {"start": v(-4.82, -18.72) * mm, "end": v(-7.22, -18.32) * mm});
            skLineSegment(sketch, "E1434", {"start": v(-7.22, -18.32) * mm, "end": v(-9.6, -17.8) * mm});
            skLineSegment(sketch, "E1435", {"start": v(-9.6, -17.8) * mm, "end": v(-11.91, -17.12) * mm});
            skLineSegment(sketch, "E1436", {"start": v(-11.91, -17.12) * mm, "end": v(-14.16, -16.22) * mm});
            skLineSegment(sketch, "E1437", {"start": v(-14.16, -16.22) * mm, "end": v(-16.15, -15.11) * mm});
            skLineSegment(sketch, "E1438", {"start": v(-16.15, -15.11) * mm, "end": v(-17.91, -13.74) * mm});
            skLineSegment(sketch, "E1439", {"start": v(-17.91, -13.74) * mm, "end": v(-19.44, -12.1) * mm});
            skLineSegment(sketch, "E1440", {"start": v(-19.44, -12.1) * mm, "end": v(-20.72, -10.19) * mm});
            skLineSegment(sketch, "E1441", {"start": v(-20.72, -10.19) * mm, "end": v(-21.98, -7.8) * mm});
            skLineSegment(sketch, "E1442", {"start": v(-21.98, -7.8) * mm, "end": v(-23.1, -5.36) * mm});
            skLineSegment(sketch, "E1443", {"start": v(-23.1, -5.36) * mm, "end": v(-24.05, -2.84) * mm});
            skLineSegment(sketch, "E1444", {"start": v(-24.05, -2.84) * mm, "end": v(-24.76, -0.23) * mm});
            skLineSegment(sketch, "E1445", {"start": v(-24.76, -0.23) * mm, "end": v(-24.96, 0.84) * mm});
            skLineSegment(sketch, "E1446", {"start": v(-24.96, 0.84) * mm, "end": v(-25.1, 1.91) * mm});
            skLineSegment(sketch, "E1447", {"start": v(-25.1, 1.91) * mm, "end": v(-25.14, 3) * mm});
            skLineSegment(sketch, "E1448", {"start": v(-25.14, 3) * mm, "end": v(-25.12, 4.1) * mm});
            skLineSegment(sketch, "E1449", {"start": v(-25.12, 4.1) * mm, "end": v(-25.08, 5.5) * mm});
            skLineSegment(sketch, "E1450", {"start": v(-25.08, 5.5) * mm, "end": v(-25.1, 6.9) * mm});
            skLineSegment(sketch, "E1451", {"start": v(-25.1, 6.9) * mm, "end": v(-25.16, 8.3) * mm});
            skLineSegment(sketch, "E1452", {"start": v(-25.16, 8.3) * mm, "end": v(-25.2, 9.7) * mm});
            skLineSegment(sketch, "E1453", {"start": v(-25.2, 9.7) * mm, "end": v(-25.17, 10.22) * mm});
            skLineSegment(sketch, "E1454", {"start": v(-25.17, 10.22) * mm, "end": v(-25.02, 10.53) * mm});
            skLineSegment(sketch, "E1455", {"start": v(-25.02, 10.53) * mm, "end": v(-24.72, 10.68) * mm});
            skLineSegment(sketch, "E1456", {"start": v(-24.72, 10.68) * mm, "end": v(-24.2, 10.73) * mm});
            skLineSegment(sketch, "E1457", {"start": v(-24.2, 10.73) * mm, "end": v(-22.58, 10.77) * mm});
            skLineSegment(sketch, "E1458", {"start": v(-22.58, 10.77) * mm, "end": v(-20.96, 10.81) * mm});
            skLineSegment(sketch, "E1459", {"start": v(-20.96, 10.81) * mm, "end": v(-19.34, 10.86) * mm});
            skLineSegment(sketch, "E1460", {"start": v(-19.34, 10.86) * mm, "end": v(-17.72, 10.93) * mm});
            skLineSegment(sketch, "E1461", {"start": v(-17.72, 10.93) * mm, "end": v(-16.4, 11) * mm});
            skLineSegment(sketch, "E1462", {"start": v(-16.4, 11) * mm, "end": v(-15.1, 11.06) * mm});
            skLineSegment(sketch, "E1463", {"start": v(-15.1, 11.06) * mm, "end": v(-13.78, 11.16) * mm});
            skLineSegment(sketch, "E1464", {"start": v(-13.78, 11.16) * mm, "end": v(-12.47, 11.3) * mm});
            skLineSegment(sketch, "E1465", {"start": v(-12.47, 11.3) * mm, "end": v(-10.9, 11.5) * mm});
            skLineSegment(sketch, "E1466", {"start": v(-10.9, 11.5) * mm, "end": v(-9.33, 11.73) * mm});
            skLineSegment(sketch, "E1467", {"start": v(-9.33, 11.73) * mm, "end": v(-7.76, 11.98) * mm});
            skLineSegment(sketch, "E1468", {"start": v(-7.76, 11.98) * mm, "end": v(-6.2, 12.24) * mm});
            skLineSegment(sketch, "E1469", {"start": v(-6.2, 12.24) * mm, "end": v(-6, 12.27) * mm});
            skLineSegment(sketch, "E1470", {"start": v(-6, 12.27) * mm, "end": v(-5.8, 12.33) * mm});
            skLineSegment(sketch, "E1471", {"start": v(-5.8, 12.33) * mm, "end": v(-5.63, 12.41) * mm});
            skLineSegment(sketch, "E1472", {"start": v(-5.63, 12.41) * mm, "end": v(-5.5, 12.53) * mm});
            skLineSegment(sketch, "E1473", {"start": v(-5.5, 12.53) * mm, "end": v(-5.37, 12.72) * mm});
            skLineSegment(sketch, "E1474", {"start": v(-5.37, 12.72) * mm, "end": v(-5.26, 12.95) * mm});
            skLineSegment(sketch, "E1475", {"start": v(-5.26, 12.95) * mm, "end": v(-5.21, 13.17) * mm});
            skLineSegment(sketch, "E1476", {"start": v(-5.21, 13.17) * mm, "end": v(-5.24, 13.34) * mm});
            skLineSegment(sketch, "E1477", {"start": v(-5.24, 13.34) * mm, "end": v(-5.37, 13.5) * mm});
            skLineSegment(sketch, "E1478", {"start": v(-5.37, 13.5) * mm, "end": v(-5.58, 13.64) * mm});
            skLineSegment(sketch, "E1479", {"start": v(-5.58, 13.64) * mm, "end": v(-5.82, 13.73) * mm});
            skLineSegment(sketch, "E1480", {"start": v(-5.82, 13.73) * mm, "end": v(-6.03, 13.74) * mm});
            skLineSegment(sketch, "E1481", {"start": v(-6.03, 13.74) * mm, "end": v(-7.35, 13.55) * mm});
            skLineSegment(sketch, "E1482", {"start": v(-7.35, 13.55) * mm, "end": v(-8.67, 13.35) * mm});
            skLineSegment(sketch, "E1483", {"start": v(-8.67, 13.35) * mm, "end": v(-9.98, 13.14) * mm});
            skLineSegment(sketch, "E1484", {"start": v(-9.98, 13.14) * mm, "end": v(-11.3, 12.93) * mm});
            skLineSegment(sketch, "E1485", {"start": v(-11.3, 12.93) * mm, "end": v(-13.72, 12.6) * mm});
            skLineSegment(sketch, "E1486", {"start": v(-13.72, 12.6) * mm, "end": v(-16.14, 12.34) * mm});
            skLineSegment(sketch, "E1487", {"start": v(-16.14, 12.34) * mm, "end": v(-18.57, 12.2) * mm});
            skLineSegment(sketch, "E1488", {"start": v(-18.57, 12.2) * mm, "end": v(-21.02, 12.2) * mm});
            skLineSegment(sketch, "E1489", {"start": v(-21.02, 12.2) * mm, "end": v(-21.67, 12.18) * mm});
            skLineSegment(sketch, "E1490", {"start": v(-21.67, 12.18) * mm, "end": v(-22.33, 12.12) * mm});
            skLineSegment(sketch, "E1491", {"start": v(-22.33, 12.12) * mm, "end": v(-22.98, 12.03) * mm});
            skLineSegment(sketch, "E1492", {"start": v(-22.98, 12.03) * mm, "end": v(-23.63, 11.93) * mm});
            skLineSegment(sketch, "E1493", {"start": v(-23.63, 11.93) * mm, "end": v(-24.18, 11.9) * mm});
            skLineSegment(sketch, "E1494", {"start": v(-24.18, 11.9) * mm, "end": v(-24.52, 12.03) * mm});
            skLineSegment(sketch, "E1495", {"start": v(-24.52, 12.03) * mm, "end": v(-24.67, 12.36) * mm});
            skLineSegment(sketch, "E1496", {"start": v(-24.67, 12.36) * mm, "end": v(-24.65, 12.91) * mm});
            skLineSegment(sketch, "E1497", {"start": v(-24.65, 12.91) * mm, "end": v(-24.59, 13.39) * mm});
            skLineSegment(sketch, "E1498", {"start": v(-24.59, 13.39) * mm, "end": v(-24.52, 13.86) * mm});
            skLineSegment(sketch, "E1499", {"start": v(-24.52, 13.86) * mm, "end": v(-24.44, 14.33) * mm});
            skLineSegment(sketch, "E1500", {"start": v(-24.44, 14.33) * mm, "end": v(-24.36, 14.8) * mm});
            skLineSegment(sketch, "E1501", {"start": v(-24.36, 14.8) * mm, "end": v(-24.23, 15.24) * mm});
            skLineSegment(sketch, "E1502", {"start": v(-24.23, 15.24) * mm, "end": v(-24, 15.53) * mm});
            skLineSegment(sketch, "E1503", {"start": v(-24, 15.53) * mm, "end": v(-23.65, 15.68) * mm});
            skLineSegment(sketch, "E1504", {"start": v(-23.65, 15.68) * mm, "end": v(-23.2, 15.73) * mm});
            skLineSegment(sketch, "E1505", {"start": v(-23.2, 15.73) * mm, "end": v(-22.48, 15.72) * mm});
            skLineSegment(sketch, "E1506", {"start": v(-22.48, 15.72) * mm, "end": v(-21.76, 15.72) * mm});
            skLineSegment(sketch, "E1507", {"start": v(-21.76, 15.72) * mm, "end": v(-21.02, 15.72) * mm});
            skLineSegment(sketch, "E1508", {"start": v(-21.02, 15.72) * mm, "end": v(-20.27, 15.72) * mm});
            skLineSegment(sketch, "E1509", {"start": v(-7.3, -8.74) * mm, "end": v(-7.43, -8.98) * mm});
            skLineSegment(sketch, "E1510", {"start": v(-7.43, -8.98) * mm, "end": v(-7.56, -9.22) * mm});
            skLineSegment(sketch, "E1511", {"start": v(-7.56, -9.22) * mm, "end": v(-7.7, -9.47) * mm});
            skLineSegment(sketch, "E1512", {"start": v(-7.7, -9.47) * mm, "end": v(-7.8, -9.72) * mm});
            skLineSegment(sketch, "E1513", {"start": v(-7.8, -9.72) * mm, "end": v(-7.96, -10.02) * mm});
            skLineSegment(sketch, "E1514", {"start": v(-7.96, -10.02) * mm, "end": v(-8.19, -10.22) * mm});
            skLineSegment(sketch, "E1515", {"start": v(-8.19, -10.22) * mm, "end": v(-8.46, -10.3) * mm});
            skLineSegment(sketch, "E1516", {"start": v(-8.46, -10.3) * mm, "end": v(-8.77, -10.24) * mm});
            skLineSegment(sketch, "E1517", {"start": v(-8.77, -10.24) * mm, "end": v(-9.03, -10.07) * mm});
            skLineSegment(sketch, "E1518", {"start": v(-9.03, -10.07) * mm, "end": v(-9.17, -9.85) * mm});
            skLineSegment(sketch, "E1519", {"start": v(-9.17, -9.85) * mm, "end": v(-9.18, -9.59) * mm});
            skLineSegment(sketch, "E1520", {"start": v(-9.18, -9.59) * mm, "end": v(-9.07, -9.3) * mm});
            skLineSegment(sketch, "E1521", {"start": v(-9.07, -9.3) * mm, "end": v(-8.86, -8.96) * mm});
            skLineSegment(sketch, "E1522", {"start": v(-8.86, -8.96) * mm, "end": v(-8.64, -8.61) * mm});
            skLineSegment(sketch, "E1523", {"start": v(-8.64, -8.61) * mm, "end": v(-8.4, -8.3) * mm});
            skLineSegment(sketch, "E1524", {"start": v(-8.4, -8.3) * mm, "end": v(-8.12, -8) * mm});
            skLineSegment(sketch, "E1525", {"start": v(-8.12, -8) * mm, "end": v(-7.57, -7.4) * mm});
            skLineSegment(sketch, "E1526", {"start": v(-7.57, -7.4) * mm, "end": v(-7.23, -6.71) * mm});
            skLineSegment(sketch, "E1527", {"start": v(-7.23, -6.71) * mm, "end": v(-7.08, -5.96) * mm});
            skLineSegment(sketch, "E1528", {"start": v(-7.08, -5.96) * mm, "end": v(-7.1, -5.15) * mm});
            skLineSegment(sketch, "E1529", {"start": v(-7.1, -5.15) * mm, "end": v(-7.2, -4.49) * mm});
            skLineSegment(sketch, "E1530", {"start": v(-7.2, -4.49) * mm, "end": v(-7.3, -3.82) * mm});
            skLineSegment(sketch, "E1531", {"start": v(-7.3, -3.82) * mm, "end": v(-7.37, -3.15) * mm});
            skLineSegment(sketch, "E1532", {"start": v(-7.37, -3.15) * mm, "end": v(-7.4, -2.48) * mm});
            skLineSegment(sketch, "E1533", {"start": v(-7.4, -2.48) * mm, "end": v(-7.36, -1.03) * mm});
            skLineSegment(sketch, "E1534", {"start": v(-7.36, -1.03) * mm, "end": v(-7.3, 0.42) * mm});
            skLineSegment(sketch, "E1535", {"start": v(-7.3, 0.42) * mm, "end": v(-7.23, 1.87) * mm});
            skLineSegment(sketch, "E1536", {"start": v(-7.23, 1.87) * mm, "end": v(-7.16, 3.32) * mm});
            skLineSegment(sketch, "E1537", {"start": v(-7.16, 3.32) * mm, "end": v(-7.17, 3.9) * mm});
            skLineSegment(sketch, "E1538", {"start": v(-7.17, 3.9) * mm, "end": v(-7.28, 4.45) * mm});
            skLineSegment(sketch, "E1539", {"start": v(-7.28, 4.45) * mm, "end": v(-7.52, 4.94) * mm});
            skLineSegment(sketch, "E1540", {"start": v(-7.52, 4.94) * mm, "end": v(-7.93, 5.36) * mm});
            skLineSegment(sketch, "E1541", {"start": v(-7.93, 5.36) * mm, "end": v(-8.06, 5.43) * mm});
            skLineSegment(sketch, "E1542", {"start": v(-8.06, 5.43) * mm, "end": v(-8.22, 5.47) * mm});
            skLineSegment(sketch, "E1543", {"start": v(-8.22, 5.47) * mm, "end": v(-8.38, 5.49) * mm});
            skLineSegment(sketch, "E1544", {"start": v(-8.38, 5.49) * mm, "end": v(-8.53, 5.46) * mm});
            skLineSegment(sketch, "E1545", {"start": v(-8.53, 5.46) * mm, "end": v(-8.63, 5.39) * mm});
            skLineSegment(sketch, "E1546", {"start": v(-8.63, 5.39) * mm, "end": v(-8.71, 5.26) * mm});
            skLineSegment(sketch, "E1547", {"start": v(-8.71, 5.26) * mm, "end": v(-8.78, 5.12) * mm});
            skLineSegment(sketch, "E1548", {"start": v(-8.78, 5.12) * mm, "end": v(-8.8, 4.98) * mm});
            skLineSegment(sketch, "E1549", {"start": v(-8.8, 4.98) * mm, "end": v(-8.74, 4.18) * mm});
            skLineSegment(sketch, "E1550", {"start": v(-8.74, 4.18) * mm, "end": v(-8.68, 3.37) * mm});
            skLineSegment(sketch, "E1551", {"start": v(-8.68, 3.37) * mm, "end": v(-8.62, 2.57) * mm});
            skLineSegment(sketch, "E1552", {"start": v(-8.62, 2.57) * mm, "end": v(-8.57, 1.77) * mm});
            skLineSegment(sketch, "E1553", {"start": v(-8.57, 1.77) * mm, "end": v(-8.54, 0.9) * mm});
            skLineSegment(sketch, "E1554", {"start": v(-8.54, 0.9) * mm, "end": v(-8.52, 0.04) * mm});
            skLineSegment(sketch, "E1555", {"start": v(-8.52, 0.04) * mm, "end": v(-8.5, -0.82) * mm});
            skLineSegment(sketch, "E1556", {"start": v(-8.5, -0.82) * mm, "end": v(-8.5, -1.69) * mm});
            skLineSegment(sketch, "E1557", {"start": v(-8.5, -1.69) * mm, "end": v(-8.5, -1.73) * mm});
            skLineSegment(sketch, "E1558", {"start": v(-8.5, -1.73) * mm, "end": v(-8.5, -1.78) * mm});
            skLineSegment(sketch, "E1559", {"start": v(-8.5, -1.78) * mm, "end": v(-8.52, -1.82) * mm});
            skLineSegment(sketch, "E1560", {"start": v(-8.52, -1.82) * mm, "end": v(-8.52, -1.86) * mm});
            skLineSegment(sketch, "E1561", {"start": v(-8.52, -1.86) * mm, "end": v(-8.51, -2.64) * mm});
            skLineSegment(sketch, "E1562", {"start": v(-8.51, -2.64) * mm, "end": v(-8.5, -3.41) * mm});
            skLineSegment(sketch, "E1563", {"start": v(-8.5, -3.41) * mm, "end": v(-8.49, -4.18) * mm});
            skLineSegment(sketch, "E1564", {"start": v(-8.49, -4.18) * mm, "end": v(-8.44, -4.95) * mm});
            skLineSegment(sketch, "E1565", {"start": v(-8.44, -4.95) * mm, "end": v(-8.41, -5.49) * mm});
            skLineSegment(sketch, "E1566", {"start": v(-8.41, -5.49) * mm, "end": v(-8.45, -6) * mm});
            skLineSegment(sketch, "E1567", {"start": v(-8.45, -6) * mm, "end": v(-8.59, -6.48) * mm});
            skLineSegment(sketch, "E1568", {"start": v(-8.59, -6.48) * mm, "end": v(-8.85, -6.94) * mm});
            skLineSegment(sketch, "E1569", {"start": v(-8.85, -6.94) * mm, "end": v(-9.17, -7.36) * mm});
            skLineSegment(sketch, "E1570", {"start": v(-9.17, -7.36) * mm, "end": v(-9.49, -7.78) * mm});
            skLineSegment(sketch, "E1571", {"start": v(-9.49, -7.78) * mm, "end": v(-9.8, -8.2) * mm});
            skLineSegment(sketch, "E1572", {"start": v(-9.8, -8.2) * mm, "end": v(-10.1, -8.63) * mm});
            skLineSegment(sketch, "E1573", {"start": v(-10.1, -8.63) * mm, "end": v(-10.37, -9.19) * mm});
            skLineSegment(sketch, "E1574", {"start": v(-10.37, -9.19) * mm, "end": v(-10.41, -9.8) * mm});
            skLineSegment(sketch, "E1575", {"start": v(-10.41, -9.8) * mm, "end": v(-10.25, -10.45) * mm});
            skLineSegment(sketch, "E1576", {"start": v(-10.25, -10.45) * mm, "end": v(-9.88, -11.07) * mm});
            skLineSegment(sketch, "E1577", {"start": v(-9.88, -11.07) * mm, "end": v(-9.51, -11.45) * mm});
            skLineSegment(sketch, "E1578", {"start": v(-9.51, -11.45) * mm, "end": v(-9.1, -11.64) * mm});
            skLineSegment(sketch, "E1579", {"start": v(-9.1, -11.64) * mm, "end": v(-8.62, -11.66) * mm});
            skLineSegment(sketch, "E1580", {"start": v(-8.62, -11.66) * mm, "end": v(-8.01, -11.5) * mm});
            skLineSegment(sketch, "E1581", {"start": v(-8.01, -11.5) * mm, "end": v(-7.65, -11.42) * mm});
            skLineSegment(sketch, "E1582", {"start": v(-7.65, -11.42) * mm, "end": v(-7.3, -11.42) * mm});
            skLineSegment(sketch, "E1583", {"start": v(-7.3, -11.42) * mm, "end": v(-6.97, -11.5) * mm});
            skLineSegment(sketch, "E1584", {"start": v(-6.97, -11.5) * mm, "end": v(-6.65, -11.67) * mm});
            skLineSegment(sketch, "E1585", {"start": v(-6.65, -11.67) * mm, "end": v(-5.95, -11.94) * mm});
            skLineSegment(sketch, "E1586", {"start": v(-5.95, -11.94) * mm, "end": v(-5.35, -11.88) * mm});
            skLineSegment(sketch, "E1587", {"start": v(-5.35, -11.88) * mm, "end": v(-4.86, -11.51) * mm});
            skLineSegment(sketch, "E1588", {"start": v(-4.86, -11.51) * mm, "end": v(-4.52, -10.84) * mm});
            skLineSegment(sketch, "E1589", {"start": v(-4.52, -10.84) * mm, "end": v(-4.34, -10.4) * mm});
            skLineSegment(sketch, "E1590", {"start": v(-4.34, -10.4) * mm, "end": v(-4.1, -10.13) * mm});
            skLineSegment(sketch, "E1591", {"start": v(-4.1, -10.13) * mm, "end": v(-3.78, -10) * mm});
            skLineSegment(sketch, "E1592", {"start": v(-3.78, -10) * mm, "end": v(-3.3, -9.94) * mm});
            skLineSegment(sketch, "E1593", {"start": v(-3.3, -9.94) * mm, "end": v(-2.8, -9.92) * mm});
            skLineSegment(sketch, "E1594", {"start": v(-2.8, -9.92) * mm, "end": v(-2.29, -9.9) * mm});
            skLineSegment(sketch, "E1595", {"start": v(-2.29, -9.9) * mm, "end": v(-1.78, -9.86) * mm});
            skLineSegment(sketch, "E1596", {"start": v(-1.78, -9.86) * mm, "end": v(-1.28, -9.8) * mm});
            skLineSegment(sketch, "E1597", {"start": v(-1.28, -9.8) * mm, "end": v(-0.76, -9.59) * mm});
            skLineSegment(sketch, "E1598", {"start": v(-0.76, -9.59) * mm, "end": v(-0.5, -9.22) * mm});
            skLineSegment(sketch, "E1599", {"start": v(-0.5, -9.22) * mm, "end": v(-0.5, -8.76) * mm});
            skLineSegment(sketch, "E1600", {"start": v(-0.5, -8.76) * mm, "end": v(-0.78, -8.26) * mm});
            skLineSegment(sketch, "E1601", {"start": v(-0.78, -8.26) * mm, "end": v(-1.4, -7.66) * mm});
            skLineSegment(sketch, "E1602", {"start": v(-1.4, -7.66) * mm, "end": v(-2.07, -7.16) * mm});
            skLineSegment(sketch, "E1603", {"start": v(-2.07, -7.16) * mm, "end": v(-2.8, -6.74) * mm});
            skLineSegment(sketch, "E1604", {"start": v(-2.8, -6.74) * mm, "end": v(-3.6, -6.39) * mm});
            skLineSegment(sketch, "E1605", {"start": v(-3.6, -6.39) * mm, "end": v(-4.14, -6.1) * mm});
            skLineSegment(sketch, "E1606", {"start": v(-4.14, -6.1) * mm, "end": v(-4.48, -5.72) * mm});
            skLineSegment(sketch, "E1607", {"start": v(-4.48, -5.72) * mm, "end": v(-4.65, -5.24) * mm});
            skLineSegment(sketch, "E1608", {"start": v(-4.65, -5.24) * mm, "end": v(-4.7, -4.62) * mm});
            skLineSegment(sketch, "E1609", {"start": v(-4.7, -4.62) * mm, "end": v(-4.68, -2.38) * mm});
            skLineSegment(sketch, "E1610", {"start": v(-4.68, -2.38) * mm, "end": v(-4.66, -0.13) * mm});
            skLineSegment(sketch, "E1611", {"start": v(-4.66, -0.13) * mm, "end": v(-4.66, 2.12) * mm});
            skLineSegment(sketch, "E1612", {"start": v(-4.66, 2.12) * mm, "end": v(-4.66, 4.37) * mm});
            skLineSegment(sketch, "E1613", {"start": v(-4.66, 4.37) * mm, "end": v(-4.68, 4.58) * mm});
            skLineSegment(sketch, "E1614", {"start": v(-4.68, 4.58) * mm, "end": v(-4.73, 4.8) * mm});
            skLineSegment(sketch, "E1615", {"start": v(-4.73, 4.8) * mm, "end": v(-4.8, 5) * mm});
            skLineSegment(sketch, "E1616", {"start": v(-4.8, 5) * mm, "end": v(-4.9, 5.2) * mm});
            skLineSegment(sketch, "E1617", {"start": v(-4.9, 5.2) * mm, "end": v(-5.05, 5.45) * mm});
            skLineSegment(sketch, "E1618", {"start": v(-5.05, 5.45) * mm, "end": v(-5.25, 5.63) * mm});
            skLineSegment(sketch, "E1619", {"start": v(-5.25, 5.63) * mm, "end": v(-5.49, 5.71) * mm});
            skLineSegment(sketch, "E1620", {"start": v(-5.49, 5.71) * mm, "end": v(-5.76, 5.64) * mm});
            skLineSegment(sketch, "E1621", {"start": v(-5.76, 5.64) * mm, "end": v(-5.96, 5.48) * mm});
            skLineSegment(sketch, "E1622", {"start": v(-5.96, 5.48) * mm, "end": v(-6.14, 5.26) * mm});
            skLineSegment(sketch, "E1623", {"start": v(-6.14, 5.26) * mm, "end": v(-6.26, 5.03) * mm});
            skLineSegment(sketch, "E1624", {"start": v(-6.26, 5.03) * mm, "end": v(-6.29, 4.82) * mm});
            skLineSegment(sketch, "E1625", {"start": v(-6.29, 4.82) * mm, "end": v(-6.16, 3.61) * mm});
            skLineSegment(sketch, "E1626", {"start": v(-6.16, 3.61) * mm, "end": v(-6.18, 2.39) * mm});
            skLineSegment(sketch, "E1627", {"start": v(-6.18, 2.39) * mm, "end": v(-6.17, 1.17) * mm});
            skLineSegment(sketch, "E1628", {"start": v(-6.17, 1.17) * mm, "end": v(-5.9, -0.03) * mm});
            skLineSegment(sketch, "E1629", {"start": v(-5.9, -0.03) * mm, "end": v(-5.89, -0.13) * mm});
            skLineSegment(sketch, "E1630", {"start": v(-5.89, -0.13) * mm, "end": v(-5.89, -0.24) * mm});
            skLineSegment(sketch, "E1631", {"start": v(-5.89, -0.24) * mm, "end": v(-5.9, -0.34) * mm});
            skLineSegment(sketch, "E1632", {"start": v(-5.9, -0.34) * mm, "end": v(-5.9, -0.45) * mm});
            skLineSegment(sketch, "E1633", {"start": v(-5.9, -0.45) * mm, "end": v(-5.96, -1.57) * mm});
            skLineSegment(sketch, "E1634", {"start": v(-5.96, -1.57) * mm, "end": v(-6.02, -2.7) * mm});
            skLineSegment(sketch, "E1635", {"start": v(-6.02, -2.7) * mm, "end": v(-6.07, -3.82) * mm});
            skLineSegment(sketch, "E1636", {"start": v(-6.07, -3.82) * mm, "end": v(-6.13, -4.94) * mm});
            skLineSegment(sketch, "E1637", {"start": v(-6.13, -4.94) * mm, "end": v(-6.11, -5.7) * mm});
            skLineSegment(sketch, "E1638", {"start": v(-6.11, -5.7) * mm, "end": v(-5.95, -6.19) * mm});
            skLineSegment(sketch, "E1639", {"start": v(-5.95, -6.19) * mm, "end": v(-5.57, -6.55) * mm});
            skLineSegment(sketch, "E1640", {"start": v(-5.57, -6.55) * mm, "end": v(-4.9, -6.9) * mm});
            skLineSegment(sketch, "E1641", {"start": v(-4.9, -6.9) * mm, "end": v(-4.4, -7.12) * mm});
            skLineSegment(sketch, "E1642", {"start": v(-4.4, -7.12) * mm, "end": v(-3.9, -7.34) * mm});
            skLineSegment(sketch, "E1643", {"start": v(-3.9, -7.34) * mm, "end": v(-3.42, -7.56) * mm});
            skLineSegment(sketch, "E1644", {"start": v(-3.42, -7.56) * mm, "end": v(-2.94, -7.8) * mm});
            skLineSegment(sketch, "E1645", {"start": v(-2.94, -7.8) * mm, "end": v(-2.8, -7.92) * mm});
            skLineSegment(sketch, "E1646", {"start": v(-2.8, -7.92) * mm, "end": v(-2.67, -8.1) * mm});
            skLineSegment(sketch, "E1647", {"start": v(-2.67, -8.1) * mm, "end": v(-2.59, -8.26) * mm});
            skLineSegment(sketch, "E1648", {"start": v(-2.59, -8.26) * mm, "end": v(-2.58, -8.39) * mm});
            skLineSegment(sketch, "E1649", {"start": v(-2.58, -8.39) * mm, "end": v(-2.69, -8.54) * mm});
            skLineSegment(sketch, "E1650", {"start": v(-2.69, -8.54) * mm, "end": v(-2.84, -8.68) * mm});
            skLineSegment(sketch, "E1651", {"start": v(-2.84, -8.68) * mm, "end": v(-3.02, -8.78) * mm});
            skLineSegment(sketch, "E1652", {"start": v(-3.02, -8.78) * mm, "end": v(-3.2, -8.85) * mm});
            skLineSegment(sketch, "E1653", {"start": v(-3.2, -8.85) * mm, "end": v(-3.36, -8.85) * mm});
            skLineSegment(sketch, "E1654", {"start": v(-3.36, -8.85) * mm, "end": v(-3.54, -8.81) * mm});
            skLineSegment(sketch, "E1655", {"start": v(-3.54, -8.81) * mm, "end": v(-3.7, -8.74) * mm});
            skLineSegment(sketch, "E1656", {"start": v(-3.7, -8.74) * mm, "end": v(-3.87, -8.67) * mm});
            skLineSegment(sketch, "E1657", {"start": v(-3.87, -8.67) * mm, "end": v(-4.17, -8.51) * mm});
            skLineSegment(sketch, "E1658", {"start": v(-4.17, -8.51) * mm, "end": v(-4.45, -8.35) * mm});
            skLineSegment(sketch, "E1659", {"start": v(-4.45, -8.35) * mm, "end": v(-4.75, -8.2) * mm});
            skLineSegment(sketch, "E1660", {"start": v(-4.75, -8.2) * mm, "end": v(-5.05, -8.08) * mm});
            skLineSegment(sketch, "E1661", {"start": v(-5.05, -8.08) * mm, "end": v(-5.22, -8.05) * mm});
            skLineSegment(sketch, "E1662", {"start": v(-5.22, -8.05) * mm, "end": v(-5.42, -8.07) * mm});
            skLineSegment(sketch, "E1663", {"start": v(-5.42, -8.07) * mm, "end": v(-5.6, -8.13) * mm});
            skLineSegment(sketch, "E1664", {"start": v(-5.6, -8.13) * mm, "end": v(-5.76, -8.22) * mm});
            skLineSegment(sketch, "E1665", {"start": v(-5.76, -8.22) * mm, "end": v(-5.81, -8.32) * mm});
            skLineSegment(sketch, "E1666", {"start": v(-5.81, -8.32) * mm, "end": v(-5.82, -8.49) * mm});
            skLineSegment(sketch, "E1667", {"start": v(-5.82, -8.49) * mm, "end": v(-5.8, -8.67) * mm});
            skLineSegment(sketch, "E1668", {"start": v(-5.8, -8.67) * mm, "end": v(-5.8, -8.85) * mm});
            skLineSegment(sketch, "E1669", {"start": v(-5.8, -8.85) * mm, "end": v(-5.78, -9.12) * mm});
            skLineSegment(sketch, "E1670", {"start": v(-5.78, -9.12) * mm, "end": v(-5.76, -9.39) * mm});
            skLineSegment(sketch, "E1671", {"start": v(-5.76, -9.39) * mm, "end": v(-5.74, -9.65) * mm});
            skLineSegment(sketch, "E1672", {"start": v(-5.74, -9.65) * mm, "end": v(-5.72, -9.91) * mm});
            skLineSegment(sketch, "E1673", {"start": v(-5.72, -9.91) * mm, "end": v(-6.29, -9.82) * mm});
            skLineSegment(sketch, "E1674", {"start": v(-6.29, -9.82) * mm, "end": v(-6.62, -9.49) * mm});
            skLineSegment(sketch, "E1675", {"start": v(-6.62, -9.49) * mm, "end": v(-6.9, -9.08) * mm});
            skLineSegment(sketch, "E1676", {"start": v(-6.9, -9.08) * mm, "end": v(-7.3, -8.74) * mm});
            skLineSegment(sketch, "E1677", {"start": v(-9.74, 14.27) * mm, "end": v(-8.44, 14.35) * mm});
            skLineSegment(sketch, "E1678", {"start": v(-8.44, 14.35) * mm, "end": v(-7.34, 14.56) * mm});
            skLineSegment(sketch, "E1679", {"start": v(-7.34, 14.56) * mm, "end": v(-6.4, 14.91) * mm});
            skLineSegment(sketch, "E1680", {"start": v(-6.4, 14.91) * mm, "end": v(-5.54, 15.4) * mm});
            skLineSegment(sketch, "E1681", {"start": v(-5.54, 15.4) * mm, "end": v(-4.33, 16.8) * mm});
            skLineSegment(sketch, "E1682", {"start": v(-4.33, 16.8) * mm, "end": v(-4.09, 18.37) * mm});
            skLineSegment(sketch, "E1683", {"start": v(-4.09, 18.37) * mm, "end": v(-4.61, 19.87) * mm});
            skLineSegment(sketch, "E1684", {"start": v(-4.61, 19.87) * mm, "end": v(-5.72, 21.04) * mm});
            skLineSegment(sketch, "E1685", {"start": v(-5.72, 21.04) * mm, "end": v(-6.56, 21.47) * mm});
            skLineSegment(sketch, "E1686", {"start": v(-6.56, 21.47) * mm, "end": v(-7.42, 21.65) * mm});
            skLineSegment(sketch, "E1687", {"start": v(-7.42, 21.65) * mm, "end": v(-8.32, 21.64) * mm});
            skLineSegment(sketch, "E1688", {"start": v(-8.32, 21.64) * mm, "end": v(-9.23, 21.48) * mm});
            skLineSegment(sketch, "E1689", {"start": v(-9.23, 21.48) * mm, "end": v(-10.4, 21.1) * mm});
            skLineSegment(sketch, "E1690", {"start": v(-10.4, 21.1) * mm, "end": v(-11.46, 20.55) * mm});
            skLineSegment(sketch, "E1691", {"start": v(-11.46, 20.55) * mm, "end": v(-12.37, 19.79) * mm});
            skLineSegment(sketch, "E1692", {"start": v(-12.37, 19.79) * mm, "end": v(-13.12, 18.8) * mm});
            skLineSegment(sketch, "E1693", {"start": v(-13.12, 18.8) * mm, "end": v(-13.3, 18.45) * mm});
            skLineSegment(sketch, "E1694", {"start": v(-13.3, 18.45) * mm, "end": v(-13.42, 18.07) * mm});
            skLineSegment(sketch, "E1695", {"start": v(-13.42, 18.07) * mm, "end": v(-13.5, 17.67) * mm});
            skLineSegment(sketch, "E1696", {"start": v(-13.5, 17.67) * mm, "end": v(-13.48, 17.3) * mm});
            skLineSegment(sketch, "E1697", {"start": v(-13.48, 17.3) * mm, "end": v(-12.96, 16.14) * mm});
            skLineSegment(sketch, "E1698", {"start": v(-12.96, 16.14) * mm, "end": v(-11.99, 15.1) * mm});
            skLineSegment(sketch, "E1699", {"start": v(-11.99, 15.1) * mm, "end": v(-10.83, 14.41) * mm});
            skLineSegment(sketch, "E1700", {"start": v(-10.83, 14.41) * mm, "end": v(-9.74, 14.27) * mm});
            skLineSegment(sketch, "E1701", {"start": v(7.17, -13.1) * mm, "end": v(7.34, -12.95) * mm});
            skLineSegment(sketch, "E1702", {"start": v(7.34, -12.95) * mm, "end": v(7.5, -12.82) * mm});
            skLineSegment(sketch, "E1703", {"start": v(7.5, -12.82) * mm, "end": v(7.66, -12.68) * mm});
            skLineSegment(sketch, "E1704", {"start": v(7.66, -12.68) * mm, "end": v(7.81, -12.55) * mm});
            skLineSegment(sketch, "E1705", {"start": v(7.81, -12.55) * mm, "end": v(7.3, -12.15) * mm});
            skLineSegment(sketch, "E1706", {"start": v(7.3, -12.15) * mm, "end": v(6.95, -12) * mm});
            skLineSegment(sketch, "E1707", {"start": v(6.95, -12) * mm, "end": v(6.67, -12.1) * mm});
            skLineSegment(sketch, "E1708", {"start": v(6.67, -12.1) * mm, "end": v(6.39, -12.43) * mm});
            skLineSegment(sketch, "E1709", {"start": v(6.39, -12.43) * mm, "end": v(6.58, -12.59) * mm});
            skLineSegment(sketch, "E1710", {"start": v(6.58, -12.59) * mm, "end": v(6.77, -12.75) * mm});
            skLineSegment(sketch, "E1711", {"start": v(6.77, -12.75) * mm, "end": v(6.97, -12.92) * mm});
            skLineSegment(sketch, "E1712", {"start": v(6.97, -12.92) * mm, "end": v(7.17, -13.1) * mm});
            skLineSegment(sketch, "E1713", {"start": v(8.34, -7.58) * mm, "end": v(8.57, -7.43) * mm});
            skLineSegment(sketch, "E1714", {"start": v(8.57, -7.43) * mm, "end": v(8.79, -7.3) * mm});
            skLineSegment(sketch, "E1715", {"start": v(8.79, -7.3) * mm, "end": v(9, -7.17) * mm});
            skLineSegment(sketch, "E1716", {"start": v(9, -7.17) * mm, "end": v(9.2, -7.05) * mm});
            skLineSegment(sketch, "E1717", {"start": v(9.2, -7.05) * mm, "end": v(8.95, -6.66) * mm});
            skLineSegment(sketch, "E1718", {"start": v(8.95, -6.66) * mm, "end": v(8.7, -6.54) * mm});
            skLineSegment(sketch, "E1719", {"start": v(8.7, -6.54) * mm, "end": v(8.36, -6.68) * mm});
            skLineSegment(sketch, "E1720", {"start": v(8.36, -6.68) * mm, "end": v(7.91, -7.08) * mm});
            skLineSegment(sketch, "E1721", {"start": v(7.91, -7.08) * mm, "end": v(8, -7.2) * mm});
            skLineSegment(sketch, "E1722", {"start": v(8, -7.2) * mm, "end": v(8.1, -7.3) * mm});
            skLineSegment(sketch, "E1723", {"start": v(8.1, -7.3) * mm, "end": v(8.22, -7.44) * mm});
            skLineSegment(sketch, "E1724", {"start": v(8.22, -7.44) * mm, "end": v(8.34, -7.58) * mm});
            skLineSegment(sketch, "E1725", {"start": v(9.21, -15.34) * mm, "end": v(8.85, -14.98) * mm});
            skLineSegment(sketch, "E1726", {"start": v(8.85, -14.98) * mm, "end": v(8.59, -14.87) * mm});
            skLineSegment(sketch, "E1727", {"start": v(8.59, -14.87) * mm, "end": v(8.32, -15) * mm});
            skLineSegment(sketch, "E1728", {"start": v(8.32, -15) * mm, "end": v(7.94, -15.41) * mm});
            skLineSegment(sketch, "E1729", {"start": v(7.94, -15.41) * mm, "end": v(8.24, -15.7) * mm});
            skLineSegment(sketch, "E1730", {"start": v(8.24, -15.7) * mm, "end": v(8.5, -15.8) * mm});
            skLineSegment(sketch, "E1731", {"start": v(8.5, -15.8) * mm, "end": v(8.78, -15.67) * mm});
            skLineSegment(sketch, "E1732", {"start": v(8.78, -15.67) * mm, "end": v(9.21, -15.34) * mm});
            skLineSegment(sketch, "E1733", {"start": v(2.45, -1.86) * mm, "end": v(2.45, -1.95) * mm});
            skLineSegment(sketch, "E1734", {"start": v(2.45, -1.95) * mm, "end": v(2.45, -2.04) * mm});
            skLineSegment(sketch, "E1735", {"start": v(2.45, -2.04) * mm, "end": v(2.44, -2.12) * mm});
            skLineSegment(sketch, "E1736", {"start": v(2.44, -2.12) * mm, "end": v(2.44, -2.21) * mm});
            skLineSegment(sketch, "E1737", {"start": v(2.44, -2.21) * mm, "end": v(2.67, -2.27) * mm});
            skLineSegment(sketch, "E1738", {"start": v(2.67, -2.27) * mm, "end": v(2.91, -2.33) * mm});
            skLineSegment(sketch, "E1739", {"start": v(2.91, -2.33) * mm, "end": v(3.15, -2.38) * mm});
            skLineSegment(sketch, "E1740", {"start": v(3.15, -2.38) * mm, "end": v(3.4, -2.4) * mm});
            skLineSegment(sketch, "E1741", {"start": v(3.4, -2.4) * mm, "end": v(3.5, -2.38) * mm});
            skLineSegment(sketch, "E1742", {"start": v(3.5, -2.38) * mm, "end": v(3.59, -2.31) * mm});
            skLineSegment(sketch, "E1743", {"start": v(3.59, -2.31) * mm, "end": v(3.7, -2.23) * mm});
            skLineSegment(sketch, "E1744", {"start": v(3.7, -2.23) * mm, "end": v(3.8, -2.15) * mm});
            skLineSegment(sketch, "E1745", {"start": v(3.8, -2.15) * mm, "end": v(3.7, -2.04) * mm});
            skLineSegment(sketch, "E1746", {"start": v(3.7, -2.04) * mm, "end": v(3.62, -1.93) * mm});
            skLineSegment(sketch, "E1747", {"start": v(3.62, -1.93) * mm, "end": v(3.54, -1.83) * mm});
            skLineSegment(sketch, "E1748", {"start": v(3.54, -1.83) * mm, "end": v(3.45, -1.8) * mm});
            skLineSegment(sketch, "E1749", {"start": v(3.45, -1.8) * mm, "end": v(3.2, -1.79) * mm});
            skLineSegment(sketch, "E1750", {"start": v(3.2, -1.79) * mm, "end": v(2.95, -1.8) * mm});
            skLineSegment(sketch, "E1751", {"start": v(2.95, -1.8) * mm, "end": v(2.7, -1.83) * mm});
            skLineSegment(sketch, "E1752", {"start": v(2.7, -1.83) * mm, "end": v(2.45, -1.86) * mm});
            skLineSegment(sketch, "E1753", {"start": v(8.56, -10.13) * mm, "end": v(8.25, -9.86) * mm});
            skLineSegment(sketch, "E1754", {"start": v(8.25, -9.86) * mm, "end": v(8.05, -9.75) * mm});
            skLineSegment(sketch, "E1755", {"start": v(8.05, -9.75) * mm, "end": v(7.87, -9.83) * mm});
            skLineSegment(sketch, "E1756", {"start": v(7.87, -9.83) * mm, "end": v(7.61, -10.06) * mm});
            skLineSegment(sketch, "E1757", {"start": v(7.61, -10.06) * mm, "end": v(7.75, -10.17) * mm});
            skLineSegment(sketch, "E1758", {"start": v(7.75, -10.17) * mm, "end": v(7.88, -10.29) * mm});
            skLineSegment(sketch, "E1759", {"start": v(7.88, -10.29) * mm, "end": v(8.03, -10.4) * mm});
            skLineSegment(sketch, "E1760", {"start": v(8.03, -10.4) * mm, "end": v(8.18, -10.54) * mm});
            skLineSegment(sketch, "E1761", {"start": v(8.18, -10.54) * mm, "end": v(8.28, -10.43) * mm});
            skLineSegment(sketch, "E1762", {"start": v(8.28, -10.43) * mm, "end": v(8.38, -10.33) * mm});
            skLineSegment(sketch, "E1763", {"start": v(8.38, -10.33) * mm, "end": v(8.47, -10.24) * mm});
            skLineSegment(sketch, "E1764", {"start": v(8.47, -10.24) * mm, "end": v(8.56, -10.13) * mm});
            skLineSegment(sketch, "E1765", {"start": v(22.23, -3.5) * mm, "end": v(21.9, -3.33) * mm});
            skLineSegment(sketch, "E1766", {"start": v(21.9, -3.33) * mm, "end": v(21.6, -3.18) * mm});
            skLineSegment(sketch, "E1767", {"start": v(21.6, -3.18) * mm, "end": v(21.32, -3.05) * mm});
            skLineSegment(sketch, "E1768", {"start": v(21.32, -3.05) * mm, "end": v(21.06, -2.93) * mm});
            skLineSegment(sketch, "E1769", {"start": v(21.06, -2.93) * mm, "end": v(20.89, -2.83) * mm});
            skLineSegment(sketch, "E1770", {"start": v(20.89, -2.83) * mm, "end": v(20.7, -2.73) * mm});
            skLineSegment(sketch, "E1771", {"start": v(20.7, -2.73) * mm, "end": v(20.53, -2.66) * mm});
            skLineSegment(sketch, "E1772", {"start": v(20.53, -2.66) * mm, "end": v(20.37, -2.63) * mm});
            skLineSegment(sketch, "E1773", {"start": v(20.37, -2.63) * mm, "end": v(20.17, -2.68) * mm});
            skLineSegment(sketch, "E1774", {"start": v(20.17, -2.68) * mm, "end": v(19.97, -2.77) * mm});
            skLineSegment(sketch, "E1775", {"start": v(19.97, -2.77) * mm, "end": v(19.8, -2.9) * mm});
            skLineSegment(sketch, "E1776", {"start": v(19.8, -2.9) * mm, "end": v(19.68, -3.05) * mm});
            skLineSegment(sketch, "E1777", {"start": v(19.68, -3.05) * mm, "end": v(19.66, -3.21) * mm});
            skLineSegment(sketch, "E1778", {"start": v(19.66, -3.21) * mm, "end": v(19.71, -3.42) * mm});
            skLineSegment(sketch, "E1779", {"start": v(19.71, -3.42) * mm, "end": v(19.8, -3.62) * mm});
            skLineSegment(sketch, "E1780", {"start": v(19.8, -3.62) * mm, "end": v(19.92, -3.73) * mm});
            skLineSegment(sketch, "E1781", {"start": v(19.92, -3.73) * mm, "end": v(20.59, -4.02) * mm});
            skLineSegment(sketch, "E1782", {"start": v(20.59, -4.02) * mm, "end": v(21.26, -4.3) * mm});
            skLineSegment(sketch, "E1783", {"start": v(21.26, -4.3) * mm, "end": v(21.94, -4.55) * mm});
            skLineSegment(sketch, "E1784", {"start": v(21.94, -4.55) * mm, "end": v(22.63, -4.79) * mm});
            skLineSegment(sketch, "E1785", {"start": v(22.63, -4.79) * mm, "end": v(22.88, -4.85) * mm});
            skLineSegment(sketch, "E1786", {"start": v(22.88, -4.85) * mm, "end": v(23.15, -4.88) * mm});
            skLineSegment(sketch, "E1787", {"start": v(23.15, -4.88) * mm, "end": v(23.42, -4.91) * mm});
            skLineSegment(sketch, "E1788", {"start": v(23.42, -4.91) * mm, "end": v(23.69, -4.96) * mm});
            skLineSegment(sketch, "E1789", {"start": v(23.69, -4.96) * mm, "end": v(24.01, -5.1) * mm});
            skLineSegment(sketch, "E1790", {"start": v(24.01, -5.1) * mm, "end": v(24.27, -5.3) * mm});
            skLineSegment(sketch, "E1791", {"start": v(24.27, -5.3) * mm, "end": v(24.45, -5.57) * mm});
            skLineSegment(sketch, "E1792", {"start": v(24.45, -5.57) * mm, "end": v(24.52, -5.93) * mm});
            skLineSegment(sketch, "E1793", {"start": v(24.52, -5.93) * mm, "end": v(24.5, -6.2) * mm});
            skLineSegment(sketch, "E1794", {"start": v(24.5, -6.2) * mm, "end": v(24.4, -6.4) * mm});
            skLineSegment(sketch, "E1795", {"start": v(24.4, -6.4) * mm, "end": v(24.2, -6.54) * mm});
            skLineSegment(sketch, "E1796", {"start": v(24.2, -6.54) * mm, "end": v(23.93, -6.59) * mm});
            skLineSegment(sketch, "E1797", {"start": v(23.93, -6.59) * mm, "end": v(23.5, -6.61) * mm});
            skLineSegment(sketch, "E1798", {"start": v(23.5, -6.61) * mm, "end": v(23.27, -6.7) * mm});
            skLineSegment(sketch, "E1799", {"start": v(23.27, -6.7) * mm, "end": v(23.2, -6.94) * mm});
            skLineSegment(sketch, "E1800", {"start": v(23.2, -6.94) * mm, "end": v(23.22, -7.4) * mm});
            skLineSegment(sketch, "E1801", {"start": v(23.22, -7.4) * mm, "end": v(22.48, -7.5) * mm});
            skLineSegment(sketch, "E1802", {"start": v(22.48, -7.5) * mm, "end": v(21.75, -7.49) * mm});
            skLineSegment(sketch, "E1803", {"start": v(21.75, -7.49) * mm, "end": v(21.04, -7.37) * mm});
            skLineSegment(sketch, "E1804", {"start": v(21.04, -7.37) * mm, "end": v(20.35, -7.13) * mm});
            skLineSegment(sketch, "E1805", {"start": v(20.35, -7.13) * mm, "end": v(20.06, -6.96) * mm});
            skLineSegment(sketch, "E1806", {"start": v(20.06, -6.96) * mm, "end": v(19.78, -6.75) * mm});
            skLineSegment(sketch, "E1807", {"start": v(19.78, -6.75) * mm, "end": v(19.54, -6.5) * mm});
            skLineSegment(sketch, "E1808", {"start": v(19.54, -6.5) * mm, "end": v(19.38, -6.24) * mm});
            skLineSegment(sketch, "E1809", {"start": v(19.38, -6.24) * mm, "end": v(18.52, -4.76) * mm});
            skLineSegment(sketch, "E1810", {"start": v(18.52, -4.76) * mm, "end": v(17.41, -3.58) * mm});
            skLineSegment(sketch, "E1811", {"start": v(17.41, -3.58) * mm, "end": v(16.06, -2.69) * mm});
            skLineSegment(sketch, "E1812", {"start": v(16.06, -2.69) * mm, "end": v(14.5, -2.06) * mm});
            skLineSegment(sketch, "E1813", {"start": v(14.5, -2.06) * mm, "end": v(14.02, -1.92) * mm});
            skLineSegment(sketch, "E1814", {"start": v(14.02, -1.92) * mm, "end": v(13.54, -1.8) * mm});
            skLineSegment(sketch, "E1815", {"start": v(13.54, -1.8) * mm, "end": v(13.06, -1.68) * mm});
            skLineSegment(sketch, "E1816", {"start": v(13.06, -1.68) * mm, "end": v(12.58, -1.55) * mm});
            skLineSegment(sketch, "E1817", {"start": v(12.58, -1.55) * mm, "end": v(12.06, -1.33) * mm});
            skLineSegment(sketch, "E1818", {"start": v(12.06, -1.33) * mm, "end": v(11.8, -1.02) * mm});
            skLineSegment(sketch, "E1819", {"start": v(11.8, -1.02) * mm, "end": v(11.82, -0.64) * mm});
            skLineSegment(sketch, "E1820", {"start": v(11.82, -0.64) * mm, "end": v(12.1, -0.16) * mm});
            skLineSegment(sketch, "E1821", {"start": v(12.1, -0.16) * mm, "end": v(13.4, 1.56) * mm});
            skLineSegment(sketch, "E1822", {"start": v(13.4, 1.56) * mm, "end": v(14.51, 3.38) * mm});
            skLineSegment(sketch, "E1823", {"start": v(14.51, 3.38) * mm, "end": v(15.48, 5.28) * mm});
            skLineSegment(sketch, "E1824", {"start": v(15.48, 5.28) * mm, "end": v(16.38, 7.23) * mm});
            skLineSegment(sketch, "E1825", {"start": v(16.38, 7.23) * mm, "end": v(16.66, 7.92) * mm});
            skLineSegment(sketch, "E1826", {"start": v(16.66, 7.92) * mm, "end": v(16.91, 8.62) * mm});
            skLineSegment(sketch, "E1827", {"start": v(16.91, 8.62) * mm, "end": v(17.15, 9.33) * mm});
            skLineSegment(sketch, "E1828", {"start": v(17.15, 9.33) * mm, "end": v(17.4, 10.04) * mm});
            skLineSegment(sketch, "E1829", {"start": v(17.4, 10.04) * mm, "end": v(17.81, 10.83) * mm});
            skLineSegment(sketch, "E1830", {"start": v(17.81, 10.83) * mm, "end": v(18.37, 11.23) * mm});
            skLineSegment(sketch, "E1831", {"start": v(18.37, 11.23) * mm, "end": v(19.06, 11.25) * mm});
            skLineSegment(sketch, "E1832", {"start": v(19.06, 11.25) * mm, "end": v(19.86, 10.88) * mm});
            skLineSegment(sketch, "E1833", {"start": v(19.86, 10.88) * mm, "end": v(20.7, 10.13) * mm});
            skLineSegment(sketch, "E1834", {"start": v(20.7, 10.13) * mm, "end": v(21.24, 9.2) * mm});
            skLineSegment(sketch, "E1835", {"start": v(21.24, 9.2) * mm, "end": v(21.48, 8.16) * mm});
            skLineSegment(sketch, "E1836", {"start": v(21.48, 8.16) * mm, "end": v(21.4, 7.04) * mm});
            skLineSegment(sketch, "E1837", {"start": v(21.4, 7.04) * mm, "end": v(21.26, 6.44) * mm});
            skLineSegment(sketch, "E1838", {"start": v(21.26, 6.44) * mm, "end": v(21.13, 5.84) * mm});
            skLineSegment(sketch, "E1839", {"start": v(21.13, 5.84) * mm, "end": v(21, 5.24) * mm});
            skLineSegment(sketch, "E1840", {"start": v(21, 5.24) * mm, "end": v(20.88, 4.64) * mm});
            skLineSegment(sketch, "E1841", {"start": v(20.88, 4.64) * mm, "end": v(20.57, 3.58) * mm});
            skLineSegment(sketch, "E1842", {"start": v(20.57, 3.58) * mm, "end": v(20.12, 2.6) * mm});
            skLineSegment(sketch, "E1843", {"start": v(20.12, 2.6) * mm, "end": v(19.51, 1.71) * mm});
            skLineSegment(sketch, "E1844", {"start": v(19.51, 1.71) * mm, "end": v(18.73, 0.92) * mm});
            skLineSegment(sketch, "E1845", {"start": v(18.73, 0.92) * mm, "end": v(18.5, 0.73) * mm});
            skLineSegment(sketch, "E1846", {"start": v(18.5, 0.73) * mm, "end": v(18.29, 0.52) * mm});
            skLineSegment(sketch, "E1847", {"start": v(18.29, 0.52) * mm, "end": v(18.07, 0.31) * mm});
            skLineSegment(sketch, "E1848", {"start": v(18.07, 0.31) * mm, "end": v(17.86, 0.1) * mm});
            skLineSegment(sketch, "E1849", {"start": v(17.86, 0.1) * mm, "end": v(17.56, -0.15) * mm});
            skLineSegment(sketch, "E1850", {"start": v(17.56, -0.15) * mm, "end": v(17.3, -0.43) * mm});
            skLineSegment(sketch, "E1851", {"start": v(17.3, -0.43) * mm, "end": v(17.14, -0.76) * mm});
            skLineSegment(sketch, "E1852", {"start": v(17.14, -0.76) * mm, "end": v(17.18, -1.18) * mm});
            skLineSegment(sketch, "E1853", {"start": v(17.18, -1.18) * mm, "end": v(17.41, -1.54) * mm});
            skLineSegment(sketch, "E1854", {"start": v(17.41, -1.54) * mm, "end": v(17.74, -1.76) * mm});
            skLineSegment(sketch, "E1855", {"start": v(17.74, -1.76) * mm, "end": v(18.13, -1.87) * mm});
            skLineSegment(sketch, "E1856", {"start": v(18.13, -1.87) * mm, "end": v(18.53, -1.89) * mm});
            skLineSegment(sketch, "E1857", {"start": v(18.53, -1.89) * mm, "end": v(18.96, -1.84) * mm});
            skLineSegment(sketch, "E1858", {"start": v(18.96, -1.84) * mm, "end": v(19.39, -1.75) * mm});
            skLineSegment(sketch, "E1859", {"start": v(19.39, -1.75) * mm, "end": v(19.81, -1.63) * mm});
            skLineSegment(sketch, "E1860", {"start": v(19.81, -1.63) * mm, "end": v(20.24, -1.5) * mm});
            skLineSegment(sketch, "E1861", {"start": v(20.24, -1.5) * mm, "end": v(20.44, -1.42) * mm});
            skLineSegment(sketch, "E1862", {"start": v(20.44, -1.42) * mm, "end": v(20.64, -1.31) * mm});
            skLineSegment(sketch, "E1863", {"start": v(20.64, -1.31) * mm, "end": v(20.84, -1.2) * mm});
            skLineSegment(sketch, "E1864", {"start": v(20.84, -1.2) * mm, "end": v(21.05, -1.12) * mm});
            skLineSegment(sketch, "E1865", {"start": v(21.05, -1.12) * mm, "end": v(21.71, -1.02) * mm});
            skLineSegment(sketch, "E1866", {"start": v(21.71, -1.02) * mm, "end": v(22.14, -1.17) * mm});
            skLineSegment(sketch, "E1867", {"start": v(22.14, -1.17) * mm, "end": v(22.35, -1.57) * mm});
            skLineSegment(sketch, "E1868", {"start": v(22.35, -1.57) * mm, "end": v(22.35, -2.23) * mm});
            skLineSegment(sketch, "E1869", {"start": v(22.35, -2.23) * mm, "end": v(22.32, -2.5) * mm});
            skLineSegment(sketch, "E1870", {"start": v(22.32, -2.5) * mm, "end": v(22.3, -2.78) * mm});
            skLineSegment(sketch, "E1871", {"start": v(22.3, -2.78) * mm, "end": v(22.26, -3.1) * mm});
            skLineSegment(sketch, "E1872", {"start": v(22.26, -3.1) * mm, "end": v(22.23, -3.5) * mm});
            skLineSegment(sketch, "E1873", {"start": v(18.62, 1.9) * mm, "end": v(18.8, 2.14) * mm});
            skLineSegment(sketch, "E1874", {"start": v(18.8, 2.14) * mm, "end": v(18.98, 2.35) * mm});
            skLineSegment(sketch, "E1875", {"start": v(18.98, 2.35) * mm, "end": v(19.1, 2.54) * mm});
            skLineSegment(sketch, "E1876", {"start": v(19.1, 2.54) * mm, "end": v(19.18, 2.72) * mm});
            skLineSegment(sketch, "E1877", {"start": v(19.18, 2.72) * mm, "end": v(19.17, 2.96) * mm});
            skLineSegment(sketch, "E1878", {"start": v(19.17, 2.96) * mm, "end": v(19.07, 3.14) * mm});
            skLineSegment(sketch, "E1879", {"start": v(19.07, 3.14) * mm, "end": v(18.89, 3.25) * mm});
            skLineSegment(sketch, "E1880", {"start": v(18.89, 3.25) * mm, "end": v(18.66, 3.24) * mm});
            skLineSegment(sketch, "E1881", {"start": v(18.66, 3.24) * mm, "end": v(18.47, 3.14) * mm});
            skLineSegment(sketch, "E1882", {"start": v(18.47, 3.14) * mm, "end": v(18.3, 2.98) * mm});
            skLineSegment(sketch, "E1883", {"start": v(18.3, 2.98) * mm, "end": v(18.15, 2.8) * mm});
            skLineSegment(sketch, "E1884", {"start": v(18.15, 2.8) * mm, "end": v(18.03, 2.6) * mm});
            skLineSegment(sketch, "E1885", {"start": v(18.03, 2.6) * mm, "end": v(18.07, 2.5) * mm});
            skLineSegment(sketch, "E1886", {"start": v(18.07, 2.5) * mm, "end": v(18.2, 2.34) * mm});
            skLineSegment(sketch, "E1887", {"start": v(18.2, 2.34) * mm, "end": v(18.4, 2.14) * mm});
            skLineSegment(sketch, "E1888", {"start": v(18.4, 2.14) * mm, "end": v(18.62, 1.9) * mm});
            skLineSegment(sketch, "E1889", {"start": v(19.9, 4.43) * mm, "end": v(20.26, 4.78) * mm});
            skLineSegment(sketch, "E1890", {"start": v(20.26, 4.78) * mm, "end": v(20.39, 5.03) * mm});
            skLineSegment(sketch, "E1891", {"start": v(20.39, 5.03) * mm, "end": v(20.3, 5.26) * mm});
            skLineSegment(sketch, "E1892", {"start": v(20.3, 5.26) * mm, "end": v(19.98, 5.55) * mm});
            skLineSegment(sketch, "E1893", {"start": v(19.98, 5.55) * mm, "end": v(19.86, 5.37) * mm});
            skLineSegment(sketch, "E1894", {"start": v(19.86, 5.37) * mm, "end": v(19.73, 5.2) * mm});
            skLineSegment(sketch, "E1895", {"start": v(19.73, 5.2) * mm, "end": v(19.6, 5.02) * mm});
            skLineSegment(sketch, "E1896", {"start": v(19.6, 5.02) * mm, "end": v(19.47, 4.83) * mm});
            skLineSegment(sketch, "E1897", {"start": v(19.47, 4.83) * mm, "end": v(19.58, 4.72) * mm});
            skLineSegment(sketch, "E1898", {"start": v(19.58, 4.72) * mm, "end": v(19.69, 4.63) * mm});
            skLineSegment(sketch, "E1899", {"start": v(19.69, 4.63) * mm, "end": v(19.8, 4.53) * mm});
            skLineSegment(sketch, "E1900", {"start": v(19.8, 4.53) * mm, "end": v(19.9, 4.43) * mm});
            skLineSegment(sketch, "E1901", {"start": v(-14.26, -28.41) * mm, "end": v(-14.46, -28.33) * mm});
            skLineSegment(sketch, "E1902", {"start": v(-14.46, -28.33) * mm, "end": v(-14.62, -28.27) * mm});
            skLineSegment(sketch, "E1903", {"start": v(-14.62, -28.27) * mm, "end": v(-14.76, -28.2) * mm});
            skLineSegment(sketch, "E1904", {"start": v(-14.76, -28.2) * mm, "end": v(-14.86, -28.13) * mm});
            skLineSegment(sketch, "E1905", {"start": v(-14.86, -28.13) * mm, "end": v(-15.68, -27.39) * mm});
            skLineSegment(sketch, "E1906", {"start": v(-15.68, -27.39) * mm, "end": v(-16.49, -26.64) * mm});
            skLineSegment(sketch, "E1907", {"start": v(-16.49, -26.64) * mm, "end": v(-17.3, -25.88) * mm});
            skLineSegment(sketch, "E1908", {"start": v(-17.3, -25.88) * mm, "end": v(-18.1, -25.11) * mm});
            skLineSegment(sketch, "E1909", {"start": v(-18.1, -25.11) * mm, "end": v(-18.22, -24.95) * mm});
            skLineSegment(sketch, "E1910", {"start": v(-18.22, -24.95) * mm, "end": v(-18.32, -24.74) * mm});
            skLineSegment(sketch, "E1911", {"start": v(-18.32, -24.74) * mm, "end": v(-18.38, -24.53) * mm});
            skLineSegment(sketch, "E1912", {"start": v(-18.38, -24.53) * mm, "end": v(-18.41, -24.3) * mm});
            skLineSegment(sketch, "E1913", {"start": v(-18.41, -24.3) * mm, "end": v(-18.4, -24.15) * mm});
            skLineSegment(sketch, "E1914", {"start": v(-18.4, -24.15) * mm, "end": v(-18.34, -23.98) * mm});
            skLineSegment(sketch, "E1915", {"start": v(-18.34, -23.98) * mm, "end": v(-18.24, -23.83) * mm});
            skLineSegment(sketch, "E1916", {"start": v(-18.24, -23.83) * mm, "end": v(-18.12, -23.72) * mm});
            skLineSegment(sketch, "E1917", {"start": v(-18.12, -23.72) * mm, "end": v(-18, -23.7) * mm});
            skLineSegment(sketch, "E1918", {"start": v(-18, -23.7) * mm, "end": v(-17.85, -23.72) * mm});
            skLineSegment(sketch, "E1919", {"start": v(-17.85, -23.72) * mm, "end": v(-17.69, -23.78) * mm});
            skLineSegment(sketch, "E1920", {"start": v(-17.69, -23.78) * mm, "end": v(-17.55, -23.87) * mm});
            skLineSegment(sketch, "E1921", {"start": v(-17.55, -23.87) * mm, "end": v(-17.05, -24.3) * mm});
            skLineSegment(sketch, "E1922", {"start": v(-17.05, -24.3) * mm, "end": v(-16.55, -24.73) * mm});
            skLineSegment(sketch, "E1923", {"start": v(-16.55, -24.73) * mm, "end": v(-16.06, -25.17) * mm});
            skLineSegment(sketch, "E1924", {"start": v(-16.06, -25.17) * mm, "end": v(-15.57, -25.6) * mm});
            skLineSegment(sketch, "E1925", {"start": v(-15.57, -25.6) * mm, "end": v(-15.5, -25.67) * mm});
            skLineSegment(sketch, "E1926", {"start": v(-15.5, -25.67) * mm, "end": v(-15.44, -25.73) * mm});
            skLineSegment(sketch, "E1927", {"start": v(-15.44, -25.73) * mm, "end": v(-15.37, -25.79) * mm});
            skLineSegment(sketch, "E1928", {"start": v(-15.37, -25.79) * mm, "end": v(-15.3, -25.85) * mm});
            skLineSegment(sketch, "E1929", {"start": v(-15.3, -25.85) * mm, "end": v(-14.67, -26.25) * mm});
            skLineSegment(sketch, "E1930", {"start": v(-14.67, -26.25) * mm, "end": v(-14.1, -26.28) * mm});
            skLineSegment(sketch, "E1931", {"start": v(-14.1, -26.28) * mm, "end": v(-13.63, -25.96) * mm});
            skLineSegment(sketch, "E1932", {"start": v(-13.63, -25.96) * mm, "end": v(-13.3, -25.28) * mm});
            skLineSegment(sketch, "E1933", {"start": v(-13.3, -25.28) * mm, "end": v(-13.07, -24.52) * mm});
            skLineSegment(sketch, "E1934", {"start": v(-13.07, -24.52) * mm, "end": v(-12.84, -23.76) * mm});
            skLineSegment(sketch, "E1935", {"start": v(-12.84, -23.76) * mm, "end": v(-12.6, -23) * mm});
            skLineSegment(sketch, "E1936", {"start": v(-12.6, -23) * mm, "end": v(-12.35, -22.25) * mm});
            skLineSegment(sketch, "E1937", {"start": v(-12.35, -22.25) * mm, "end": v(-12.12, -21.64) * mm});
            skLineSegment(sketch, "E1938", {"start": v(-12.12, -21.64) * mm, "end": v(-11.88, -21.02) * mm});
            skLineSegment(sketch, "E1939", {"start": v(-11.88, -21.02) * mm, "end": v(-11.63, -20.42) * mm});
            skLineSegment(sketch, "E1940", {"start": v(-11.63, -20.42) * mm, "end": v(-11.38, -19.8) * mm});
            skLineSegment(sketch, "E1941", {"start": v(-11.38, -19.8) * mm, "end": v(-11.27, -19.57) * mm});
            skLineSegment(sketch, "E1942", {"start": v(-11.27, -19.57) * mm, "end": v(-11.12, -19.38) * mm});
            skLineSegment(sketch, "E1943", {"start": v(-11.12, -19.38) * mm, "end": v(-10.9, -19.3) * mm});
            skLineSegment(sketch, "E1944", {"start": v(-10.9, -19.3) * mm, "end": v(-10.62, -19.35) * mm});
            skLineSegment(sketch, "E1945", {"start": v(-10.62, -19.35) * mm, "end": v(-10.41, -19.5) * mm});
            skLineSegment(sketch, "E1946", {"start": v(-10.41, -19.5) * mm, "end": v(-10.33, -19.7) * mm});
            skLineSegment(sketch, "E1947", {"start": v(-10.33, -19.7) * mm, "end": v(-10.34, -19.93) * mm});
            skLineSegment(sketch, "E1948", {"start": v(-10.34, -19.93) * mm, "end": v(-10.41, -20.17) * mm});
            skLineSegment(sketch, "E1949", {"start": v(-10.41, -20.17) * mm, "end": v(-10.96, -21.76) * mm});
            skLineSegment(sketch, "E1950", {"start": v(-10.96, -21.76) * mm, "end": v(-11.5, -23.34) * mm});
            skLineSegment(sketch, "E1951", {"start": v(-11.5, -23.34) * mm, "end": v(-12.05, -24.92) * mm});
            skLineSegment(sketch, "E1952", {"start": v(-12.05, -24.92) * mm, "end": v(-12.6, -26.5) * mm});
            skLineSegment(sketch, "E1953", {"start": v(-12.6, -26.5) * mm, "end": v(-12.71, -26.8) * mm});
            skLineSegment(sketch, "E1954", {"start": v(-12.71, -26.8) * mm, "end": v(-12.84, -27.1) * mm});
            skLineSegment(sketch, "E1955", {"start": v(-12.84, -27.1) * mm, "end": v(-13, -27.37) * mm});
            skLineSegment(sketch, "E1956", {"start": v(-13, -27.37) * mm, "end": v(-13.18, -27.61) * mm});
            skLineSegment(sketch, "E1957", {"start": v(-13.18, -27.61) * mm, "end": v(-13.43, -27.85) * mm});
            skLineSegment(sketch, "E1958", {"start": v(-13.43, -27.85) * mm, "end": v(-13.7, -28.05) * mm});
            skLineSegment(sketch, "E1959", {"start": v(-13.7, -28.05) * mm, "end": v(-13.99, -28.23) * mm});
            skLineSegment(sketch, "E1960", {"start": v(-13.99, -28.23) * mm, "end": v(-14.26, -28.41) * mm});
            skLineSegment(sketch, "E1961", {"start": v(-23.08, 17.07) * mm, "end": v(-22.92, 17.15) * mm});
            skLineSegment(sketch, "E1962", {"start": v(-22.92, 17.15) * mm, "end": v(-22.77, 17.23) * mm});
            skLineSegment(sketch, "E1963", {"start": v(-22.77, 17.23) * mm, "end": v(-22.62, 17.3) * mm});
            skLineSegment(sketch, "E1964", {"start": v(-22.62, 17.3) * mm, "end": v(-22.48, 17.36) * mm});
            skLineSegment(sketch, "E1965", {"start": v(-22.48, 17.36) * mm, "end": v(-21.66, 17.77) * mm});
            skLineSegment(sketch, "E1966", {"start": v(-21.66, 17.77) * mm, "end": v(-21.04, 18.35) * mm});
            skLineSegment(sketch, "E1967", {"start": v(-21.04, 18.35) * mm, "end": v(-20.62, 19.08) * mm});
            skLineSegment(sketch, "E1968", {"start": v(-20.62, 19.08) * mm, "end": v(-20.4, 19.97) * mm});
            skLineSegment(sketch, "E1969", {"start": v(-20.4, 19.97) * mm, "end": v(-20.32, 20.26) * mm});
            skLineSegment(sketch, "E1970", {"start": v(-20.32, 20.26) * mm, "end": v(-20.18, 20.42) * mm});
            skLineSegment(sketch, "E1971", {"start": v(-20.18, 20.42) * mm, "end": v(-19.96, 20.45) * mm});
            skLineSegment(sketch, "E1972", {"start": v(-19.96, 20.45) * mm, "end": v(-19.67, 20.35) * mm});
            skLineSegment(sketch, "E1973", {"start": v(-19.67, 20.35) * mm, "end": v(-19, 19.84) * mm});
            skLineSegment(sketch, "E1974", {"start": v(-19, 19.84) * mm, "end": v(-18.68, 19.15) * mm});
            skLineSegment(sketch, "E1975", {"start": v(-18.68, 19.15) * mm, "end": v(-18.76, 18.42) * mm});
            skLineSegment(sketch, "E1976", {"start": v(-18.76, 18.42) * mm, "end": v(-19.27, 17.78) * mm});
            skLineSegment(sketch, "E1977", {"start": v(-19.27, 17.78) * mm, "end": v(-20.26, 17.12) * mm});
            skLineSegment(sketch, "E1978", {"start": v(-20.26, 17.12) * mm, "end": v(-21.18, 16.73) * mm});
            skLineSegment(sketch, "E1979", {"start": v(-21.18, 16.73) * mm, "end": v(-22.1, 16.7) * mm});
            skLineSegment(sketch, "E1980", {"start": v(-22.1, 16.7) * mm, "end": v(-23.08, 17.07) * mm});
            skLineSegment(sketch, "E1981", {"start": v(-7.3, -8.74) * mm, "end": v(-6.9, -9.08) * mm});
            skLineSegment(sketch, "E1982", {"start": v(-6.9, -9.08) * mm, "end": v(-6.62, -9.49) * mm});
            skLineSegment(sketch, "E1983", {"start": v(-6.62, -9.49) * mm, "end": v(-6.29, -9.82) * mm});
            skLineSegment(sketch, "E1984", {"start": v(-6.29, -9.82) * mm, "end": v(-5.72, -9.91) * mm});
            skLineSegment(sketch, "E1985", {"start": v(-5.72, -9.91) * mm, "end": v(-5.74, -9.65) * mm});
            skLineSegment(sketch, "E1986", {"start": v(-5.74, -9.65) * mm, "end": v(-5.76, -9.39) * mm});
            skLineSegment(sketch, "E1987", {"start": v(-5.76, -9.39) * mm, "end": v(-5.78, -9.12) * mm});
            skLineSegment(sketch, "E1988", {"start": v(-5.78, -9.12) * mm, "end": v(-5.8, -8.85) * mm});
            skLineSegment(sketch, "E1989", {"start": v(-5.8, -8.85) * mm, "end": v(-5.8, -8.67) * mm});
            skLineSegment(sketch, "E1990", {"start": v(-5.8, -8.67) * mm, "end": v(-5.82, -8.49) * mm});
            skLineSegment(sketch, "E1991", {"start": v(-5.82, -8.49) * mm, "end": v(-5.81, -8.32) * mm});
            skLineSegment(sketch, "E1992", {"start": v(-5.81, -8.32) * mm, "end": v(-5.76, -8.22) * mm});
            skLineSegment(sketch, "E1993", {"start": v(-5.76, -8.22) * mm, "end": v(-5.6, -8.13) * mm});
            skLineSegment(sketch, "E1994", {"start": v(-5.6, -8.13) * mm, "end": v(-5.42, -8.07) * mm});
            skLineSegment(sketch, "E1995", {"start": v(-5.42, -8.07) * mm, "end": v(-5.22, -8.05) * mm});
            skLineSegment(sketch, "E1996", {"start": v(-5.22, -8.05) * mm, "end": v(-5.05, -8.08) * mm});
            skLineSegment(sketch, "E1997", {"start": v(-5.05, -8.08) * mm, "end": v(-4.75, -8.2) * mm});
            skLineSegment(sketch, "E1998", {"start": v(-4.75, -8.2) * mm, "end": v(-4.45, -8.35) * mm});
            skLineSegment(sketch, "E1999", {"start": v(-4.45, -8.35) * mm, "end": v(-4.17, -8.51) * mm});
            skLineSegment(sketch, "E2000", {"start": v(-4.17, -8.51) * mm, "end": v(-3.87, -8.67) * mm});
            skLineSegment(sketch, "E2001", {"start": v(-3.87, -8.67) * mm, "end": v(-3.7, -8.74) * mm});
            skLineSegment(sketch, "E2002", {"start": v(-3.7, -8.74) * mm, "end": v(-3.54, -8.81) * mm});
            skLineSegment(sketch, "E2003", {"start": v(-3.54, -8.81) * mm, "end": v(-3.36, -8.85) * mm});
            skLineSegment(sketch, "E2004", {"start": v(-3.36, -8.85) * mm, "end": v(-3.2, -8.85) * mm});
            skLineSegment(sketch, "E2005", {"start": v(-3.2, -8.85) * mm, "end": v(-3.02, -8.78) * mm});
            skLineSegment(sketch, "E2006", {"start": v(-3.02, -8.78) * mm, "end": v(-2.84, -8.68) * mm});
            skLineSegment(sketch, "E2007", {"start": v(-2.84, -8.68) * mm, "end": v(-2.69, -8.54) * mm});
            skLineSegment(sketch, "E2008", {"start": v(-2.69, -8.54) * mm, "end": v(-2.58, -8.39) * mm});
            skLineSegment(sketch, "E2009", {"start": v(-2.58, -8.39) * mm, "end": v(-2.59, -8.26) * mm});
            skLineSegment(sketch, "E2010", {"start": v(-2.59, -8.26) * mm, "end": v(-2.67, -8.1) * mm});
            skLineSegment(sketch, "E2011", {"start": v(-2.67, -8.1) * mm, "end": v(-2.8, -7.92) * mm});
            skLineSegment(sketch, "E2012", {"start": v(-2.8, -7.92) * mm, "end": v(-2.94, -7.8) * mm});
            skLineSegment(sketch, "E2013", {"start": v(-2.94, -7.8) * mm, "end": v(-3.42, -7.56) * mm});
            skLineSegment(sketch, "E2014", {"start": v(-3.42, -7.56) * mm, "end": v(-3.9, -7.34) * mm});
            skLineSegment(sketch, "E2015", {"start": v(-3.9, -7.34) * mm, "end": v(-4.4, -7.12) * mm});
            skLineSegment(sketch, "E2016", {"start": v(-4.4, -7.12) * mm, "end": v(-4.9, -6.9) * mm});
            skLineSegment(sketch, "E2017", {"start": v(-4.9, -6.9) * mm, "end": v(-5.57, -6.55) * mm});
            skLineSegment(sketch, "E2018", {"start": v(-5.57, -6.55) * mm, "end": v(-5.95, -6.19) * mm});
            skLineSegment(sketch, "E2019", {"start": v(-5.95, -6.19) * mm, "end": v(-6.11, -5.7) * mm});
            skLineSegment(sketch, "E2020", {"start": v(-6.11, -5.7) * mm, "end": v(-6.13, -4.94) * mm});
            skLineSegment(sketch, "E2021", {"start": v(-6.13, -4.94) * mm, "end": v(-6.07, -3.82) * mm});
            skLineSegment(sketch, "E2022", {"start": v(-6.07, -3.82) * mm, "end": v(-6.02, -2.7) * mm});
            skLineSegment(sketch, "E2023", {"start": v(-6.02, -2.7) * mm, "end": v(-5.96, -1.57) * mm});
            skLineSegment(sketch, "E2024", {"start": v(-5.96, -1.57) * mm, "end": v(-5.9, -0.45) * mm});
            skLineSegment(sketch, "E2025", {"start": v(-5.9, -0.45) * mm, "end": v(-5.9, -0.34) * mm});
            skLineSegment(sketch, "E2026", {"start": v(-5.9, -0.34) * mm, "end": v(-5.89, -0.24) * mm});
            skLineSegment(sketch, "E2027", {"start": v(-5.89, -0.24) * mm, "end": v(-5.89, -0.13) * mm});
            skLineSegment(sketch, "E2028", {"start": v(-5.89, -0.13) * mm, "end": v(-5.9, -0.03) * mm});
            skLineSegment(sketch, "E2029", {"start": v(-5.9, -0.03) * mm, "end": v(-6.17, 1.17) * mm});
            skLineSegment(sketch, "E2030", {"start": v(-6.17, 1.17) * mm, "end": v(-6.18, 2.39) * mm});
            skLineSegment(sketch, "E2031", {"start": v(-6.18, 2.39) * mm, "end": v(-6.16, 3.61) * mm});
            skLineSegment(sketch, "E2032", {"start": v(-6.16, 3.61) * mm, "end": v(-6.29, 4.82) * mm});
            skLineSegment(sketch, "E2033", {"start": v(-6.29, 4.82) * mm, "end": v(-6.26, 5.03) * mm});
            skLineSegment(sketch, "E2034", {"start": v(-6.26, 5.03) * mm, "end": v(-6.14, 5.26) * mm});
            skLineSegment(sketch, "E2035", {"start": v(-6.14, 5.26) * mm, "end": v(-5.96, 5.48) * mm});
            skLineSegment(sketch, "E2036", {"start": v(-5.96, 5.48) * mm, "end": v(-5.76, 5.64) * mm});
            skLineSegment(sketch, "E2037", {"start": v(-5.76, 5.64) * mm, "end": v(-5.49, 5.71) * mm});
            skLineSegment(sketch, "E2038", {"start": v(-5.49, 5.71) * mm, "end": v(-5.25, 5.63) * mm});
            skLineSegment(sketch, "E2039", {"start": v(-5.25, 5.63) * mm, "end": v(-5.05, 5.45) * mm});
            skLineSegment(sketch, "E2040", {"start": v(-5.05, 5.45) * mm, "end": v(-4.9, 5.2) * mm});
            skLineSegment(sketch, "E2041", {"start": v(-4.9, 5.2) * mm, "end": v(-4.8, 5) * mm});
            skLineSegment(sketch, "E2042", {"start": v(-4.8, 5) * mm, "end": v(-4.73, 4.8) * mm});
            skLineSegment(sketch, "E2043", {"start": v(-4.73, 4.8) * mm, "end": v(-4.68, 4.58) * mm});
            skLineSegment(sketch, "E2044", {"start": v(-4.68, 4.58) * mm, "end": v(-4.66, 4.37) * mm});
            skLineSegment(sketch, "E2045", {"start": v(-4.66, 4.37) * mm, "end": v(-4.66, 2.12) * mm});
            skLineSegment(sketch, "E2046", {"start": v(-4.66, 2.12) * mm, "end": v(-4.66, -0.13) * mm});
            skLineSegment(sketch, "E2047", {"start": v(-4.66, -0.13) * mm, "end": v(-4.68, -2.38) * mm});
            skLineSegment(sketch, "E2048", {"start": v(-4.68, -2.38) * mm, "end": v(-4.7, -4.62) * mm});
            skLineSegment(sketch, "E2049", {"start": v(-4.7, -4.62) * mm, "end": v(-4.65, -5.24) * mm});
            skLineSegment(sketch, "E2050", {"start": v(-4.65, -5.24) * mm, "end": v(-4.48, -5.72) * mm});
            skLineSegment(sketch, "E2051", {"start": v(-4.48, -5.72) * mm, "end": v(-4.14, -6.1) * mm});
            skLineSegment(sketch, "E2052", {"start": v(-4.14, -6.1) * mm, "end": v(-3.6, -6.39) * mm});
            skLineSegment(sketch, "E2053", {"start": v(-3.6, -6.39) * mm, "end": v(-2.8, -6.74) * mm});
            skLineSegment(sketch, "E2054", {"start": v(-2.8, -6.74) * mm, "end": v(-2.07, -7.16) * mm});
            skLineSegment(sketch, "E2055", {"start": v(-2.07, -7.16) * mm, "end": v(-1.4, -7.66) * mm});
            skLineSegment(sketch, "E2056", {"start": v(-1.4, -7.66) * mm, "end": v(-0.78, -8.26) * mm});
            skLineSegment(sketch, "E2057", {"start": v(-0.78, -8.26) * mm, "end": v(-0.5, -8.76) * mm});
            skLineSegment(sketch, "E2058", {"start": v(-0.5, -8.76) * mm, "end": v(-0.5, -9.22) * mm});
            skLineSegment(sketch, "E2059", {"start": v(-0.5, -9.22) * mm, "end": v(-0.76, -9.59) * mm});
            skLineSegment(sketch, "E2060", {"start": v(-0.76, -9.59) * mm, "end": v(-1.28, -9.8) * mm});
            skLineSegment(sketch, "E2061", {"start": v(-1.28, -9.8) * mm, "end": v(-1.78, -9.86) * mm});
            skLineSegment(sketch, "E2062", {"start": v(-1.78, -9.86) * mm, "end": v(-2.29, -9.9) * mm});
            skLineSegment(sketch, "E2063", {"start": v(-2.29, -9.9) * mm, "end": v(-2.8, -9.92) * mm});
            skLineSegment(sketch, "E2064", {"start": v(-2.8, -9.92) * mm, "end": v(-3.3, -9.94) * mm});
            skLineSegment(sketch, "E2065", {"start": v(-3.3, -9.94) * mm, "end": v(-3.78, -10) * mm});
            skLineSegment(sketch, "E2066", {"start": v(-3.78, -10) * mm, "end": v(-4.1, -10.13) * mm});
            skLineSegment(sketch, "E2067", {"start": v(-4.1, -10.13) * mm, "end": v(-4.34, -10.4) * mm});
            skLineSegment(sketch, "E2068", {"start": v(-4.34, -10.4) * mm, "end": v(-4.52, -10.84) * mm});
            skLineSegment(sketch, "E2069", {"start": v(-4.52, -10.84) * mm, "end": v(-4.86, -11.51) * mm});
            skLineSegment(sketch, "E2070", {"start": v(-4.86, -11.51) * mm, "end": v(-5.35, -11.88) * mm});
            skLineSegment(sketch, "E2071", {"start": v(-5.35, -11.88) * mm, "end": v(-5.95, -11.94) * mm});
            skLineSegment(sketch, "E2072", {"start": v(-5.95, -11.94) * mm, "end": v(-6.65, -11.67) * mm});
            skLineSegment(sketch, "E2073", {"start": v(-6.65, -11.67) * mm, "end": v(-6.97, -11.5) * mm});
            skLineSegment(sketch, "E2074", {"start": v(-6.97, -11.5) * mm, "end": v(-7.3, -11.42) * mm});
            skLineSegment(sketch, "E2075", {"start": v(-7.3, -11.42) * mm, "end": v(-7.65, -11.42) * mm});
            skLineSegment(sketch, "E2076", {"start": v(-7.65, -11.42) * mm, "end": v(-8.01, -11.5) * mm});
            skLineSegment(sketch, "E2077", {"start": v(-8.01, -11.5) * mm, "end": v(-8.62, -11.66) * mm});
            skLineSegment(sketch, "E2078", {"start": v(-8.62, -11.66) * mm, "end": v(-9.1, -11.64) * mm});
            skLineSegment(sketch, "E2079", {"start": v(-9.1, -11.64) * mm, "end": v(-9.51, -11.45) * mm});
            skLineSegment(sketch, "E2080", {"start": v(-9.51, -11.45) * mm, "end": v(-9.88, -11.07) * mm});
            skLineSegment(sketch, "E2081", {"start": v(-9.88, -11.07) * mm, "end": v(-10.25, -10.45) * mm});
            skLineSegment(sketch, "E2082", {"start": v(-10.25, -10.45) * mm, "end": v(-10.41, -9.8) * mm});
            skLineSegment(sketch, "E2083", {"start": v(-10.41, -9.8) * mm, "end": v(-10.37, -9.19) * mm});
            skLineSegment(sketch, "E2084", {"start": v(-10.37, -9.19) * mm, "end": v(-10.1, -8.63) * mm});
            skLineSegment(sketch, "E2085", {"start": v(-10.1, -8.63) * mm, "end": v(-9.8, -8.2) * mm});
            skLineSegment(sketch, "E2086", {"start": v(-9.8, -8.2) * mm, "end": v(-9.49, -7.78) * mm});
            skLineSegment(sketch, "E2087", {"start": v(-9.49, -7.78) * mm, "end": v(-9.17, -7.36) * mm});
            skLineSegment(sketch, "E2088", {"start": v(-9.17, -7.36) * mm, "end": v(-8.85, -6.94) * mm});
            skLineSegment(sketch, "E2089", {"start": v(-8.85, -6.94) * mm, "end": v(-8.59, -6.48) * mm});
            skLineSegment(sketch, "E2090", {"start": v(-8.59, -6.48) * mm, "end": v(-8.45, -6) * mm});
            skLineSegment(sketch, "E2091", {"start": v(-8.45, -6) * mm, "end": v(-8.41, -5.49) * mm});
            skLineSegment(sketch, "E2092", {"start": v(-8.41, -5.49) * mm, "end": v(-8.44, -4.95) * mm});
            skLineSegment(sketch, "E2093", {"start": v(-8.44, -4.95) * mm, "end": v(-8.49, -4.18) * mm});
            skLineSegment(sketch, "E2094", {"start": v(-8.49, -4.18) * mm, "end": v(-8.5, -3.41) * mm});
            skLineSegment(sketch, "E2095", {"start": v(-8.5, -3.41) * mm, "end": v(-8.51, -2.64) * mm});
            skLineSegment(sketch, "E2096", {"start": v(-8.51, -2.64) * mm, "end": v(-8.52, -1.86) * mm});
            skLineSegment(sketch, "E2097", {"start": v(-8.52, -1.86) * mm, "end": v(-8.52, -1.82) * mm});
            skLineSegment(sketch, "E2098", {"start": v(-8.52, -1.82) * mm, "end": v(-8.5, -1.78) * mm});
            skLineSegment(sketch, "E2099", {"start": v(-8.5, -1.78) * mm, "end": v(-8.5, -1.73) * mm});
            skLineSegment(sketch, "E2100", {"start": v(-8.5, -1.73) * mm, "end": v(-8.5, -1.69) * mm});
            skLineSegment(sketch, "E2101", {"start": v(-8.5, -1.69) * mm, "end": v(-8.5, -0.82) * mm});
            skLineSegment(sketch, "E2102", {"start": v(-8.5, -0.82) * mm, "end": v(-8.52, 0.04) * mm});
            skLineSegment(sketch, "E2103", {"start": v(-8.52, 0.04) * mm, "end": v(-8.54, 0.9) * mm});
            skLineSegment(sketch, "E2104", {"start": v(-8.54, 0.9) * mm, "end": v(-8.57, 1.77) * mm});
            skLineSegment(sketch, "E2105", {"start": v(-8.57, 1.77) * mm, "end": v(-8.62, 2.57) * mm});
            skLineSegment(sketch, "E2106", {"start": v(-8.62, 2.57) * mm, "end": v(-8.68, 3.37) * mm});
            skLineSegment(sketch, "E2107", {"start": v(-8.68, 3.37) * mm, "end": v(-8.74, 4.18) * mm});
            skLineSegment(sketch, "E2108", {"start": v(-8.74, 4.18) * mm, "end": v(-8.8, 4.98) * mm});
            skLineSegment(sketch, "E2109", {"start": v(-8.8, 4.98) * mm, "end": v(-8.78, 5.12) * mm});
            skLineSegment(sketch, "E2110", {"start": v(-8.78, 5.12) * mm, "end": v(-8.71, 5.26) * mm});
            skLineSegment(sketch, "E2111", {"start": v(-8.71, 5.26) * mm, "end": v(-8.63, 5.39) * mm});
            skLineSegment(sketch, "E2112", {"start": v(-8.63, 5.39) * mm, "end": v(-8.53, 5.46) * mm});
            skLineSegment(sketch, "E2113", {"start": v(-8.53, 5.46) * mm, "end": v(-8.38, 5.49) * mm});
            skLineSegment(sketch, "E2114", {"start": v(-8.38, 5.49) * mm, "end": v(-8.22, 5.47) * mm});
            skLineSegment(sketch, "E2115", {"start": v(-8.22, 5.47) * mm, "end": v(-8.06, 5.43) * mm});
            skLineSegment(sketch, "E2116", {"start": v(-8.06, 5.43) * mm, "end": v(-7.93, 5.36) * mm});
            skLineSegment(sketch, "E2117", {"start": v(-7.93, 5.36) * mm, "end": v(-7.52, 4.94) * mm});
            skLineSegment(sketch, "E2118", {"start": v(-7.52, 4.94) * mm, "end": v(-7.28, 4.45) * mm});
            skLineSegment(sketch, "E2119", {"start": v(-7.28, 4.45) * mm, "end": v(-7.17, 3.9) * mm});
            skLineSegment(sketch, "E2120", {"start": v(-7.17, 3.9) * mm, "end": v(-7.16, 3.32) * mm});
            skLineSegment(sketch, "E2121", {"start": v(-7.16, 3.32) * mm, "end": v(-7.23, 1.87) * mm});
            skLineSegment(sketch, "E2122", {"start": v(-7.23, 1.87) * mm, "end": v(-7.3, 0.42) * mm});
            skLineSegment(sketch, "E2123", {"start": v(-7.3, 0.42) * mm, "end": v(-7.36, -1.03) * mm});
            skLineSegment(sketch, "E2124", {"start": v(-7.36, -1.03) * mm, "end": v(-7.4, -2.48) * mm});
            skLineSegment(sketch, "E2125", {"start": v(-7.4, -2.48) * mm, "end": v(-7.37, -3.15) * mm});
            skLineSegment(sketch, "E2126", {"start": v(-7.37, -3.15) * mm, "end": v(-7.3, -3.82) * mm});
            skLineSegment(sketch, "E2127", {"start": v(-7.3, -3.82) * mm, "end": v(-7.2, -4.49) * mm});
            skLineSegment(sketch, "E2128", {"start": v(-7.2, -4.49) * mm, "end": v(-7.1, -5.15) * mm});
            skLineSegment(sketch, "E2129", {"start": v(-7.1, -5.15) * mm, "end": v(-7.08, -5.96) * mm});
            skLineSegment(sketch, "E2130", {"start": v(-7.08, -5.96) * mm, "end": v(-7.23, -6.71) * mm});
            skLineSegment(sketch, "E2131", {"start": v(-7.23, -6.71) * mm, "end": v(-7.57, -7.4) * mm});
            skLineSegment(sketch, "E2132", {"start": v(-7.57, -7.4) * mm, "end": v(-8.12, -8) * mm});
            skLineSegment(sketch, "E2133", {"start": v(-8.12, -8) * mm, "end": v(-8.4, -8.3) * mm});
            skLineSegment(sketch, "E2134", {"start": v(-8.4, -8.3) * mm, "end": v(-8.64, -8.61) * mm});
            skLineSegment(sketch, "E2135", {"start": v(-8.64, -8.61) * mm, "end": v(-8.86, -8.96) * mm});
            skLineSegment(sketch, "E2136", {"start": v(-8.86, -8.96) * mm, "end": v(-9.07, -9.3) * mm});
            skLineSegment(sketch, "E2137", {"start": v(-9.07, -9.3) * mm, "end": v(-9.18, -9.59) * mm});
            skLineSegment(sketch, "E2138", {"start": v(-9.18, -9.59) * mm, "end": v(-9.17, -9.85) * mm});
            skLineSegment(sketch, "E2139", {"start": v(-9.17, -9.85) * mm, "end": v(-9.03, -10.07) * mm});
            skLineSegment(sketch, "E2140", {"start": v(-9.03, -10.07) * mm, "end": v(-8.77, -10.24) * mm});
            skLineSegment(sketch, "E2141", {"start": v(-8.77, -10.24) * mm, "end": v(-8.46, -10.3) * mm});
            skLineSegment(sketch, "E2142", {"start": v(-8.46, -10.3) * mm, "end": v(-8.19, -10.22) * mm});
            skLineSegment(sketch, "E2143", {"start": v(-8.19, -10.22) * mm, "end": v(-7.96, -10.02) * mm});
            skLineSegment(sketch, "E2144", {"start": v(-7.96, -10.02) * mm, "end": v(-7.8, -9.72) * mm});
            skLineSegment(sketch, "E2145", {"start": v(-7.8, -9.72) * mm, "end": v(-7.7, -9.47) * mm});
            skLineSegment(sketch, "E2146", {"start": v(-7.7, -9.47) * mm, "end": v(-7.56, -9.22) * mm});
            skLineSegment(sketch, "E2147", {"start": v(-7.56, -9.22) * mm, "end": v(-7.43, -8.98) * mm});
            skLineSegment(sketch, "E2148", {"start": v(-7.43, -8.98) * mm, "end": v(-7.3, -8.74) * mm});
            skLineSegment(sketch, "E2149", {"start": v(-9.74, 14.27) * mm, "end": v(-10.83, 14.41) * mm});
            skLineSegment(sketch, "E2150", {"start": v(-10.83, 14.41) * mm, "end": v(-11.99, 15.1) * mm});
            skLineSegment(sketch, "E2151", {"start": v(-11.99, 15.1) * mm, "end": v(-12.96, 16.14) * mm});
            skLineSegment(sketch, "E2152", {"start": v(-12.96, 16.14) * mm, "end": v(-13.48, 17.3) * mm});
            skLineSegment(sketch, "E2153", {"start": v(-13.48, 17.3) * mm, "end": v(-13.5, 17.67) * mm});
            skLineSegment(sketch, "E2154", {"start": v(-13.5, 17.67) * mm, "end": v(-13.42, 18.07) * mm});
            skLineSegment(sketch, "E2155", {"start": v(-13.42, 18.07) * mm, "end": v(-13.3, 18.45) * mm});
            skLineSegment(sketch, "E2156", {"start": v(-13.3, 18.45) * mm, "end": v(-13.12, 18.8) * mm});
            skLineSegment(sketch, "E2157", {"start": v(-13.12, 18.8) * mm, "end": v(-12.37, 19.79) * mm});
            skLineSegment(sketch, "E2158", {"start": v(-12.37, 19.79) * mm, "end": v(-11.46, 20.55) * mm});
            skLineSegment(sketch, "E2159", {"start": v(-11.46, 20.55) * mm, "end": v(-10.4, 21.1) * mm});
            skLineSegment(sketch, "E2160", {"start": v(-10.4, 21.1) * mm, "end": v(-9.23, 21.48) * mm});
            skLineSegment(sketch, "E2161", {"start": v(-9.23, 21.48) * mm, "end": v(-8.32, 21.64) * mm});
            skLineSegment(sketch, "E2162", {"start": v(-8.32, 21.64) * mm, "end": v(-7.42, 21.65) * mm});
            skLineSegment(sketch, "E2163", {"start": v(-7.42, 21.65) * mm, "end": v(-6.56, 21.47) * mm});
            skLineSegment(sketch, "E2164", {"start": v(-6.56, 21.47) * mm, "end": v(-5.72, 21.04) * mm});
            skLineSegment(sketch, "E2165", {"start": v(-5.72, 21.04) * mm, "end": v(-4.61, 19.87) * mm});
            skLineSegment(sketch, "E2166", {"start": v(-4.61, 19.87) * mm, "end": v(-4.09, 18.37) * mm});
            skLineSegment(sketch, "E2167", {"start": v(-4.09, 18.37) * mm, "end": v(-4.33, 16.8) * mm});
            skLineSegment(sketch, "E2168", {"start": v(-4.33, 16.8) * mm, "end": v(-5.54, 15.4) * mm});
            skLineSegment(sketch, "E2169", {"start": v(-5.54, 15.4) * mm, "end": v(-6.4, 14.91) * mm});
            skLineSegment(sketch, "E2170", {"start": v(-6.4, 14.91) * mm, "end": v(-7.34, 14.56) * mm});
            skLineSegment(sketch, "E2171", {"start": v(-7.34, 14.56) * mm, "end": v(-8.44, 14.35) * mm});
            skLineSegment(sketch, "E2172", {"start": v(-8.44, 14.35) * mm, "end": v(-9.74, 14.27) * mm});
            skLineSegment(sketch, "E2173", {"start": v(-11.6, 16.55) * mm, "end": v(-10.97, 15.81) * mm});
            skLineSegment(sketch, "E2174", {"start": v(-10.97, 15.81) * mm, "end": v(-10.33, 15.4) * mm});
            skLineSegment(sketch, "E2175", {"start": v(-10.33, 15.4) * mm, "end": v(-9.62, 15.31) * mm});
            skLineSegment(sketch, "E2176", {"start": v(-9.62, 15.31) * mm, "end": v(-8.75, 15.5) * mm});
            skLineSegment(sketch, "E2177", {"start": v(-8.75, 15.5) * mm, "end": v(-8.3, 15.63) * mm});
            skLineSegment(sketch, "E2178", {"start": v(-8.3, 15.63) * mm, "end": v(-7.84, 15.78) * mm});
            skLineSegment(sketch, "E2179", {"start": v(-7.84, 15.78) * mm, "end": v(-7.38, 15.92) * mm});
            skLineSegment(sketch, "E2180", {"start": v(-7.38, 15.92) * mm, "end": v(-6.93, 16.07) * mm});
            skLineSegment(sketch, "E2181", {"start": v(-6.93, 16.07) * mm, "end": v(-5.76, 16.75) * mm});
            skLineSegment(sketch, "E2182", {"start": v(-5.76, 16.75) * mm, "end": v(-5.2, 17.73) * mm});
            skLineSegment(sketch, "E2183", {"start": v(-5.2, 17.73) * mm, "end": v(-5.26, 18.85) * mm});
            skLineSegment(sketch, "E2184", {"start": v(-5.26, 18.85) * mm, "end": v(-6, 19.96) * mm});
            skLineSegment(sketch, "E2185", {"start": v(-6, 19.96) * mm, "end": v(-6.32, 20.24) * mm});
            skLineSegment(sketch, "E2186", {"start": v(-6.32, 20.24) * mm, "end": v(-6.55, 20.3) * mm});
            skLineSegment(sketch, "E2187", {"start": v(-6.55, 20.3) * mm, "end": v(-6.74, 20.15) * mm});
            skLineSegment(sketch, "E2188", {"start": v(-6.74, 20.15) * mm, "end": v(-6.97, 19.77) * mm});
            skLineSegment(sketch, "E2189", {"start": v(-6.97, 19.77) * mm, "end": v(-7.36, 19.1) * mm});
            skLineSegment(sketch, "E2190", {"start": v(-7.36, 19.1) * mm, "end": v(-7.76, 18.44) * mm});
            skLineSegment(sketch, "E2191", {"start": v(-7.76, 18.44) * mm, "end": v(-8.18, 17.8) * mm});
            skLineSegment(sketch, "E2192", {"start": v(-8.18, 17.8) * mm, "end": v(-8.6, 17.14) * mm});
            skLineSegment(sketch, "E2193", {"start": v(-8.6, 17.14) * mm, "end": v(-8.82, 16.9) * mm});
            skLineSegment(sketch, "E2194", {"start": v(-8.82, 16.9) * mm, "end": v(-9.09, 16.73) * mm});
            skLineSegment(sketch, "E2195", {"start": v(-9.09, 16.73) * mm, "end": v(-9.4, 16.65) * mm});
            skLineSegment(sketch, "E2196", {"start": v(-9.4, 16.65) * mm, "end": v(-9.74, 16.63) * mm});
            skLineSegment(sketch, "E2197", {"start": v(-9.74, 16.63) * mm, "end": v(-10.18, 16.63) * mm});
            skLineSegment(sketch, "E2198", {"start": v(-10.18, 16.63) * mm, "end": v(-10.64, 16.61) * mm});
            skLineSegment(sketch, "E2199", {"start": v(-10.64, 16.61) * mm, "end": v(-11.1, 16.58) * mm});
            skLineSegment(sketch, "E2200", {"start": v(-11.1, 16.58) * mm, "end": v(-11.6, 16.55) * mm});
            skLineSegment(sketch, "E2201", {"start": v(7.17, -13.1) * mm, "end": v(6.97, -12.92) * mm});
            skLineSegment(sketch, "E2202", {"start": v(6.97, -12.92) * mm, "end": v(6.77, -12.75) * mm});
            skLineSegment(sketch, "E2203", {"start": v(6.77, -12.75) * mm, "end": v(6.58, -12.59) * mm});
            skLineSegment(sketch, "E2204", {"start": v(6.58, -12.59) * mm, "end": v(6.39, -12.43) * mm});
            skLineSegment(sketch, "E2205", {"start": v(6.39, -12.43) * mm, "end": v(6.67, -12.1) * mm});
            skLineSegment(sketch, "E2206", {"start": v(6.67, -12.1) * mm, "end": v(6.95, -12) * mm});
            skLineSegment(sketch, "E2207", {"start": v(6.95, -12) * mm, "end": v(7.3, -12.15) * mm});
            skLineSegment(sketch, "E2208", {"start": v(7.3, -12.15) * mm, "end": v(7.81, -12.55) * mm});
            skLineSegment(sketch, "E2209", {"start": v(7.81, -12.55) * mm, "end": v(7.66, -12.68) * mm});
            skLineSegment(sketch, "E2210", {"start": v(7.66, -12.68) * mm, "end": v(7.5, -12.82) * mm});
            skLineSegment(sketch, "E2211", {"start": v(7.5, -12.82) * mm, "end": v(7.34, -12.95) * mm});
            skLineSegment(sketch, "E2212", {"start": v(7.34, -12.95) * mm, "end": v(7.17, -13.1) * mm});
            skLineSegment(sketch, "E2213", {"start": v(8.34, -7.58) * mm, "end": v(8.22, -7.44) * mm});
            skLineSegment(sketch, "E2214", {"start": v(8.22, -7.44) * mm, "end": v(8.1, -7.3) * mm});
            skLineSegment(sketch, "E2215", {"start": v(8.1, -7.3) * mm, "end": v(8, -7.2) * mm});
            skLineSegment(sketch, "E2216", {"start": v(8, -7.2) * mm, "end": v(7.91, -7.08) * mm});
            skLineSegment(sketch, "E2217", {"start": v(7.91, -7.08) * mm, "end": v(8.36, -6.68) * mm});
            skLineSegment(sketch, "E2218", {"start": v(8.36, -6.68) * mm, "end": v(8.7, -6.54) * mm});
            skLineSegment(sketch, "E2219", {"start": v(8.7, -6.54) * mm, "end": v(8.95, -6.66) * mm});
            skLineSegment(sketch, "E2220", {"start": v(8.95, -6.66) * mm, "end": v(9.2, -7.05) * mm});
            skLineSegment(sketch, "E2221", {"start": v(9.2, -7.05) * mm, "end": v(9, -7.17) * mm});
            skLineSegment(sketch, "E2222", {"start": v(9, -7.17) * mm, "end": v(8.79, -7.3) * mm});
            skLineSegment(sketch, "E2223", {"start": v(8.79, -7.3) * mm, "end": v(8.57, -7.43) * mm});
            skLineSegment(sketch, "E2224", {"start": v(8.57, -7.43) * mm, "end": v(8.34, -7.58) * mm});
            skLineSegment(sketch, "E2225", {"start": v(9.21, -15.34) * mm, "end": v(8.78, -15.67) * mm});
            skLineSegment(sketch, "E2226", {"start": v(8.78, -15.67) * mm, "end": v(8.5, -15.8) * mm});
            skLineSegment(sketch, "E2227", {"start": v(8.5, -15.8) * mm, "end": v(8.24, -15.7) * mm});
            skLineSegment(sketch, "E2228", {"start": v(8.24, -15.7) * mm, "end": v(7.94, -15.41) * mm});
            skLineSegment(sketch, "E2229", {"start": v(7.94, -15.41) * mm, "end": v(8.32, -15) * mm});
            skLineSegment(sketch, "E2230", {"start": v(8.32, -15) * mm, "end": v(8.59, -14.87) * mm});
            skLineSegment(sketch, "E2231", {"start": v(8.59, -14.87) * mm, "end": v(8.85, -14.98) * mm});
            skLineSegment(sketch, "E2232", {"start": v(8.85, -14.98) * mm, "end": v(9.21, -15.34) * mm});
            skLineSegment(sketch, "E2233", {"start": v(2.45, -1.86) * mm, "end": v(2.7, -1.83) * mm});
            skLineSegment(sketch, "E2234", {"start": v(2.7, -1.83) * mm, "end": v(2.95, -1.8) * mm});
            skLineSegment(sketch, "E2235", {"start": v(2.95, -1.8) * mm, "end": v(3.2, -1.79) * mm});
            skLineSegment(sketch, "E2236", {"start": v(3.2, -1.79) * mm, "end": v(3.45, -1.8) * mm});
            skLineSegment(sketch, "E2237", {"start": v(3.45, -1.8) * mm, "end": v(3.54, -1.83) * mm});
            skLineSegment(sketch, "E2238", {"start": v(3.54, -1.83) * mm, "end": v(3.62, -1.93) * mm});
            skLineSegment(sketch, "E2239", {"start": v(3.62, -1.93) * mm, "end": v(3.7, -2.04) * mm});
            skLineSegment(sketch, "E2240", {"start": v(3.7, -2.04) * mm, "end": v(3.8, -2.15) * mm});
            skLineSegment(sketch, "E2241", {"start": v(3.8, -2.15) * mm, "end": v(3.7, -2.23) * mm});
            skLineSegment(sketch, "E2242", {"start": v(3.7, -2.23) * mm, "end": v(3.59, -2.31) * mm});
            skLineSegment(sketch, "E2243", {"start": v(3.59, -2.31) * mm, "end": v(3.5, -2.38) * mm});
            skLineSegment(sketch, "E2244", {"start": v(3.5, -2.38) * mm, "end": v(3.4, -2.4) * mm});
            skLineSegment(sketch, "E2245", {"start": v(3.4, -2.4) * mm, "end": v(3.15, -2.38) * mm});
            skLineSegment(sketch, "E2246", {"start": v(3.15, -2.38) * mm, "end": v(2.91, -2.33) * mm});
            skLineSegment(sketch, "E2247", {"start": v(2.91, -2.33) * mm, "end": v(2.67, -2.27) * mm});
            skLineSegment(sketch, "E2248", {"start": v(2.67, -2.27) * mm, "end": v(2.44, -2.21) * mm});
            skLineSegment(sketch, "E2249", {"start": v(2.44, -2.21) * mm, "end": v(2.44, -2.12) * mm});
            skLineSegment(sketch, "E2250", {"start": v(2.44, -2.12) * mm, "end": v(2.45, -2.04) * mm});
            skLineSegment(sketch, "E2251", {"start": v(2.45, -2.04) * mm, "end": v(2.45, -1.95) * mm});
            skLineSegment(sketch, "E2252", {"start": v(2.45, -1.95) * mm, "end": v(2.45, -1.86) * mm});
            skLineSegment(sketch, "E2253", {"start": v(8.56, -10.13) * mm, "end": v(8.47, -10.24) * mm});
            skLineSegment(sketch, "E2254", {"start": v(8.47, -10.24) * mm, "end": v(8.38, -10.33) * mm});
            skLineSegment(sketch, "E2255", {"start": v(8.38, -10.33) * mm, "end": v(8.28, -10.43) * mm});
            skLineSegment(sketch, "E2256", {"start": v(8.28, -10.43) * mm, "end": v(8.18, -10.54) * mm});
            skLineSegment(sketch, "E2257", {"start": v(8.18, -10.54) * mm, "end": v(8.03, -10.4) * mm});
            skLineSegment(sketch, "E2258", {"start": v(8.03, -10.4) * mm, "end": v(7.88, -10.29) * mm});
            skLineSegment(sketch, "E2259", {"start": v(7.88, -10.29) * mm, "end": v(7.75, -10.17) * mm});
            skLineSegment(sketch, "E2260", {"start": v(7.75, -10.17) * mm, "end": v(7.61, -10.06) * mm});
            skLineSegment(sketch, "E2261", {"start": v(7.61, -10.06) * mm, "end": v(7.87, -9.83) * mm});
            skLineSegment(sketch, "E2262", {"start": v(7.87, -9.83) * mm, "end": v(8.05, -9.75) * mm});
            skLineSegment(sketch, "E2263", {"start": v(8.05, -9.75) * mm, "end": v(8.25, -9.86) * mm});
            skLineSegment(sketch, "E2264", {"start": v(8.25, -9.86) * mm, "end": v(8.56, -10.13) * mm});
            skLineSegment(sketch, "E2265", {"start": v(18.62, 1.9) * mm, "end": v(18.4, 2.14) * mm});
            skLineSegment(sketch, "E2266", {"start": v(18.4, 2.14) * mm, "end": v(18.2, 2.34) * mm});
            skLineSegment(sketch, "E2267", {"start": v(18.2, 2.34) * mm, "end": v(18.07, 2.5) * mm});
            skLineSegment(sketch, "E2268", {"start": v(18.07, 2.5) * mm, "end": v(18.03, 2.6) * mm});
            skLineSegment(sketch, "E2269", {"start": v(18.03, 2.6) * mm, "end": v(18.15, 2.8) * mm});
            skLineSegment(sketch, "E2270", {"start": v(18.15, 2.8) * mm, "end": v(18.3, 2.98) * mm});
            skLineSegment(sketch, "E2271", {"start": v(18.3, 2.98) * mm, "end": v(18.47, 3.14) * mm});
            skLineSegment(sketch, "E2272", {"start": v(18.47, 3.14) * mm, "end": v(18.66, 3.24) * mm});
            skLineSegment(sketch, "E2273", {"start": v(18.66, 3.24) * mm, "end": v(18.89, 3.25) * mm});
            skLineSegment(sketch, "E2274", {"start": v(18.89, 3.25) * mm, "end": v(19.07, 3.14) * mm});
            skLineSegment(sketch, "E2275", {"start": v(19.07, 3.14) * mm, "end": v(19.17, 2.96) * mm});
            skLineSegment(sketch, "E2276", {"start": v(19.17, 2.96) * mm, "end": v(19.18, 2.72) * mm});
            skLineSegment(sketch, "E2277", {"start": v(19.18, 2.72) * mm, "end": v(19.1, 2.54) * mm});
            skLineSegment(sketch, "E2278", {"start": v(19.1, 2.54) * mm, "end": v(18.98, 2.35) * mm});
            skLineSegment(sketch, "E2279", {"start": v(18.98, 2.35) * mm, "end": v(18.8, 2.14) * mm});
            skLineSegment(sketch, "E2280", {"start": v(18.8, 2.14) * mm, "end": v(18.62, 1.9) * mm});
            skLineSegment(sketch, "E2281", {"start": v(19.9, 4.43) * mm, "end": v(19.8, 4.53) * mm});
            skLineSegment(sketch, "E2282", {"start": v(19.8, 4.53) * mm, "end": v(19.69, 4.63) * mm});
            skLineSegment(sketch, "E2283", {"start": v(19.69, 4.63) * mm, "end": v(19.58, 4.72) * mm});
            skLineSegment(sketch, "E2284", {"start": v(19.58, 4.72) * mm, "end": v(19.47, 4.83) * mm});
            skLineSegment(sketch, "E2285", {"start": v(19.47, 4.83) * mm, "end": v(19.6, 5.02) * mm});
            skLineSegment(sketch, "E2286", {"start": v(19.6, 5.02) * mm, "end": v(19.73, 5.2) * mm});
            skLineSegment(sketch, "E2287", {"start": v(19.73, 5.2) * mm, "end": v(19.86, 5.37) * mm});
            skLineSegment(sketch, "E2288", {"start": v(19.86, 5.37) * mm, "end": v(19.98, 5.55) * mm});
            skLineSegment(sketch, "E2289", {"start": v(19.98, 5.55) * mm, "end": v(20.3, 5.26) * mm});
            skLineSegment(sketch, "E2290", {"start": v(20.3, 5.26) * mm, "end": v(20.39, 5.03) * mm});
            skLineSegment(sketch, "E2291", {"start": v(20.39, 5.03) * mm, "end": v(20.26, 4.78) * mm});
            skLineSegment(sketch, "E2292", {"start": v(20.26, 4.78) * mm, "end": v(19.9, 4.43) * mm});
            skLineSegment(sketch, "E2293", {"start": v(-11.6, 16.55) * mm, "end": v(-11.1, 16.58) * mm});
            skLineSegment(sketch, "E2294", {"start": v(-11.1, 16.58) * mm, "end": v(-10.64, 16.61) * mm});
            skLineSegment(sketch, "E2295", {"start": v(-10.64, 16.61) * mm, "end": v(-10.18, 16.63) * mm});
            skLineSegment(sketch, "E2296", {"start": v(-10.18, 16.63) * mm, "end": v(-9.74, 16.63) * mm});
            skLineSegment(sketch, "E2297", {"start": v(-9.74, 16.63) * mm, "end": v(-9.4, 16.65) * mm});
            skLineSegment(sketch, "E2298", {"start": v(-9.4, 16.65) * mm, "end": v(-9.09, 16.73) * mm});
            skLineSegment(sketch, "E2299", {"start": v(-9.09, 16.73) * mm, "end": v(-8.82, 16.9) * mm});
            skLineSegment(sketch, "E2300", {"start": v(-8.82, 16.9) * mm, "end": v(-8.6, 17.14) * mm});
            skLineSegment(sketch, "E2301", {"start": v(-8.6, 17.14) * mm, "end": v(-8.18, 17.8) * mm});
            skLineSegment(sketch, "E2302", {"start": v(-8.18, 17.8) * mm, "end": v(-7.76, 18.44) * mm});
            skLineSegment(sketch, "E2303", {"start": v(-7.76, 18.44) * mm, "end": v(-7.36, 19.1) * mm});
            skLineSegment(sketch, "E2304", {"start": v(-7.36, 19.1) * mm, "end": v(-6.97, 19.77) * mm});
            skLineSegment(sketch, "E2305", {"start": v(-6.97, 19.77) * mm, "end": v(-6.74, 20.15) * mm});
            skLineSegment(sketch, "E2306", {"start": v(-6.74, 20.15) * mm, "end": v(-6.55, 20.3) * mm});
            skLineSegment(sketch, "E2307", {"start": v(-6.55, 20.3) * mm, "end": v(-6.32, 20.24) * mm});
            skLineSegment(sketch, "E2308", {"start": v(-6.32, 20.24) * mm, "end": v(-6, 19.96) * mm});
            skLineSegment(sketch, "E2309", {"start": v(-6, 19.96) * mm, "end": v(-5.26, 18.85) * mm});
            skLineSegment(sketch, "E2310", {"start": v(-5.26, 18.85) * mm, "end": v(-5.2, 17.73) * mm});
            skLineSegment(sketch, "E2311", {"start": v(-5.2, 17.73) * mm, "end": v(-5.76, 16.75) * mm});
            skLineSegment(sketch, "E2312", {"start": v(-5.76, 16.75) * mm, "end": v(-6.93, 16.07) * mm});
            skLineSegment(sketch, "E2313", {"start": v(-6.93, 16.07) * mm, "end": v(-7.38, 15.92) * mm});
            skLineSegment(sketch, "E2314", {"start": v(-7.38, 15.92) * mm, "end": v(-7.84, 15.78) * mm});
            skLineSegment(sketch, "E2315", {"start": v(-7.84, 15.78) * mm, "end": v(-8.3, 15.63) * mm});
            skLineSegment(sketch, "E2316", {"start": v(-8.3, 15.63) * mm, "end": v(-8.75, 15.5) * mm});
            skLineSegment(sketch, "E2317", {"start": v(-8.75, 15.5) * mm, "end": v(-9.62, 15.31) * mm});
            skLineSegment(sketch, "E2318", {"start": v(-9.62, 15.31) * mm, "end": v(-10.33, 15.4) * mm});
            skLineSegment(sketch, "E2319", {"start": v(-10.33, 15.4) * mm, "end": v(-10.97, 15.81) * mm});
            skLineSegment(sketch, "E2320", {"start": v(-10.97, 15.81) * mm, "end": v(-11.6, 16.55) * mm});
            skCircle(sketch, "E2321", {"center": v(-10.33, 33.48) * mm, "radius": 5 * mm});
            skPoint(sketch, "E2321.second.point", {"position": v(-9.66, 38.44) * mm});
            skPoint(sketch, "E2321.third.point", {"position": v(-15.14, 34.82) * mm});
            skCircle(sketch, "E2322.0", {"center": v(-10.33, 33.48) * mm, "radius": 2.8 * mm});
            skLineSegment(sketch, "E2323", {"start": v(-14.98, 29.18) * mm, "end": v(-28.82, 40.14) * mm});
            skLineSegment(sketch, "E2324", {"start": v(-28.82, 40.14) * mm, "end": v(-19.08, 26.65) * mm});
            skLineSegment(sketch, "E2325.0", {"start": v(-23.29, 34.36) * mm, "end": v(-18.2, 27.3) * mm});
            skLineSegment(sketch, "E2325.1", {"start": v(-16.04, 28.62) * mm, "end": v(-23.29, 34.36) * mm});
            skSolve(sketch);
        }
        {
            var Q0;
            Q0=makeQuery(id+"F0.imprint","IMPRINT",FACE,{"disambiguationData":[TD([[makeQuery(id+"F0.imprint","IMPRINT",EDGE,{"derivedFrom":sQuery(id+"F0.wireOp",EDGE,"E2149")}),-1.0]])]});
            var Q1;
            Q1=makeQuery(id+"F0.imprint","IMPRINT",FACE,{"disambiguationData":[TD([[makeQuery(id+"F0.imprint","IMPRINT",EDGE,{"derivedFrom":sQuery(id+"F0.wireOp",EDGE,"E1981")}),-1.0]])]});
            var Q2;
            Q2=makeQuery(id+"F0.imprint","IMPRINT",FACE,{"disambiguationData":[TD([[makeQuery(id+"F0.imprint","IMPRINT",EDGE,{"derivedFrom":sQuery(id+"F0.wireOp",EDGE,"E2293")}),-1.0]])]});
            var Q3;
            Q3=makeQuery(id+"F0.imprint","IMPRINT",FACE,{"disambiguationData":[TD([[makeQuery(id+"F0.imprint","IMPRINT",EDGE,{"derivedFrom":sQuery(id+"F0.wireOp",EDGE,"E1765")}),-1.0]])]});
            var Q4;
            {var subQ1=sQuery(id+"F0.wireOp",EDGE,"E523");Q4=makeQuery(id+"F0.imprint","IMPRINT",FACE,{"disambiguationData":[TD([[makeQuery(id+"F0.imprint","IMPRINT",EDGE,{"derivedFrom":subQ1}),1.0]])]});}
            var Q5;
            {var subQ0=sQuery(id+"F0.wireOp",EDGE,"E227");Q5=makeQuery(id+"F0.imprint","IMPRINT",FACE,{"disambiguationData":[TD([[makeQuery(id+"F0.imprint","IMPRINT",EDGE,{"derivedFrom":subQ0}),-1.0]])]});}
            var Q6;
            Q6=makeQuery(id+"F0.imprint","IMPRINT",FACE,{"disambiguationData":[TD([[makeQuery(id+"F0.imprint","IMPRINT",EDGE,{"derivedFrom":sQuery(id+"F0.wireOp",EDGE,"E1157")}),-1.0]])]});
            var Q7;
            Q7=makeQuery(id+"F0.imprint","IMPRINT",FACE,{"disambiguationData":[TD([[makeQuery(id+"F0.imprint","IMPRINT",EDGE,{"derivedFrom":sQuery(id+"F0.wireOp",EDGE,"E223")}),-1.0]])]});
            var Q8;
            Q8=makeQuery(id+"F0.imprint","IMPRINT",FACE,{"disambiguationData":[TD([[makeQuery(id+"F0.imprint","IMPRINT",EDGE,{"derivedFrom":sQuery(id+"F0.wireOp",EDGE,"E1901")}),-1.0]])]});
            var Q9;
            Q9=makeQuery(id+"F0.imprint","IMPRINT",FACE,{"disambiguationData":[TD([[makeQuery(id+"F0.imprint","IMPRINT",EDGE,{"derivedFrom":sQuery(id+"F0.wireOp",EDGE,"E1961")}),-1.0]])]});
            var Q10;
            {var subQ1=sQuery(id+"F0.wireOp",EDGE,"E223");Q10=makeQuery(id+"F0.imprint","IMPRINT",FACE,{"disambiguationData":[TD([[makeQuery(id+"F0.imprint","IMPRINT",EDGE,{"derivedFrom":subQ1}),1.0]])]});}
            var Q11;
            {var subQ0=sQuery(id+"F0.wireOp",EDGE,"E1067");Q11=makeQuery(id+"F0.imprint","IMPRINT",FACE,{"disambiguationData":[TD([[makeQuery(id+"F0.imprint","IMPRINT",EDGE,{"derivedFrom":subQ0}),-1.0]])]});}
            var Q12;
            {var subQ0=sQuery(id+"F0.wireOp",EDGE,"E2321");var subQ1=sQuery(id+"F0.wireOp",EDGE,"E1236");var subQ3=makeQuery(id+"F0.imprint","INTERSECT",VERTEX,{"derivedFrom":[subQ1,subQ0]});Q12=makeQuery(id+"F0.imprint","IMPRINT",FACE,{"disambiguationData":[TD([[makeQuery(id+"F0.imprint","IMPRINT",EDGE,{"disambiguationData":[TD([[subQ3,1.0]])],"derivedFrom":subQ1}),-1.0]])]});}
            var Q13;
            Q13=makeQuery(id+"F0.imprint","IMPRINT",FACE,{"disambiguationData":[TD([[makeQuery(id+"F0.imprint","IMPRINT",EDGE,{"derivedFrom":sQuery(id+"F0.wireOp",EDGE,"E2201")}),-1.0]])]});
            var Q14;
            Q14=makeQuery(id+"F0.imprint","IMPRINT",FACE,{"disambiguationData":[TD([[makeQuery(id+"F0.imprint","IMPRINT",EDGE,{"derivedFrom":sQuery(id+"F0.wireOp",EDGE,"E2225")}),-1.0]])]});
            var Q15;
            Q15=makeQuery(id+"F0.imprint","IMPRINT",FACE,{"disambiguationData":[TD([[makeQuery(id+"F0.imprint","IMPRINT",EDGE,{"derivedFrom":sQuery(id+"F0.wireOp",EDGE,"E2281")}),-1.0]])]});
            var Q16;
            Q16=makeQuery(id+"F0.imprint","IMPRINT",FACE,{"disambiguationData":[TD([[makeQuery(id+"F0.imprint","IMPRINT",EDGE,{"derivedFrom":sQuery(id+"F0.wireOp",EDGE,"E2213")}),-1.0]])]});
            var Q17;
            Q17=makeQuery(id+"F0.imprint","IMPRINT",FACE,{"disambiguationData":[TD([[makeQuery(id+"F0.imprint","IMPRINT",EDGE,{"derivedFrom":sQuery(id+"F0.wireOp",EDGE,"E2265")}),-1.0]])]});
            var Q18;
            Q18=makeQuery(id+"F0.imprint","IMPRINT",FACE,{"disambiguationData":[TD([[makeQuery(id+"F0.imprint","IMPRINT",EDGE,{"derivedFrom":sQuery(id+"F0.wireOp",EDGE,"E2253")}),-1.0]])]});
            var Q19;
            Q19=makeQuery(id+"F0.imprint","IMPRINT",FACE,{"disambiguationData":[TD([[makeQuery(id+"F0.imprint","IMPRINT",EDGE,{"derivedFrom":sQuery(id+"F0.wireOp",EDGE,"E2233")}),-1.0]])]});
            var Q20;
            {var subQ1=sQuery(id+"F0.wireOp",EDGE,"E517");Q20=makeQuery(id+"F0.imprint","IMPRINT",FACE,{"disambiguationData":[TD([[makeQuery(id+"F0.imprint","IMPRINT",EDGE,{"derivedFrom":subQ1}),1.0]])]});}
            extrude(context, id + "F1", {"entities" : qUnion([Q0, Q1, Q2, Q3, Q4, Q5, Q6, Q7, Q8, Q9, Q10, Q11, Q12, Q13, Q14, Q15, Q16, Q17, Q18, Q19, Q20]), "depth" : 2.4 * mm});
        }
        {
            var Q0;
            {var subQ3=sQuery(id+"F0.wireOp",EDGE,"E2323");Q0=makeQuery(id+"F0.imprint","IMPRINT",FACE,{"disambiguationData":[TD([[makeQuery(id+"F0.imprint","IMPRINT",EDGE,{"derivedFrom":subQ3}),1.0]])]});}
            var Q1;
            Q1=makeQuery(id+"F0.imprint","IMPRINT",FACE,{"disambiguationData":[TD([[makeQuery(id+"F0.imprint","IMPRINT",EDGE,{"derivedFrom":sQuery(id+"F0.wireOp",EDGE,"E523")}),1.0]])]});
            var Q2;
            {var subQ1=sQuery(id+"F0.wireOp",EDGE,"E223");Q2=makeQuery(id+"F0.imprint","IMPRINT",FACE,{"disambiguationData":[TD([[makeQuery(id+"F0.imprint","IMPRINT",EDGE,{"derivedFrom":subQ1}),1.0]])]});}
            var Q3;
            Q3=makeQuery(id+"F0.imprint","IMPRINT",FACE,{"disambiguationData":[TD([[makeQuery(id+"F0.imprint","IMPRINT",EDGE,{"derivedFrom":sQuery(id+"F0.wireOp",EDGE,"E523")}),1.0]])]});
            var Q4;
            Q4=makeQuery(id+"F0.imprint","IMPRINT",FACE,{"disambiguationData":[TD([[makeQuery(id+"F0.imprint","IMPRINT",EDGE,{"derivedFrom":sQuery(id+"F0.wireOp",EDGE,"E223")}),-1.0]])]});
            var Q5;
            {var subQ0=sQuery(id+"F0.wireOp",EDGE,"E227");Q5=makeQuery(id+"F0.imprint","IMPRINT",FACE,{"disambiguationData":[TD([[makeQuery(id+"F0.imprint","IMPRINT",EDGE,{"derivedFrom":subQ0}),-1.0]])]});}
            var Q6;
            Q6=makeQuery(id+"F0.imprint","IMPRINT",FACE,{"disambiguationData":[TD([[makeQuery(id+"F0.imprint","IMPRINT",EDGE,{"derivedFrom":sQuery(id+"F0.wireOp",EDGE,"E2149")}),-1.0]])]});
            var Q7;
            Q7=makeQuery(id+"F0.imprint","IMPRINT",FACE,{"disambiguationData":[TD([[makeQuery(id+"F0.imprint","IMPRINT",EDGE,{"derivedFrom":sQuery(id+"F0.wireOp",EDGE,"E1981")}),-1.0]])]});
            var Q8;
            Q8=makeQuery(id+"F0.imprint","IMPRINT",FACE,{"disambiguationData":[TD([[makeQuery(id+"F0.imprint","IMPRINT",EDGE,{"derivedFrom":sQuery(id+"F0.wireOp",EDGE,"E2233")}),-1.0]])]});
            var Q9;
            Q9=makeQuery(id+"F0.imprint","IMPRINT",FACE,{"disambiguationData":[TD([[makeQuery(id+"F0.imprint","IMPRINT",EDGE,{"derivedFrom":sQuery(id+"F0.wireOp",EDGE,"E2213")}),-1.0]])]});
            var Q10;
            Q10=makeQuery(id+"F0.imprint","IMPRINT",FACE,{"disambiguationData":[TD([[makeQuery(id+"F0.imprint","IMPRINT",EDGE,{"derivedFrom":sQuery(id+"F0.wireOp",EDGE,"E2253")}),-1.0]])]});
            var Q11;
            Q11=makeQuery(id+"F0.imprint","IMPRINT",FACE,{"disambiguationData":[TD([[makeQuery(id+"F0.imprint","IMPRINT",EDGE,{"derivedFrom":sQuery(id+"F0.wireOp",EDGE,"E2201")}),-1.0]])]});
            var Q12;
            Q12=makeQuery(id+"F0.imprint","IMPRINT",FACE,{"disambiguationData":[TD([[makeQuery(id+"F0.imprint","IMPRINT",EDGE,{"derivedFrom":sQuery(id+"F0.wireOp",EDGE,"E2225")}),-1.0]])]});
            var Q13;
            Q13=makeQuery(id+"F0.imprint","IMPRINT",FACE,{"disambiguationData":[TD([[makeQuery(id+"F0.imprint","IMPRINT",EDGE,{"derivedFrom":sQuery(id+"F0.wireOp",EDGE,"E2265")}),-1.0]])]});
            var Q14;
            Q14=makeQuery(id+"F0.imprint","IMPRINT",FACE,{"disambiguationData":[TD([[makeQuery(id+"F0.imprint","IMPRINT",EDGE,{"derivedFrom":sQuery(id+"F0.wireOp",EDGE,"E2281")}),-1.0]])]});
            extrude(context, id + "F2", {"entities" : qUnion([Q0, Q1, Q2, Q3, Q4, Q5, Q6, Q7, Q8, Q9, Q10, Q11, Q12, Q13, Q14]), "operationType" : NewBodyOperationType.ADD, "depth" : 5 * mm});
        }
        {
            var Q0;
            Q0=makeQuery(id+"F2.opExtrude","SWEPT_EDGE",EDGE,{"disambiguationData":[OSD([sQuery(id+"F0.wireOp",EDGE,"E2323"),sQuery(id+"F0.wireOp",EDGE,"E2324")])]});
            fillet(context, id + "F3", {"entities" : qUnion([Q0]), "radius" : 0.5 * mm, "tangentPropagation" : true, "allowEdgeOverflow" : false});
        }
    });
